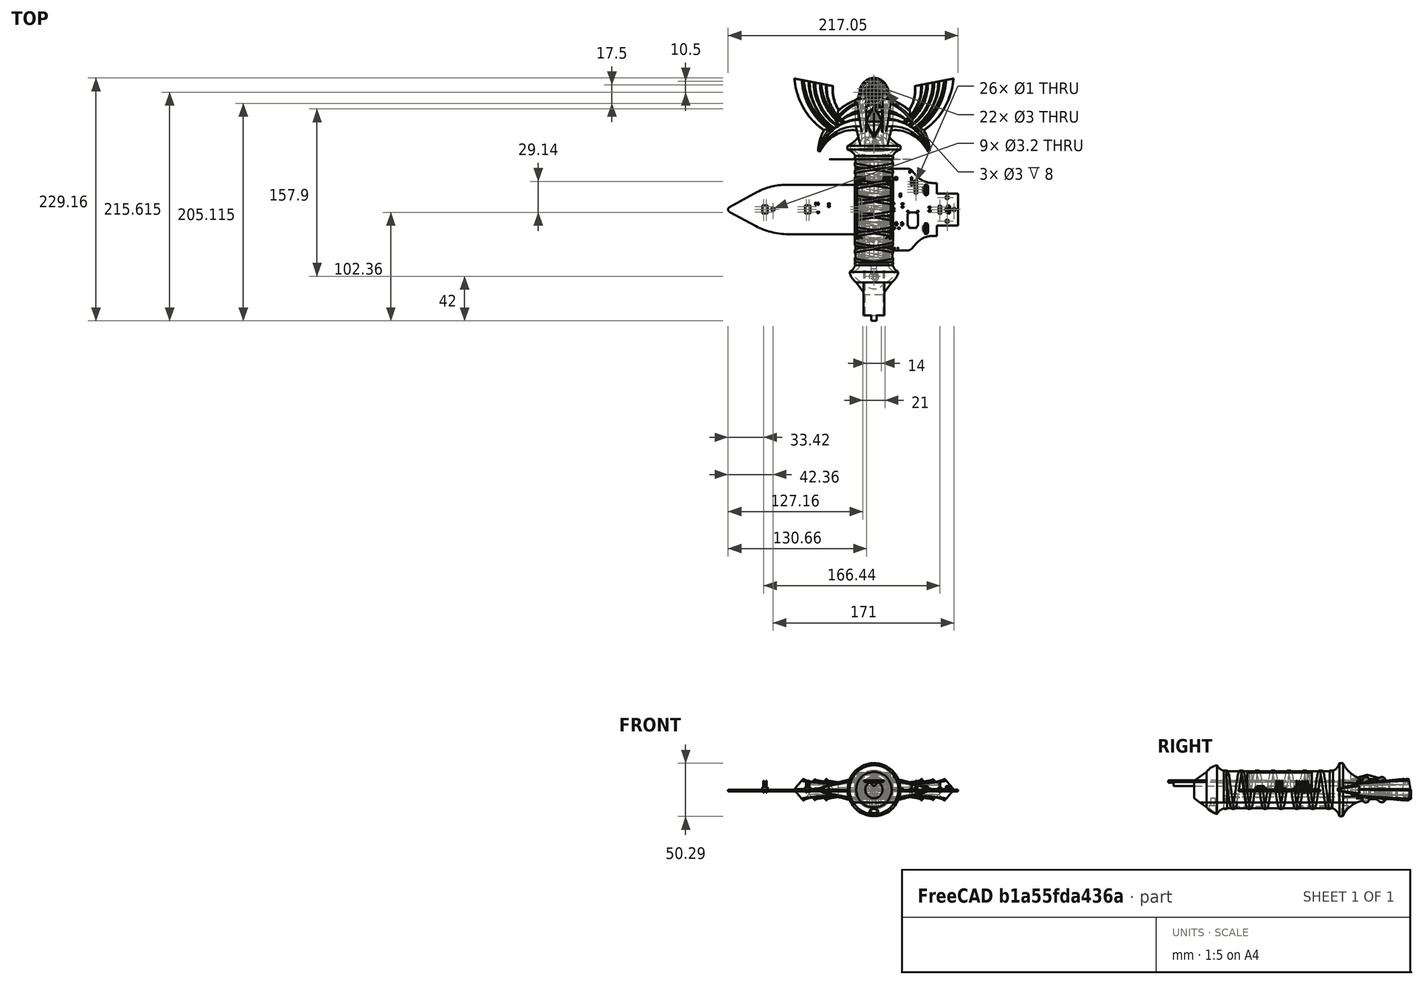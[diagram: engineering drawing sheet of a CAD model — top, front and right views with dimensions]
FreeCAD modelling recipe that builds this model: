
FCSTD DOCUMENT  (FreeCAD 1.0R39285 (Git))
Label: Neo-Neosword
License: All rights reserved
objects: Part::Feature×97, Sketcher::SketchObject×94, PartDesign::Pocket×40, PartDesign::Pad×22, PartDesign::Body×16, PartDesign::SubShapeBinder×12, App::Part×9, PartDesign::Revolution×5, PartDesign::AdditiveHelix×4, PartDesign::AdditivePipe×3, PartDesign::Groove×3, PartDesign::AdditiveLoft×2, PartDesign::Fillet×2, PartDesign::SubtractiveHelix×2, PartDesign::Mirrored×1, PartDesign::CoordinateSystem×1, PartDesign::SubtractiveCylinder×1, PartDesign::Chamfer×1, PartDesign::SubtractiveBox×1
note: 574 computed .brp shape members not serialized (recipe doc carries the construction recipe); baked Part::Feature solids carry a one-line shape summary decoded from their .brp

FEATURE [Sketcher::SketchObject] Sketch
  ArcFitTolerance = 1e-06
  AttachmentSupport = -> [XY_Plane001]
  FullyConstrained = false
  MakeInternals = false
  MapMode = 5
  sketch-geometry (17):
    g0: LineSegment StartX=17.5 StartY=50 StartZ=0 EndX=17.5 EndY=-50 EndZ=0
    g1: ArcOfCircle CenterX=27.5 CenterY=-50 CenterZ=0 NormalX=0 NormalY=0 NormalZ=1 AngleXU=0 Radius=10 StartAngle=3.14159 EndAngle=4.2478
    g2: LineSegment StartX=16.7299 StartY=-68.7091 StartZ=0 EndX=8.15223 EndY=-80.5471 EndZ=0
    g3: LineSegment StartX=8.15223 StartY=-80.5471 StartZ=0 EndX=0 EndY=-80.5471 EndZ=0
    g4: ArcOfCircle CenterX=8.2468 CenterY=-56.3383 CenterZ=0 NormalX=0 NormalY=0 NormalZ=1 AngleXU=0 Radius=15 StartAngle=5.31348 EndAngle=6.10885
    g5: ArcOfCircle CenterX=27.468 CenterY=46.0956 CenterZ=0 NormalX=0 NormalY=0 NormalZ=1 AngleXU=0 Radius=10.7054 StartAngle=1.80342 EndAngle=2.76827
    g6: LineSegment StartX=25.0001 StartY=56.5127 StartZ=0 EndX=25.0155 EndY=56.5163 EndZ=0
    g7: LineSegment StartX=25.0155 StartY=56.5163 StartZ=0 EndX=25 EndY=60 EndZ=0
    g8: ArcOfCircle CenterX=35.5717 CenterY=83.343 CenterZ=0 NormalX=0 NormalY=0 NormalZ=1 AngleXU=0 Radius=25.6254 StartAngle=3.07689 EndAngle=4.28714
    g9: LineSegment [constr] StartX=25 StartY=60 StartZ=0 EndX=41.707 EndY=52.4336 EndZ=0
    g10: LineSegment StartX=10 StartY=85 StartZ=0 EndX=4 EndY=85 EndZ=0
    g11: LineSegment [constr] StartX=0 StartY=50.6044 StartZ=0 EndX=0 EndY=85 EndZ=0
    g12: LineSegment StartX=0 StartY=-80.5471 StartZ=0 EndX=0 EndY=-51.46 EndZ=0
    g13: LineSegment StartX=0 StartY=-51.46 StartZ=0 EndX=15 EndY=-51.46 EndZ=0
    g14: LineSegment StartX=15 StartY=-51.46 StartZ=0 EndX=15 EndY=57.54 EndZ=0
    g15: LineSegment StartX=15 StartY=57.54 StartZ=0 EndX=4 EndY=57.54 EndZ=0
    g16: LineSegment StartX=4 StartY=57.54 StartZ=0 EndX=4 EndY=85 EndZ=0
  constraints (39):
    c: Symmetric(g0,g0,g-1)
    c: DistanceY(g0,g0) = 100
    c: DistanceX(g-1,g0) = 17.5
    c: Tangent(g1,g0) = -1.5708
    c: Coincident(g3,g2)
    c: PointOnObject(g3,g-2)
    c: Horizontal(g3)
    c: Coincident(g4,g1)
    c: Coincident(g2,g4)
    c: Radius(g1) = 10
    c: Radius(g4) = 15
    c: Coincident(g5,g0)
    c: Tangent(g6,g5) = 1.5708
    c: Coincident(g7,g6)
    c: Coincident(g8,g7)
    c: Coincident(g9,g7)
    c: Tangent(g8,g9)
    c: Coincident(g10,g8)
    c: PointOnObject(g11,g-2)
    c: Horizontal(g10)
    c: DistanceX(g11,g10) = 10
    c: DistanceX(g-1,g7) = 25
    c: DistanceY(g-1,g11) = 85
    c: DistanceY(g-1,g7) = 60
    c: Coincident(g3,g12)
    c: PointOnObject(g12,g-2)
    c: Coincident(g12,g13)
    c: Horizontal(g13)
    c: Coincident(g13,g14)
    c: Vertical(g14)
    c: Coincident(g14,g15)
    c: Horizontal(g15)
    c: Coincident(g15,g16)
    c: Vertical(g16)
    c: Coincident(g10,g16)
    c: DistanceY(g14,g14) = 109
    c: DistanceX(g-1,g13) = 15
    c: DistanceY(g-1,g15) = 57.54
    c: Distance(g10,g-2) = 4
FEATURE [PartDesign::Revolution] Revolution
  Angle = 360
  Angle2 = 60
  Axis = (0,1,0)
  Base = (0,0,0)
  Profile = -> Sketch
  ReferenceAxis = -> Sketch [V_Axis]
  Refine = true
  Reversed = true
  Suppressed = false
  Type = 0
FEATURE [Sketcher::SketchObject] Sketch001  label="InnerLower"
  ArcFitTolerance = 1e-06
  AttachmentOffset = pos=(0,0,0) rot=(0,-1,0;0.15708rad)
  AttachmentSupport = -> [YZ_Plane002]
  FullyConstrained = false
  MakeInternals = false
  MapMode = 5
  Placement = pos=(0,0,0) rot=(0.637718,0.544663,0.544663;2.00621rad)
  sketch-geometry (19):
    g0: LineSegment StartX=74.5124 StartY=0 StartZ=0 EndX=79.2425 EndY=9.91974 EndZ=0
    g1: LineSegment StartX=85.8137 StartY=9.96476 StartZ=0 EndX=86.5068 EndY=8.56092 EndZ=0
    g2: LineSegment StartX=88.3306 StartY=7.4275 StartZ=0 EndX=92.0222 EndY=7.42761 EndZ=0
    g3: ArcOfCircle CenterX=82.539 CenterY=8.34785 CenterZ=0 NormalX=0 NormalY=0 NormalZ=1 AngleXU=0 Radius=3.6521 StartAngle=0.458646 EndAngle=2.69665
    g4: GeomPoint [constr] X=82.4817 Y=16.7129 Z=0
    g5: GeomPoint [constr] X=100.651 Y=15.0454 Z=0
    g6: ArcOfCircle CenterX=88.3305 CenterY=9.4614 CenterZ=0 NormalX=0 NormalY=0 NormalZ=1 AngleXU=0 Radius=2.03391 StartAngle=3.60024 EndAngle=4.71242
    g7: GeomPoint [constr] X=87.0665 Y=7.42746 Z=0
    g8: GeomPoint [constr] X=93.3028 Y=7.41221 Z=0
    g9: LineSegment StartX=74.5124 StartY=0 StartZ=0 EndX=79.1575 EndY=-9.92971 EndZ=0
    g10: LineSegment StartX=85.9449 StartY=-9.87659 StartZ=0 EndX=86.4722 EndY=-8.70175 EndZ=0
    g11: LineSegment StartX=88.4642 StartY=-7.41239 StartZ=0 EndX=91.8885 EndY=-7.41239 EndZ=0
    g12: ArcOfCircle CenterX=82.539 CenterY=-8.34785 CenterZ=0 NormalX=0 NormalY=0 NormalZ=1 AngleXU=0 Radius=3.73322 StartAngle=3.57915 EndAngle=5.86128
    g13: GeomPoint [constr] X=82.6091 Y=-17.3082 Z=0
    g14: GeomPoint [constr] X=101.163 Y=-14.8795 Z=0
    g15: ArcOfCircle CenterX=88.4642 CenterY=-9.59588 CenterZ=0 NormalX=0 NormalY=0 NormalZ=1 AngleXU=0 Radius=2.18349 StartAngle=1.5708 EndAngle=2.71969
    g16: GeomPoint [constr] X=87.0509 Y=-7.41239 Z=0
    g17: GeomPoint [constr] X=93.3028 Y=-7.41221 Z=0
    g18: ArcOfCircle CenterX=92.7992 CenterY=0 CenterZ=0 NormalX=0 NormalY=0 NormalZ=1 AngleXU=0 Radius=7.46814 StartAngle=4.59013 EndAngle=7.95821
  constraints (25):
    c: PointOnObject(g0,g-1)
    c: PointOnObject(g4,g0)
    c: PointOnObject(g4,g1)
    c: Tangent(g0,g3) = 1.5708
    c: Tangent(g1,g3) = 1.5708
    c: PointOnObject(g7,g1)
    c: PointOnObject(g7,g2)
    c: Tangent(g1,g6) = -1.5708
    c: Tangent(g2,g6) = -1.5708
    c: Horizontal(g11)
    c: PointOnObject(g13,g9)
    c: PointOnObject(g13,g10)
    c: Tangent(g9,g12) = -1.5708
    c: Tangent(g10,g12) = -1.5708
    c: PointOnObject(g16,g10)
    c: PointOnObject(g16,g11)
    c: Tangent(g10,g15) = 1.5708
    c: Tangent(g11,g15) = 1.5708
    c: Coincident(g9,g0)
    c: Symmetric(g8,g17,g-1)
    c: Symmetric(g3,g12,g-1)
    c: PointOnObject(g18,g-1)
    c: Coincident(g18,g2)
    c: Coincident(g18,g11)
    c: DistanceY(g11,g2) = 14.84
FEATURE [Sketcher::SketchObject] Sketch002  label="OuterLower"
  ArcFitTolerance = 1e-06
  AttachmentOffset = pos=(0,0,-55) rot=(0,0,1;0rad)
  AttachmentSupport = -> [XZ_Plane002]
  FullyConstrained = false
  MakeInternals = false
  MapMode = 5
  Placement = pos=(0,55,-1.22e-14) rot=(1,0,0;1.5708rad)
  sketch-geometry (1):
    g0: Circle CenterX=51.7429 CenterY=0 CenterZ=0 NormalX=0 NormalY=0 NormalZ=1 AngleXU=0 Radius=1
  constraints (1):
    c: Diameter(g0) = 2
FEATURE [Sketcher::SketchObject] Sketch003  label="Arc"
  ArcFitTolerance = 1e-06
  AttachmentSupport = -> [XY_Plane002]
  FullyConstrained = false
  MakeInternals = false
  MapMode = 5
  sketch-geometry (1):
    g0: ArcOfCircle CenterX=9.26917 CenterY=46.1397 CenterZ=0 NormalX=0 NormalY=0 NormalZ=1 AngleXU=0 Radius=43.4172 StartAngle=0.208844 EndAngle=1.45835
FEATURE [PartDesign::AdditivePipe] AdditivePipe
  AuxilleryCurvelinear = true
  AuxillerySpineTangent = false
  Binormal = (0,0,0)
  Mode = 0
  Placement = pos=(0,0,0) rot=(1,1,1;2.0944rad)
  Profile = -> Sketch001
  Refine = true
  Sections = -> [Sketch002]
  Spine = -> Sketch003
  SpineTangent = false
  Suppressed = false
  Transformation = 1
  Transition = 0
FEATURE [Sketcher::SketchObject] Sketch004  label="InnerUpper"
  ArcFitTolerance = 1e-06
  AttachmentOffset = pos=(0,0,0) rot=(0,-1,0;0.15708rad)
  AttachmentSupport = -> [YZ_Plane002]
  FullyConstrained = false
  MakeInternals = false
  MapMode = 5
  Placement = pos=(0,0,0) rot=(0.637718,0.544663,0.544663;2.00621rad)
  sketch-geometry (20):
    g0: LineSegment [constr] StartX=90.1762 StartY=16.3594 StartZ=0 EndX=90.1771 EndY=-14.4859 EndZ=0
    g1: ArcOfCircle [constr] CenterX=82.5389 CenterY=8.36022 CenterZ=0 NormalX=0 NormalY=0 NormalZ=1 AngleXU=0 Radius=3.64672 StartAngle=0.455594 EndAngle=2.6997
    g2: ArcOfCircle [constr] CenterX=88.3632 CenterY=9.51401 CenterZ=0 NormalX=0 NormalY=0 NormalZ=1 AngleXU=0 Radius=2.08677 StartAngle=3.61591 EndAngle=4.69675
    g3: LineSegment [constr] StartX=85.8137 StartY=9.96476 StartZ=0 EndX=86.5068 EndY=8.56092 EndZ=0
    g4: LineSegment [constr] StartX=79.2425 StartY=9.91974 StartZ=0 EndX=74.8618 EndY=0.732718 EndZ=0
    g5: ArcOfCircle [constr] CenterX=82.5387 CenterY=-8.36022 CenterZ=0 NormalX=0 NormalY=0 NormalZ=1 AngleXU=0 Radius=3.64651 StartAngle=3.58348 EndAngle=5.82765
    g6: ArcOfCircle [constr] CenterX=88.3642 CenterY=-9.51401 CenterZ=0 NormalX=0 NormalY=0 NormalZ=1 AngleXU=0 Radius=2.08814 StartAngle=1.58646 EndAngle=2.66734
    g7: LineSegment [constr] StartX=85.8133 StartY=-9.96449 StartZ=0 EndX=86.5065 EndY=-8.56042 EndZ=0
    g8: LineSegment [constr] StartX=79.2424 StartY=-9.91964 StartZ=0 EndX=74.7059 EndY=-1.91141 EndZ=0
    g9: ArcOfCircle [constr] CenterX=64.7886 CenterY=0 CenterZ=0 NormalX=0 NormalY=0 NormalZ=1 AngleXU=0 Radius=10.0998 StartAngle=6.09278 EndAngle=6.3558
    g10: ArcOfCircle CenterX=97.8151 CenterY=8.36022 CenterZ=0 NormalX=0 NormalY=0 NormalZ=1 AngleXU=0 Radius=3.64651 StartAngle=0.441891 EndAngle=2.68605
    g11: ArcOfCircle CenterX=91.9895 CenterY=9.51401 CenterZ=0 NormalX=0 NormalY=0 NormalZ=1 AngleXU=0 Radius=2.08814 StartAngle=4.72805 EndAngle=5.80893
    g12: LineSegment StartX=94.5404 StartY=9.96449 StartZ=0 EndX=93.8472 EndY=8.56042 EndZ=0
    g13: LineSegment StartX=101.111 StartY=9.91964 StartZ=0 EndX=104.93 EndY=1.91141 EndZ=0
    g14: ArcOfCircle CenterX=97.8151 CenterY=-8.36022 CenterZ=0 NormalX=0 NormalY=0 NormalZ=1 AngleXU=0 Radius=3.64651 StartAngle=3.59713 EndAngle=5.84129
    g15: ArcOfCircle CenterX=91.9895 CenterY=-9.51401 CenterZ=0 NormalX=0 NormalY=0 NormalZ=1 AngleXU=0 Radius=2.08814 StartAngle=0.474251 EndAngle=1.55514
    g16: LineSegment StartX=94.5404 StartY=-9.96449 StartZ=0 EndX=93.8472 EndY=-8.56042 EndZ=0
    g17: LineSegment StartX=101.111 StartY=-9.91964 StartZ=0 EndX=104.93 EndY=-1.91142 EndZ=0
    g18: ArcOfCircle CenterX=115.564 CenterY=0 CenterZ=0 NormalX=0 NormalY=0 NormalZ=1 AngleXU=0 Radius=10.8041 StartAngle=2.96374 EndAngle=3.31944
    g19: ArcOfCircle CenterX=92.8797 CenterY=0 CenterZ=0 NormalX=0 NormalY=0 NormalZ=1 AngleXU=0 Radius=7.47546 StartAngle=1.68575 EndAngle=4.59744
  constraints (21):
    c: Coincident(g3,g1)
    c: Coincident(g3,g2)
    c: Coincident(g4,g1)
    c: Coincident(g7,g5)
    c: Coincident(g7,g6)
    c: Coincident(g8,g5)
    c: PointOnObject(g9,g-1)
    c: Coincident(g9,g4)
    c: Coincident(g9,g8)
    c: Coincident(g12,g10)
    c: Coincident(g12,g11)
    c: Coincident(g13,g10)
    c: Coincident(g16,g14)
    c: Coincident(g16,g15)
    c: Coincident(g17,g14)
    c: Coincident(g18,g13)
    c: Coincident(g18,g17)
    c: PointOnObject(g19,g-1)
    c: Coincident(g19,g11)
    c: Coincident(g19,g15)
    c: DistanceX(g-1,g13) = 104.93
FEATURE [Sketcher::SketchObject] Sketch005  label="OuterUpper"
  ArcFitTolerance = 1e-06
  AttachmentOffset = pos=(0,0,0) rot=(0,-1,0;0.383972rad)
  AttachmentSupport = -> [YZ_Plane002]
  FullyConstrained = false
  MakeInternals = false
  MapMode = 5
  Placement = pos=(0,0,0) rot=(0.723589,0.488067,0.488067;1.88883rad)
  sketch-geometry (5):
    g0: ArcOfCircle CenterX=85.1272 CenterY=0 CenterZ=0 NormalX=0 NormalY=0 NormalZ=1 AngleXU=0 Radius=4.5 StartAngle=1.5708 EndAngle=4.71239
    g1: ArcOfCircle CenterX=93.5 CenterY=0 CenterZ=0 NormalX=0 NormalY=0 NormalZ=1 AngleXU=0 Radius=4.5 StartAngle=4.71239 EndAngle=7.85398
    g2: LineSegment StartX=85.1272 StartY=4.5 StartZ=0 EndX=93.5 EndY=4.5 EndZ=0
    g3: LineSegment StartX=85.1272 StartY=-4.5 StartZ=0 EndX=93.5 EndY=-4.5 EndZ=0
    g4: GeomPoint X=98 Y=0 Z=0
  constraints (11):
    c: Tangent(g0,g2) = 1.5708
    c: Tangent(g0,g3) = -1.5708
    c: Tangent(g1,g2) = 1.5708
    c: Tangent(g1,g3) = -1.5708
    c: Equal(g0,g1)
    c: Horizontal(g3)
    c: PointOnObject(g0,g-1)
    c: PointOnObject(g4,g1)
    c: PointOnObject(g4,g-1)
    c: DistanceX(g-1,g4) = 98
    c: DistanceY(g1,g1) = 9
FEATURE [Sketcher::SketchObject] Sketch006  label="UpperArc"
  ArcFitTolerance = 1e-06
  AttachmentSupport = -> [XY_Plane002]
  FullyConstrained = false
  MakeInternals = false
  MapMode = 5
  sketch-geometry (1):
    g0: ArcOfCircle CenterX=9.26917 CenterY=46.1397 CenterZ=0 NormalX=0 NormalY=0 NormalZ=1 AngleXU=0 Radius=43.4172 StartAngle=1.05064 EndAngle=1.45835
FEATURE [PartDesign::AdditivePipe] AdditivePipe001
  AuxilleryCurvelinear = true
  AuxillerySpineTangent = false
  BaseFeature = -> AdditivePipe
  Binormal = (0,0,0)
  Mode = 0
  Placement = pos=(0,0,0) rot=(1,1,1;2.0944rad)
  Profile = -> Sketch004
  Refine = true
  Sections = -> [Sketch005]
  Spine = -> Sketch006
  SpineTangent = false
  Suppressed = false
  Transformation = 1
  Transition = 0
FEATURE [Sketcher::SketchObject] Sketch007  label="WingOuter"
  ArcFitTolerance = 1e-06
  AttachmentOffset = pos=(0,0,-109) rot=(0,2,0;0.191986rad)
  AttachmentSupport = -> [XZ_Plane002]
  FullyConstrained = false
  MakeInternals = false
  MapMode = 5
  Placement = pos=(0,109,-2.42e-14) rot=(0.990855,0.095409,0.095409;1.57998rad)
  sketch-geometry (35):
    g0: LineSegment StartX=76.3672 StartY=0.659592 StartZ=0 EndX=68.1495 EndY=10.0239 EndZ=0
    g1: LineSegment StartX=67.3939 StartY=10.0194 StartZ=0 EndX=62.9614 EndY=4.84362 EndZ=0
    g2: LineSegment StartX=61.8579 StartY=4.8047 StartZ=0 EndX=57.0799 EndY=9.64699 EndZ=0
    g3: LineSegment StartX=56.3686 StartY=9.64753 StartZ=0 EndX=51.5834 EndY=4.8124 EndZ=0
    g4: LineSegment StartX=50.48 StartY=4.85298 StartZ=0 EndX=46.1175 EndY=9.96245 EndZ=0
    g5: LineSegment StartX=45.3168 StartY=9.90834 StartZ=0 EndX=39.6601 EndY=1.11712 EndZ=0
    g6: LineSegment [constr] StartX=56.7313 StartY=18.9744 StartZ=0 EndX=56.7109 EndY=-8.18983 EndZ=0
    g7: ArcOfCircle CenterX=45.7372 CenterY=9.63779 CenterZ=0 NormalX=0 NormalY=0 NormalZ=1 AngleXU=0 Radius=0.5 StartAngle=0.706698 EndAngle=2.56984
    g8: GeomPoint [constr] X=45.6807 Y=10.474 Z=0
    g9: ArcOfCircle CenterX=56.724 CenterY=9.29581 CenterZ=0 NormalX=0 NormalY=0 NormalZ=1 AngleXU=0 Radius=0.5 StartAngle=0.778708 EndAngle=2.36138
    g10: GeomPoint [constr] X=56.7245 Y=10.0072 Z=0
    g11: ArcOfCircle CenterX=67.7737 CenterY=9.69413 CenterZ=0 NormalX=0 NormalY=0 NormalZ=1 AngleXU=0 Radius=0.5 StartAngle=0.720275 EndAngle=2.43339
    g12: GeomPoint [constr] X=67.769 Y=10.4574 Z=0
    g13: ArcOfCircle CenterX=62.3917 CenterY=5.33147 CenterZ=0 NormalX=0 NormalY=0 NormalZ=1 AngleXU=0 Radius=0.75 StartAngle=3.9203 EndAngle=5.57499
    g14: GeomPoint [constr] X=62.4308 Y=4.22405 Z=0
    g15: ArcOfCircle CenterX=51.0504 CenterY=5.33997 CenterZ=0 NormalX=0 NormalY=0 NormalZ=1 AngleXU=0 Radius=0.75 StartAngle=3.84829 EndAngle=5.50298
    g16: GeomPoint [constr] X=51.0096 Y=4.23262 Z=0
    g17: LineSegment StartX=76.3672 StartY=-0.659592 StartZ=0 EndX=68.1495 EndY=-10.0239 EndZ=0
    g18: LineSegment StartX=67.3939 StartY=-10.0194 StartZ=0 EndX=62.9614 EndY=-4.84362 EndZ=0
    g19: LineSegment StartX=61.8579 StartY=-4.8047 StartZ=0 EndX=57.0799 EndY=-9.64699 EndZ=0
    g20: LineSegment StartX=56.3686 StartY=-9.64753 StartZ=0 EndX=51.5834 EndY=-4.8124 EndZ=0
    g21: LineSegment StartX=50.48 StartY=-4.85298 StartZ=0 EndX=46.119 EndY=-9.96064 EndZ=0
    g22: LineSegment StartX=45.3174 StartY=-9.90511 StartZ=0 EndX=39.6564 EndY=-1.04163 EndZ=0
    g23: ArcOfCircle CenterX=45.7388 CenterY=-9.63598 CenterZ=0 NormalX=0 NormalY=0 NormalZ=1 AngleXU=0 Radius=0.5 StartAngle=3.70997 EndAngle=5.57649
    g24: GeomPoint [constr] X=45.6807 Y=-10.474 Z=0
    g25: ArcOfCircle CenterX=56.724 CenterY=-9.29581 CenterZ=0 NormalX=0 NormalY=0 NormalZ=1 AngleXU=0 Radius=0.5 StartAngle=3.9218 EndAngle=5.50448
    g26: GeomPoint [constr] X=56.7245 Y=-10.0072 Z=0
    g27: ArcOfCircle CenterX=67.7737 CenterY=-9.69413 CenterZ=0 NormalX=0 NormalY=0 NormalZ=1 AngleXU=0 Radius=0.5 StartAngle=3.84979 EndAngle=5.56291
    g28: GeomPoint [constr] X=67.769 Y=-10.4574 Z=0
    g29: ArcOfCircle CenterX=62.3917 CenterY=-5.33147 CenterZ=0 NormalX=0 NormalY=0 NormalZ=1 AngleXU=0 Radius=0.75 StartAngle=0.708198 EndAngle=2.36289
    g30: GeomPoint [constr] X=62.4308 Y=-4.22405 Z=0
    g31: ArcOfCircle CenterX=51.0504 CenterY=-5.33997 CenterZ=0 NormalX=0 NormalY=0 NormalZ=1 AngleXU=0 Radius=0.75 StartAngle=0.780208 EndAngle=2.43489
    g32: GeomPoint [constr] X=51.0096 Y=-4.23262 Z=0
    g33: ArcOfCircle CenterX=75.6156 CenterY=0 CenterZ=0 NormalX=0 NormalY=0 NormalZ=1 AngleXU=0 Radius=1 StartAngle=5.56291 EndAngle=7.00346
    g34: ArcOfCircle CenterX=41.342 CenterY=0.0349059 CenterZ=0 NormalX=0 NormalY=0 NormalZ=1 AngleXU=0 Radius=2 StartAngle=2.56984 EndAngle=3.70997
  constraints (59):
    c: PointOnObject(g10,g6)
    c: Symmetric(g16,g14,g6)
    c: Symmetric(g12,g8,g6)
    c: PointOnObject(g8,g5)
    c: PointOnObject(g8,g4)
    c: Tangent(g5,g7) = -1.5708
    c: Tangent(g4,g7) = -1.5708
    c: PointOnObject(g10,g3)
    c: PointOnObject(g10,g2)
    c: Tangent(g3,g9) = -1.5708
    c: Tangent(g2,g9) = -1.5708
    c: PointOnObject(g12,g1)
    c: PointOnObject(g12,g0)
    c: Tangent(g1,g11) = -1.5708
    c: Tangent(g0,g11) = -1.5708
    c: PointOnObject(g14,g2)
    c: PointOnObject(g14,g1)
    c: Tangent(g2,g13) = 1.5708
    c: Tangent(g1,g13) = 1.5708
    c: PointOnObject(g16,g4)
    c: PointOnObject(g16,g3)
    c: Tangent(g4,g15) = 1.5708
    c: Tangent(g3,g15) = 1.5708
    c: Radius(g7) = 0.5
    c: Radius(g9) = 0.5
    c: Radius(g11) = 0.5
    c: Radius(g13) = 0.75
    c: Radius(g15) = 0.75
    c: PointOnObject(g24,g22)
    c: PointOnObject(g24,g21)
    c: Tangent(g22,g23) = 1.5708
    c: Tangent(g21,g23) = 1.5708
    c: PointOnObject(g26,g20)
    c: PointOnObject(g26,g19)
    c: Tangent(g20,g25) = 1.5708
    c: Tangent(g19,g25) = 1.5708
    c: PointOnObject(g28,g18)
    c: PointOnObject(g28,g17)
    c: Tangent(g18,g27) = 1.5708
    c: Tangent(g17,g27) = 1.5708
    c: PointOnObject(g30,g19)
    c: PointOnObject(g30,g18)
    c: Tangent(g19,g29) = -1.5708
    c: Tangent(g18,g29) = -1.5708
    c: PointOnObject(g32,g21)
    c: PointOnObject(g32,g20)
    c: Tangent(g21,g31) = -1.5708
    c: Tangent(g20,g31) = -1.5708
    c: Radius(g23) = 0.5
    c: Radius(g25) = 0.5
    c: Radius(g27) = 0.5
    c: Radius(g29) = 0.75
    c: Radius(g31) = 0.75
    c: Tangent(g0,g33) = -1.5708
    c: Tangent(g17,g33) = 1.5708
    c: Tangent(g5,g34) = -1.5708
    c: Tangent(g22,g34) = 1.5708
    c: Radius(g34) = 2
    c: Radius(g33) = 1
FEATURE [Sketcher::SketchObject] Sketch008  label="WingInner"
  ArcFitTolerance = 1e-06
  AttachmentOffset = pos=(0,0,-94) rot=(0,1,0;-0.471239rad)
  AttachmentSupport = -> [XZ_Plane002]
  FullyConstrained = false
  MakeInternals = false
  MapMode = 5
  Placement = pos=(0,94,-2.09e-14) rot=(-0.94691,0.227333,0.227333;4.65787rad)
  sketch-geometry (24):
    g0: LineSegment StartX=24.9312 StartY=0 StartZ=0 EndX=28.939 EndY=6.0573 EndZ=0
    g1: LineSegment StartX=29.7174 StartY=6.12695 StartZ=0 EndX=32.213 EndY=3.51707 EndZ=0
    g2: LineSegment StartX=32.213 StartY=3.51707 StartZ=0 EndX=36.2883 EndY=6.3926 EndZ=0
    g3: LineSegment StartX=36.8654 StartY=6.39214 StartZ=0 EndX=40.9263 EndY=3.51707 EndZ=0
    g4: LineSegment StartX=40.9263 StartY=3.51707 StartZ=0 EndX=43.3532 EndY=5.56491 EndZ=0
    g5: LineSegment StartX=44.0749 StartY=5.48373 StartZ=0 EndX=48.2081 EndY=0 EndZ=0
    g6: LineSegment [constr] StartX=36.5696 StartY=10.6947 StartZ=0 EndX=36.5696 EndY=-8.06706 EndZ=0
    g7: ArcOfCircle CenterX=29.356 CenterY=5.7814 CenterZ=0 NormalX=0 NormalY=0 NormalZ=1 AngleXU=0 Radius=0.5 StartAngle=0.763015 EndAngle=2.55707
    g8: GeomPoint [constr] X=29.2846 Y=6.57957 Z=0
    g9: ArcOfCircle CenterX=36.5765 CenterY=5.98406 CenterZ=0 NormalX=0 NormalY=0 NormalZ=1 AngleXU=0 Radius=0.5 StartAngle=0.954722 EndAngle=2.18527
    g10: ArcOfCircle CenterX=43.6756 CenterY=5.18278 CenterZ=0 NormalX=0 NormalY=0 NormalZ=1 AngleXU=0 Radius=0.5 StartAngle=0.645874 EndAngle=2.27169
    g11: GeomPoint [constr] X=43.7569 Y=5.90561 Z=0
    g12: LineSegment StartX=24.9312 StartY=0 StartZ=0 EndX=28.939 EndY=-6.0573 EndZ=0
    g13: LineSegment StartX=29.7174 StartY=-6.12695 StartZ=0 EndX=32.213 EndY=-3.51707 EndZ=0
    g14: LineSegment StartX=32.213 StartY=-3.51707 StartZ=0 EndX=36.2883 EndY=-6.3926 EndZ=0
    g15: LineSegment StartX=36.8654 StartY=-6.39214 StartZ=0 EndX=40.9263 EndY=-3.51707 EndZ=0
    g16: LineSegment StartX=40.9263 StartY=-3.51707 StartZ=0 EndX=43.3532 EndY=-5.56491 EndZ=0
    g17: LineSegment StartX=44.0749 StartY=-5.48373 StartZ=0 EndX=48.2081 EndY=0 EndZ=0
    g18: ArcOfCircle CenterX=29.356 CenterY=-5.7814 CenterZ=0 NormalX=0 NormalY=0 NormalZ=1 AngleXU=0 Radius=0.5 StartAngle=3.72612 EndAngle=5.52017
    g19: GeomPoint [constr] X=29.2846 Y=-6.57957 Z=0
    g20: ArcOfCircle CenterX=36.5765 CenterY=-5.98406 CenterZ=0 NormalX=0 NormalY=0 NormalZ=1 AngleXU=0 Radius=0.5 StartAngle=4.09791 EndAngle=5.32846
    g21: GeomPoint [constr] X=36.577 Y=-6.59635 Z=0
    g22: ArcOfCircle CenterX=43.6756 CenterY=-5.18278 CenterZ=0 NormalX=0 NormalY=0 NormalZ=1 AngleXU=0 Radius=0.5 StartAngle=4.0115 EndAngle=5.63731
    g23: GeomPoint [constr] X=43.7569 Y=-5.90561 Z=0
  constraints (44):
    c: PointOnObject(g0,g-1)
    c: Coincident(g1,g2)
    c: Coincident(g3,g4)
    c: PointOnObject(g5,g-1)
    c: Symmetric(g1,g3,g6)
    c: Symmetric(g0,g5,g6)
    c: PointOnObject(g8,g0)
    c: PointOnObject(g8,g1)
    c: Tangent(g0,g7) = 1.5708
    c: Tangent(g1,g7) = 1.5708
    c: Tangent(g2,g9) = 1.5708
    c: Tangent(g3,g9) = 1.5708
    c: PointOnObject(g11,g4)
    c: PointOnObject(g11,g5)
    c: Tangent(g4,g10) = 1.5708
    c: Tangent(g5,g10) = 1.5708
    c: Radius(g10) = 0.5
    c: Radius(g9) = 0.5
    c: Radius(g7) = 0.5
    c: Coincident(g13,g14)
    c: Coincident(g15,g16)
    c: PointOnObject(g19,g12)
    c: PointOnObject(g19,g13)
    c: Tangent(g12,g18) = -1.5708
    c: Tangent(g13,g18) = -1.5708
    c: PointOnObject(g21,g14)
    c: PointOnObject(g21,g15)
    c: Tangent(g14,g20) = -1.5708
    c: Tangent(g15,g20) = -1.5708
    c: PointOnObject(g23,g16)
    c: PointOnObject(g23,g17)
    c: Tangent(g16,g22) = -1.5708
    c: Tangent(g17,g22) = -1.5708
    c: Radius(g22) = 0.5
    c: Radius(g20) = 0.5
    c: Radius(g18) = 0.5
    c: Symmetric(g7,g18,g-1)
    c: Symmetric(g20,g9,g-1)
    c: Coincident(g12,g0)
    c: Coincident(g17,g5)
    c: Vertical(g3,g15)
    c: Horizontal(g13,g15)
    c: Symmetric(g13,g1,g-1)
    c: Symmetric(g10,g22,g-1)
FEATURE [Sketcher::SketchObject] Sketch009  label="WingArc"
  ArcFitTolerance = 1e-06
  AttachmentSupport = -> [XY_Plane002]
  FullyConstrained = false
  MakeInternals = false
  MapMode = 5
  sketch-geometry (3):
    g0: GeomPoint [constr] X=32.5902 Y=77.3945 Z=0
    g1: GeomPoint [constr] X=55.6821 Y=119.824 Z=0
    g2: ArcOfCircle CenterX=5.31743 CenterY=119.736 CenterZ=0 NormalX=0 NormalY=0 NormalZ=1 AngleXU=0 Radius=50.3647 StartAngle=5.28462 EndAngle=6.28492
  constraints (2):
    c: Coincident(g2,g1)
    c: Coincident(g2,g0)
FEATURE [PartDesign::AdditivePipe] AdditivePipe002
  AuxilleryCurvelinear = true
  AuxillerySpineTangent = false
  BaseFeature = -> AdditivePipe001
  Binormal = (0,0,0)
  Mode = 0
  Placement = pos=(0,0,0) rot=(1,1,1;2.0944rad)
  Profile = -> Sketch008
  Refine = true
  Sections = -> [Sketch007]
  Spine = -> Sketch009
  SpineTangent = false
  Suppressed = false
  Transformation = 1
  Transition = 0
FEATURE [PartDesign::Mirrored] Mirrored
  BaseFeature = -> AdditivePipe002
  MirrorPlane = -> YZ_Plane002
  Originals = -> [AdditivePipe,AdditivePipe001,AdditivePipe002]
  Placement = pos=(0,0,0) rot=(1,1,1;2.0944rad)
  Refine = true
  Suppressed = false
  TransformMode = 0
FEATURE [Sketcher::SketchObject] Sketch010
  ArcFitTolerance = 1e-06
  AttachmentSupport = -> [XY_Plane003]
  FullyConstrained = false
  MakeInternals = false
  MapMode = 5
  sketch-geometry (18):
    g0: LineSegment StartX=12.6399 StartY=59.9845 StartZ=0 EndX=-12.6399 EndY=59.9845 EndZ=0
    g1: LineSegment StartX=-12.6399 StartY=59.9845 StartZ=0 EndX=-17.8679 EndY=82.0584 EndZ=0
    g2: LineSegment StartX=-17.8679 StartY=82.0584 StartZ=0 EndX=-17.8679 EndY=102.222 EndZ=0
    g3: LineSegment StartX=-15.8679 StartY=104.222 StartZ=0 EndX=-8.15434 EndY=104.222 EndZ=0
    g4: LineSegment StartX=-7.15434 StartY=103.222 StartZ=0 EndX=-7.15434 EndY=92.1893 EndZ=0
    g5: LineSegment StartX=-7.15434 StartY=92.1893 StartZ=0 EndX=7.15434 EndY=92.1893 EndZ=0
    g6: LineSegment StartX=7.15434 StartY=92.1893 StartZ=0 EndX=7.15434 EndY=103.222 EndZ=0
    g7: LineSegment StartX=8.15434 StartY=104.222 StartZ=0 EndX=15.8679 EndY=104.222 EndZ=0
    g8: LineSegment StartX=17.8679 StartY=102.222 StartZ=0 EndX=17.8679 EndY=82.0584 EndZ=0
    g9: LineSegment StartX=17.8679 StartY=82.0584 StartZ=0 EndX=12.6399 EndY=59.9845 EndZ=0
    g10: ArcOfCircle CenterX=-15.8679 CenterY=102.222 CenterZ=0 NormalX=0 NormalY=0 NormalZ=1 AngleXU=0 Radius=2 StartAngle=1.5708 EndAngle=3.14159
    g11: GeomPoint [constr] X=-17.8679 Y=104.222 Z=0
    g12: ArcOfCircle CenterX=15.8679 CenterY=102.222 CenterZ=0 NormalX=0 NormalY=0 NormalZ=1 AngleXU=0 Radius=2 StartAngle=-9e-16 EndAngle=1.5708
    g13: GeomPoint [constr] X=17.8679 Y=104.222 Z=0
    g14: ArcOfCircle CenterX=-8.15434 CenterY=103.222 CenterZ=0 NormalX=0 NormalY=0 NormalZ=1 AngleXU=0 Radius=1 StartAngle=0 EndAngle=1.5708
    g15: GeomPoint [constr] X=-7.15434 Y=104.222 Z=0
    g16: ArcOfCircle CenterX=8.15434 CenterY=103.222 CenterZ=0 NormalX=0 NormalY=0 NormalZ=1 AngleXU=0 Radius=1 StartAngle=1.5708 EndAngle=3.14159
    g17: GeomPoint [constr] X=7.15434 Y=104.222 Z=0
  constraints (35):
    c: Coincident(g0,g1)
    c: Coincident(g1,g2)
    c: Vertical(g2)
    c: Horizontal(g3)
    c: Vertical(g4)
    c: Coincident(g4,g5)
    c: Horizontal(g5)
    c: Coincident(g5,g6)
    c: Coincident(g8,g9)
    c: Coincident(g9,g0)
    c: Symmetric(g0,g0,g-2)
    c: Symmetric(g1,g8,g-2)
    c: Symmetric(g11,g13,g-2)
    c: Symmetric(g15,g17,g-2)
    c: Vertical(g6)
    c: PointOnObject(g11,g3)
    c: PointOnObject(g11,g2)
    c: Tangent(g3,g10) = 1.5708
    c: Tangent(g2,g10) = 1.5708
    c: PointOnObject(g13,g7)
    c: PointOnObject(g13,g8)
    c: Tangent(g7,g12) = 1.5708
    c: Tangent(g8,g12) = 1.5708
    c: PointOnObject(g15,g3)
    c: PointOnObject(g15,g4)
    c: Tangent(g3,g14) = 1.5708
    c: Tangent(g4,g14) = 1.5708
    c: PointOnObject(g17,g7)
    c: PointOnObject(g17,g6)
    c: Tangent(g7,g16) = 1.5708
    c: Tangent(g6,g16) = 1.5708
    c: Radius(g10) = 2
    c: Radius(g12) = 2
    c: Radius(g16) = 1
    c: Radius(g14) = 1
FEATURE [PartDesign::Pad] Pad
  Direction = (0,0,1)
  Length = 24
  Length2 = 10
  Midplane = true
  Profile = -> Sketch010
  ReferenceAxis = -> Sketch010 [N_Axis]
  Refine = true
  Suppressed = false
  Type = 0
FEATURE [Sketcher::SketchObject] Sketch011
  ArcFitTolerance = 1e-06
  AttachmentOffset = pos=(0,0,-54) rot=(0,0,1;0rad)
  AttachmentSupport = -> [XZ_Plane003]
  FullyConstrained = false
  MakeInternals = false
  MapMode = 5
  Placement = pos=(0,54,-1.2e-14) rot=(1,0,0;1.5708rad)
  sketch-geometry (24):
    g0: LineSegment StartX=-18.5965 StartY=0 StartZ=0 EndX=-18.5965 EndY=5.28721 EndZ=0
    g1: LineSegment StartX=-18.5965 StartY=5.28721 StartZ=0 EndX=-8.15434 EndY=8 EndZ=0
    g2: LineSegment StartX=0 StartY=13.8139 StartZ=0 EndX=-22.1179 EndY=13.8139 EndZ=0
    g3: LineSegment StartX=-22.1179 StartY=13.8139 StartZ=0 EndX=-22.1179 EndY=-0.189388 EndZ=0
    g4: LineSegment StartX=-8.15434 StartY=8 StartZ=0 EndX=-7.4432 EndY=8.1798 EndZ=0
    g5: LineSegment StartX=-7.4432 StartY=8.1798 StartZ=0 EndX=0 EndY=8.1798 EndZ=0
    g6: LineSegment StartX=-18.5965 StartY=0 StartZ=0 EndX=-18.5965 EndY=-5.37112 EndZ=0
    g7: LineSegment StartX=-18.5965 StartY=-5.37112 StartZ=0 EndX=-8.15434 EndY=-8 EndZ=0
    g8: LineSegment StartX=0 StartY=-17.7434 StartZ=0 EndX=-22.1179 EndY=-17.7434 EndZ=0
    g9: LineSegment StartX=-22.1179 StartY=-17.7434 StartZ=0 EndX=-22.1179 EndY=-0.189388 EndZ=0
    g10: LineSegment StartX=-8.15434 StartY=-8 StartZ=0 EndX=-7.4432 EndY=-8.25332 EndZ=0
    g11: LineSegment StartX=-7.4432 StartY=-8.25332 StartZ=0 EndX=0.11104 EndY=-8.25332 EndZ=0
    g12: LineSegment StartX=18.5313 StartY=-0.112287 StartZ=0 EndX=18.5313 EndY=5.28721 EndZ=0
    g13: LineSegment StartX=18.5313 StartY=5.28721 StartZ=0 EndX=8.15434 EndY=8 EndZ=0
    g14: LineSegment StartX=0 StartY=13.8139 StartZ=0 EndX=22.6589 EndY=13.8139 EndZ=0
    g15: LineSegment StartX=22.6589 StartY=13.8139 StartZ=0 EndX=22.6589 EndY=-0.111897 EndZ=0
    g16: LineSegment StartX=8.15434 StartY=8 StartZ=0 EndX=7.51991 EndY=8.1798 EndZ=0
    g17: LineSegment StartX=7.51991 StartY=8.1798 StartZ=0 EndX=0 EndY=8.1798 EndZ=0
    g18: LineSegment StartX=18.5313 StartY=-0.112287 StartZ=0 EndX=18.5313 EndY=-5.39949 EndZ=0
    g19: LineSegment StartX=18.5313 StartY=-5.39949 StartZ=0 EndX=8.15434 EndY=-8 EndZ=0
    g20: LineSegment StartX=0 StartY=-17.7434 StartZ=0 EndX=22.6589 EndY=-17.7434 EndZ=0
    g21: LineSegment StartX=22.6589 StartY=-17.7434 StartZ=0 EndX=22.6589 EndY=-0.111897 EndZ=0
    g22: LineSegment StartX=8.15434 StartY=-8 StartZ=0 EndX=7.55424 EndY=-8.25332 EndZ=0
    g23: LineSegment StartX=7.55424 StartY=-8.25332 StartZ=0 EndX=0.11104 EndY=-8.25332 EndZ=0
  constraints (43):
    c: PointOnObject(g0,g-1)
    c: Vertical(g0)
    c: Coincident(g0,g1)
    c: Horizontal(g2)
    c: Coincident(g2,g3)
    c: Vertical(g3)
    c: Coincident(g1,g4)
    c: Coincident(g4,g5)
    c: PointOnObject(g5,g-2)
    c: Horizontal(g5)
    c: PointOnObject(g2,g-2)
    c: Vertical(g6)
    c: Coincident(g6,g7)
    c: Horizontal(g8)
    c: Coincident(g8,g9)
    c: Vertical(g9)
    c: Coincident(g7,g10)
    c: Coincident(g10,g11)
    c: Horizontal(g11)
    c: Vertical(g12)
    c: Coincident(g12,g13)
    c: Horizontal(g14)
    c: Coincident(g14,g15)
    c: Vertical(g15)
    c: Coincident(g13,g16)
    c: Coincident(g16,g17)
    c: Horizontal(g17)
    c: Vertical(g18)
    c: Coincident(g18,g19)
    c: Horizontal(g20)
    c: Coincident(g20,g21)
    c: Vertical(g21)
    c: Coincident(g19,g22)
    c: Coincident(g22,g23)
    c: Horizontal(g23)
    c: Coincident(g9,g3)
    c: Coincident(g6,g0)
    c: Coincident(g21,g15)
    c: Coincident(g18,g12)
    c: Coincident(g5,g17)
    c: Coincident(g2,g14)
    c: Coincident(g23,g11)
    c: Coincident(g8,g20)
FEATURE [PartDesign::Pocket] Pocket
  BaseFeature = -> Pad
  Direction = (0,1,-2e-16)
  Length = 62
  Length2 = 5
  Profile = -> Sketch011
  ReferenceAxis = -> Sketch011 [N_Axis]
  Refine = true
  Suppressed = false
  Type = 0
FEATURE [Sketcher::SketchObject] Sketch012  label="Diamond001"
  ArcFitTolerance = 1e-06
  AttachmentOffset = pos=(0,0,8) rot=(0,0,1;0rad)
  AttachmentSupport = -> [XY_Plane004]
  FullyConstrained = false
  MakeInternals = false
  MapMode = 5
  Placement = pos=(0,0,8) rot=(0,0,1;0rad)
  sketch-geometry (5):
    g0: LineSegment StartX=0 StartY=93.5332 StartZ=0 EndX=-7.90137 EndY=79.1802 EndZ=0
    g1: LineSegment StartX=-7.90137 StartY=79.1802 StartZ=0 EndX=0 EndY=64.8272 EndZ=0
    g2: LineSegment StartX=0 StartY=93.5332 StartZ=0 EndX=7.90137 EndY=79.1802 EndZ=0
    g3: LineSegment StartX=7.90137 StartY=79.1802 StartZ=0 EndX=0 EndY=64.8272 EndZ=0
    g4: LineSegment [constr] StartX=-7.90137 StartY=79.1802 StartZ=0 EndX=7.90137 EndY=79.1802 EndZ=0
  constraints (9):
    c: PointOnObject(g0,g-2)
    c: Coincident(g0,g1)
    c: Coincident(g2,g3)
    c: Coincident(g0,g2)
    c: Coincident(g1,g3)
    c: Coincident(g4,g0)
    c: Coincident(g4,g2)
    c: Symmetric(g0,g1,g4)
    c: Symmetric(g0,g2,g-2)
FEATURE [Sketcher::SketchObject] Sketch013
  ArcFitTolerance = 1e-06
  AttachmentOffset = pos=(0,0,8) rot=(0,0,1;0rad)
  AttachmentSupport = -> [XY_Plane001]
  FullyConstrained = false
  MakeInternals = false
  MapMode = 5
  Placement = pos=(0,0,8) rot=(0,0,1;0rad)
  sketch-geometry (8):
    g0: LineSegment [constr] StartX=0 StartY=97 StartZ=0 EndX=-7.9 EndY=83 EndZ=0
    g1: LineSegment [constr] StartX=-7.9 StartY=83 StartZ=0 EndX=1.8e-15 EndY=68.3 EndZ=0
    g2: LineSegment [constr] StartX=0 StartY=97 StartZ=0 EndX=7.9 EndY=83 EndZ=0
    g3: LineSegment [constr] StartX=7.9 StartY=83 StartZ=0 EndX=1.8e-15 EndY=68.3 EndZ=0
    g4: LineSegment StartX=0 StartY=98 StartZ=0 EndX=-8.9 EndY=83 EndZ=0
    g5: LineSegment StartX=-8.9 StartY=83 StartZ=0 EndX=0 EndY=67.3 EndZ=0
    g6: LineSegment StartX=0 StartY=67.3 StartZ=0 EndX=8.9 EndY=83 EndZ=0
    g7: LineSegment StartX=8.9 StartY=83 StartZ=0 EndX=0 EndY=98 EndZ=0
  constraints (22):
    c: PointOnObject(g0,g-2)
    c: Coincident(g0,g1)
    c: Coincident(g2,g3)
    c: Coincident(g0,g2)
    c: Coincident(g1,g3)
    c: Symmetric(g0,g2,g-2)
    c: PointOnObject(g4,g-2)
    c: Coincident(g4,g5)
    c: PointOnObject(g5,g-2)
    c: Coincident(g5,g6)
    c: Coincident(g6,g7)
    c: Coincident(g7,g4)
    c: Horizontal(g0,g4)
    c: Horizontal(g2,g6)
    c: DistanceX(g-1,g2) = 7.9
    c: DistanceY(g5,g1) = 1
    c: DistanceY(g0,g4) = 1
    c: DistanceX(g2,g6) = 1
    c: DistanceX(g4,g0) = 1
    c: DistanceY(g-1,g4) = 98
    c: DistanceY(g5,g4) = 30.7
    c: DistanceY(g4,g4) = 15
FEATURE [PartDesign::Pocket] Pocket001  label="Diamond Dimple"
  BaseFeature = -> Revolution
  Direction = (0,0,-1)
  Length = 21
  Length2 = 5
  Profile = -> Sketch013
  ReferenceAxis = -> Sketch013 [N_Axis]
  Refine = true
  Reversed = true
  Suppressed = false
  Type = 0
FEATURE [Sketcher::SketchObject] Sketch014
  ArcFitTolerance = 1e-06
  AttachmentSupport = -> [YZ_Plane004]
  ExternalGeometry = -> [Sketch012]
  FullyConstrained = false
  MakeInternals = false
  MapMode = 5
  Placement = pos=(0,0,0) rot=(0.57735,0.57735,0.57735;2.0944rad)
  sketch-geometry (1):
    g0: LineSegment StartX=79.1802 StartY=8 StartZ=0 EndX=79.1802 EndY=12.611 EndZ=0
  constraints (2):
    c: Vertical(g0)
    c: Coincident(g0,g-3)
FEATURE [PartDesign::AdditiveLoft] AdditiveLoft
  Closed = false
  Profile = -> Sketch012
  Refine = true
  Ruled = false
  Sections = -> [Sketch014]
  Suppressed = false
FEATURE [PartDesign::Body] Body003  label="Diamond"
  AllowCompound = true
  Group = -> [Sketch012,Sketch014,AdditiveLoft]
  Origin = -> Origin004
  Tip = -> AdditiveLoft
FEATURE [Sketcher::SketchObject] Sketch015
  ArcFitTolerance = 1e-06
  AttachmentSupport = -> [YZ_Plane005]
  FullyConstrained = true
  MakeInternals = false
  MapMode = 5
  Placement = pos=(0,0,0) rot=(0.57735,0.57735,0.57735;2.0944rad)
  sketch-geometry (4):
    g0: ArcOfCircle CenterX=-52 CenterY=17.5 CenterZ=0 NormalX=0 NormalY=0 NormalZ=1 AngleXU=0 Radius=0.6 StartAngle=1.5708 EndAngle=4.71239
    g1: ArcOfCircle CenterX=-50 CenterY=17.5 CenterZ=0 NormalX=0 NormalY=0 NormalZ=1 AngleXU=0 Radius=0.6 StartAngle=4.71239 EndAngle=7.85398
    g2: LineSegment StartX=-52 StartY=18.1 StartZ=0 EndX=-50 EndY=18.1 EndZ=0
    g3: LineSegment StartX=-52 StartY=16.9 StartZ=0 EndX=-50 EndY=16.9 EndZ=0
  constraints (10):
    c: Tangent(g0,g2) = 1.5708
    c: Tangent(g0,g3) = -1.5708
    c: Tangent(g1,g2) = 1.5708
    c: Tangent(g1,g3) = -1.5708
    c: Equal(g0,g1)
    c: Horizontal(g2)
    c: DistanceX(g0,g1) = 2
    c: DistanceY(g1,g1) = 1.2
    c: DistanceY(g-1,g0) = 17.5
    c: DistanceX(g1,g-1) = 50
FEATURE [PartDesign::Revolution] Revolution001
  Angle = 360
  Angle2 = 60
  Axis = (0,1,0)
  Base = (0,0,0)
  Placement = pos=(0,0,0) rot=(1,1,1;2.0944rad)
  Profile = -> Sketch015
  ReferenceAxis = -> Sketch015 [H_Axis]
  Refine = true
  Suppressed = false
  Type = 0
FEATURE [Sketcher::SketchObject] Sketch016
  ArcFitTolerance = 1e-06
  AttachmentSupport = -> [YZ_Plane005]
  FullyConstrained = true
  MakeInternals = false
  MapMode = 5
  Placement = pos=(0,0,0) rot=(0.57735,0.57735,0.57735;2.0944rad)
  sketch-geometry (4):
    g0: ArcOfCircle CenterX=48 CenterY=17.5 CenterZ=0 NormalX=0 NormalY=0 NormalZ=1 AngleXU=0 Radius=0.6 StartAngle=1.5708 EndAngle=4.71239
    g1: ArcOfCircle CenterX=50 CenterY=17.5 CenterZ=0 NormalX=0 NormalY=0 NormalZ=1 AngleXU=0 Radius=0.6 StartAngle=4.71239 EndAngle=7.85398
    g2: LineSegment StartX=48 StartY=18.1 StartZ=0 EndX=50 EndY=18.1 EndZ=0
    g3: LineSegment StartX=48 StartY=16.9 StartZ=0 EndX=50 EndY=16.9 EndZ=0
  constraints (10):
    c: Tangent(g0,g2) = 1.5708
    c: Tangent(g0,g3) = -1.5708
    c: Tangent(g1,g2) = 1.5708
    c: Tangent(g1,g3) = -1.5708
    c: Equal(g0,g1)
    c: Horizontal(g2)
    c: DistanceX(g0,g1) = 2
    c: DistanceY(g1,g1) = 1.2
    c: DistanceY(g-1,g0) = 17.5
    c: DistanceX(g-1,g0) = 48
FEATURE [PartDesign::Revolution] Revolution002
  Angle = 360
  Angle2 = 60
  Axis = (0,1,0)
  Base = (0,0,0)
  BaseFeature = -> Revolution001
  Placement = pos=(0,0,0) rot=(1,1,1;2.0944rad)
  Profile = -> Sketch016
  ReferenceAxis = -> Sketch016 [H_Axis]
  Refine = true
  Suppressed = false
  Type = 0
FEATURE [Sketcher::SketchObject] Sketch017
  ArcFitTolerance = 1e-06
  AttachmentSupport = -> [YZ_Plane005]
  FullyConstrained = true
  MakeInternals = false
  MapMode = 5
  Placement = pos=(0,0,0) rot=(0.57735,0.57735,0.57735;2.0944rad)
  sketch-geometry (4):
    g0: ArcOfCircle CenterX=-52 CenterY=17.5 CenterZ=0 NormalX=0 NormalY=0 NormalZ=1 AngleXU=0 Radius=0.6 StartAngle=1.5708 EndAngle=4.71239
    g1: ArcOfCircle CenterX=-50 CenterY=17.5 CenterZ=0 NormalX=0 NormalY=0 NormalZ=1 AngleXU=0 Radius=0.6 StartAngle=4.71239 EndAngle=7.85398
    g2: LineSegment StartX=-52 StartY=18.1 StartZ=0 EndX=-50 EndY=18.1 EndZ=0
    g3: LineSegment StartX=-52 StartY=16.9 StartZ=0 EndX=-50 EndY=16.9 EndZ=0
  constraints (10):
    c: Tangent(g0,g2) = 1.5708
    c: Tangent(g0,g3) = -1.5708
    c: Tangent(g1,g2) = 1.5708
    c: Tangent(g1,g3) = -1.5708
    c: Equal(g0,g1)
    c: Horizontal(g2)
    c: DistanceX(g0,g1) = 2
    c: DistanceY(g1,g1) = 1.2
    c: DistanceY(g-1,g0) = 17.5
    c: DistanceX(g1,g-1) = 50
FEATURE [PartDesign::AdditiveHelix] AdditiveHelix
  Angle = 0
  Axis = (0,1,0)
  Base = (0,0,0)
  BaseFeature = -> Revolution002
  Growth = 0
  HasBeenEdited = true
  Height = 100
  LeftHanded = false
  Mode = 0
  Outside = false
  Pitch = 15
  Placement = pos=(0,0,0) rot=(1,1,1;2.0944rad)
  Profile = -> Sketch017
  ReferenceAxis = -> Sketch017 [H_Axis]
  Refine = true
  Suppressed = false
  Tolerance = 0.1
  Turns = 6.66667
FEATURE [Sketcher::SketchObject] Sketch018
  ArcFitTolerance = 1e-06
  AttachmentSupport = -> [YZ_Plane005]
  FullyConstrained = true
  MakeInternals = false
  MapMode = 5
  Placement = pos=(0,0,0) rot=(0.57735,0.57735,0.57735;2.0944rad)
  sketch-geometry (4):
    g0: ArcOfCircle CenterX=-52 CenterY=17.5 CenterZ=0 NormalX=0 NormalY=0 NormalZ=1 AngleXU=0 Radius=0.6 StartAngle=1.5708 EndAngle=4.71239
    g1: ArcOfCircle CenterX=-50 CenterY=17.5 CenterZ=0 NormalX=0 NormalY=0 NormalZ=1 AngleXU=0 Radius=0.6 StartAngle=4.71239 EndAngle=7.85398
    g2: LineSegment StartX=-52 StartY=18.1 StartZ=0 EndX=-50 EndY=18.1 EndZ=0
    g3: LineSegment StartX=-52 StartY=16.9 StartZ=0 EndX=-50 EndY=16.9 EndZ=0
  constraints (10):
    c: Tangent(g0,g2) = 1.5708
    c: Tangent(g0,g3) = -1.5708
    c: Tangent(g1,g2) = 1.5708
    c: Tangent(g1,g3) = -1.5708
    c: Equal(g0,g1)
    c: Horizontal(g2)
    c: DistanceX(g0,g1) = 2
    c: DistanceY(g1,g1) = 1.2
    c: DistanceY(g-1,g0) = 17.5
    c: DistanceX(g1,g-1) = 50
FEATURE [PartDesign::AdditiveHelix] AdditiveHelix001
  Angle = 0
  Axis = (0,1,0)
  Base = (0,0,0)
  BaseFeature = -> AdditiveHelix
  Growth = 0
  HasBeenEdited = true
  Height = 100
  LeftHanded = true
  Mode = 0
  Outside = false
  Pitch = 15
  Placement = pos=(0,0,0) rot=(1,1,1;2.0944rad)
  Profile = -> Sketch018
  ReferenceAxis = -> Sketch018 [H_Axis]
  Refine = true
  Suppressed = false
  Tolerance = 0.1
  Turns = 6.66667
FEATURE [PartDesign::CoordinateSystem] Local_CS_259c
  AttacherType = Attacher::AttachEngine3D
  MapMode = 2
FEATURE [Part::Feature] Pcb_259c
  Placement = pos=(-179.7,105.7,0) rot=(0,0,1;0rad)
  shape: bbox 217 x 77.11 x 1.6 mm, 325 faces (baked)
FEATURE [Sketcher::SketchObject] PCB_Sketch_259c
  ArcFitTolerance = 1e-06
  FullyConstrained = false
  MakeInternals = false
  sketch-geometry (225):
    g0: LineSegment StartX=-137.665 StartY=0.013451 StartZ=0 EndX=-137.658 EndY=0.196135 EndZ=0
    g1: LineSegment StartX=-137.658 StartY=0.196135 StartZ=0 EndX=-137.64 EndY=0.376444 EndZ=0
    g2: LineSegment StartX=-137.64 StartY=0.376444 StartZ=0 EndX=-137.609 EndY=0.553855 EndZ=0
    g3: LineSegment StartX=-137.609 StartY=0.553855 StartZ=0 EndX=-137.567 EndY=0.727848 EndZ=0
    g4: LineSegment StartX=-137.567 StartY=0.727848 StartZ=0 EndX=-137.514 EndY=0.897898 EndZ=0
    g5: LineSegment StartX=-137.514 StartY=0.897898 StartZ=0 EndX=-137.449 EndY=1.06348 EndZ=0
    g6: LineSegment StartX=-137.449 StartY=1.06348 StartZ=0 EndX=-137.374 EndY=1.22408 EndZ=0
    g7: LineSegment StartX=-137.374 StartY=1.22408 StartZ=0 EndX=-137.288 EndY=1.37917 EndZ=0
    g8: LineSegment StartX=-137.288 StartY=1.37917 StartZ=0 EndX=-137.192 EndY=1.52823 EndZ=0
    g9: LineSegment StartX=-137.192 StartY=1.52823 StartZ=0 EndX=-137.087 EndY=1.67073 EndZ=0
    g10: LineSegment StartX=-137.087 StartY=1.67073 StartZ=0 EndX=-136.971 EndY=1.80615 EndZ=0
    g11: LineSegment StartX=-136.971 StartY=1.80615 StartZ=0 EndX=-136.847 EndY=1.93398 EndZ=0
    g12: LineSegment StartX=-136.847 StartY=1.93398 StartZ=0 EndX=-136.714 EndY=2.05368 EndZ=0
    g13: LineSegment StartX=-136.714 StartY=2.05368 StartZ=0 EndX=-136.572 EndY=2.16473 EndZ=0
    g14: LineSegment StartX=-136.572 StartY=2.16473 StartZ=0 EndX=-136.422 EndY=2.26662 EndZ=0
    g15: LineSegment StartX=-136.422 StartY=2.26662 StartZ=0 EndX=-136.265 EndY=2.35882 EndZ=0
    g16: LineSegment StartX=-136.265 StartY=2.35882 StartZ=0 EndX=-110.065 EndY=16.4831 EndZ=0
    g17: LineSegment StartX=-110.065 StartY=16.4831 StartZ=0 EndX=-108.497 EndY=17.297 EndZ=0
    g18: LineSegment StartX=-108.497 StartY=17.297 StartZ=0 EndX=-106.908 EndY=18.0606 EndZ=0
    g19: LineSegment StartX=-106.908 StartY=18.0606 StartZ=0 EndX=-105.298 EndY=18.7737 EndZ=0
    g20: LineSegment StartX=-105.298 StartY=18.7737 StartZ=0 EndX=-103.669 EndY=19.4359 EndZ=0
    g21: LineSegment StartX=-103.669 StartY=19.4359 StartZ=0 EndX=-102.022 EndY=20.0468 EndZ=0
    g22: LineSegment StartX=-102.022 StartY=20.0468 StartZ=0 EndX=-100.357 EndY=20.6063 EndZ=0
    g23: LineSegment StartX=-100.357 StartY=20.6063 StartZ=0 EndX=-98.6774 EndY=21.1139 EndZ=0
    g24: LineSegment StartX=-98.6774 StartY=21.1139 StartZ=0 EndX=-96.9831 EndY=21.5694 EndZ=0
    g25: LineSegment StartX=-96.9831 StartY=21.5694 StartZ=0 EndX=-95.2755 EndY=21.9725 EndZ=0
    g26: LineSegment StartX=-95.2755 StartY=21.9725 StartZ=0 EndX=-93.5559 EndY=22.3228 EndZ=0
    g27: LineSegment StartX=-93.5559 StartY=22.3228 StartZ=0 EndX=-91.8256 EndY=22.6201 EndZ=0
    g28: LineSegment StartX=-91.8256 StartY=22.6201 StartZ=0 EndX=-90.0856 EndY=22.8641 EndZ=0
    g29: LineSegment StartX=-90.0856 StartY=22.8641 StartZ=0 EndX=-88.3373 EndY=23.0543 EndZ=0
    g30: LineSegment StartX=-88.3373 StartY=23.0543 StartZ=0 EndX=-86.5819 EndY=23.1906 EndZ=0
    g31: LineSegment StartX=-86.5819 StartY=23.1906 StartZ=0 EndX=-84.8206 EndY=23.2726 EndZ=0
    g32: LineSegment StartX=-84.8206 StartY=23.2726 StartZ=0 EndX=-83.0546 EndY=23.3 EndZ=0
    g33: LineSegment StartX=-83.0546 StartY=23.3 StartZ=0 EndX=-19.5 EndY=23.3 EndZ=0
    g34: LineSegment StartX=-19.5 StartY=23.3 StartZ=0 EndX=-18.7908 EndY=23.3126 EndZ=0
    g35: LineSegment StartX=-18.7908 StartY=23.3126 StartZ=0 EndX=-18.084 EndY=23.3502 EndZ=0
    g36: LineSegment StartX=-18.084 StartY=23.3502 StartZ=0 EndX=-17.3804 EndY=23.4126 EndZ=0
    g37: LineSegment StartX=-17.3804 StartY=23.4126 StartZ=0 EndX=-16.6805 EndY=23.4997 EndZ=0
    g38: LineSegment StartX=-16.6805 StartY=23.4997 StartZ=0 EndX=-15.9849 EndY=23.6113 EndZ=0
    g39: LineSegment StartX=-15.9849 StartY=23.6113 StartZ=0 EndX=-15.2943 EndY=23.7472 EndZ=0
    g40: LineSegment StartX=-15.2943 StartY=23.7472 StartZ=0 EndX=-14.6093 EndY=23.9072 EndZ=0
    g41: LineSegment StartX=-14.6093 StartY=23.9072 StartZ=0 EndX=-13.9306 EndY=24.0911 EndZ=0
    g42: LineSegment StartX=-13.9306 StartY=24.0911 StartZ=0 EndX=-13.2588 EndY=24.2988 EndZ=0
    g43: LineSegment StartX=-13.2588 StartY=24.2988 StartZ=0 EndX=-12.5944 EndY=24.53 EndZ=0
    g44: LineSegment StartX=-12.5944 StartY=24.53 StartZ=0 EndX=-11.9383 EndY=24.7846 EndZ=0
    g45: LineSegment StartX=-11.9383 StartY=24.7846 StartZ=0 EndX=-11.2909 EndY=25.0624 EndZ=0
    g46: LineSegment StartX=-11.2909 StartY=25.0624 StartZ=0 EndX=-10.6529 EndY=25.3632 EndZ=0
    g47: LineSegment StartX=-10.6529 StartY=25.3632 StartZ=0 EndX=-10.025 EndY=25.6868 EndZ=0
    g48: LineSegment StartX=-10.025 StartY=25.6868 StartZ=0 EndX=-9.40773 EndY=26.0331 EndZ=0
    g49: LineSegment StartX=-9.40773 StartY=26.0331 StartZ=0 EndX=-8.8018 EndY=26.4018 EndZ=0
    g50: LineSegment StartX=-8.8018 StartY=26.4018 StartZ=0 EndX=9.1896 EndY=37.7921 EndZ=0
    g51: LineSegment StartX=9.1896 StartY=37.7921 StartZ=0 EndX=9.34108 EndY=37.8843 EndZ=0
    g52: LineSegment StartX=9.34108 StartY=37.8843 StartZ=0 EndX=9.49539 EndY=37.9709 EndZ=0
    g53: LineSegment StartX=9.49539 StartY=37.9709 StartZ=0 EndX=9.65237 EndY=38.0518 EndZ=0
    g54: LineSegment StartX=9.65237 StartY=38.0518 StartZ=0 EndX=9.81186 EndY=38.127 EndZ=0
    g55: LineSegment StartX=9.81186 StartY=38.127 StartZ=0 EndX=9.9737 EndY=38.1964 EndZ=0
    g56: LineSegment StartX=9.9737 StartY=38.1964 StartZ=0 EndX=10.1377 EndY=38.2601 EndZ=0
    g57: LineSegment StartX=10.1377 StartY=38.2601 StartZ=0 EndX=10.3038 EndY=38.3179 EndZ=0
    g58: LineSegment StartX=10.3038 StartY=38.3179 StartZ=0 EndX=10.4718 EndY=38.3698 EndZ=0
    g59: LineSegment StartX=10.4718 StartY=38.3698 StartZ=0 EndX=10.6415 EndY=38.4158 EndZ=0
    g60: LineSegment StartX=10.6415 StartY=38.4158 StartZ=0 EndX=10.8127 EndY=38.4558 EndZ=0
    g61: LineSegment StartX=10.8127 StartY=38.4558 StartZ=0 EndX=10.9853 EndY=38.4898 EndZ=0
    g62: LineSegment StartX=10.9853 StartY=38.4898 StartZ=0 EndX=11.1592 EndY=38.5177 EndZ=0
    g63: LineSegment StartX=11.1592 StartY=38.5177 StartZ=0 EndX=11.3342 EndY=38.5395 EndZ=0
    g64: LineSegment StartX=11.3342 StartY=38.5395 StartZ=0 EndX=11.5101 EndY=38.5551 EndZ=0
    g65: LineSegment StartX=11.5101 StartY=38.5551 StartZ=0 EndX=11.6868 EndY=38.5645 EndZ=0
    g66: LineSegment StartX=11.6868 StartY=38.5645 StartZ=0 EndX=11.8641 EndY=38.5676 EndZ=0
    g67: LineSegment StartX=11.8641 StartY=38.5676 StartZ=0 EndX=31.8641 EndY=38.5676 EndZ=0
    g68: LineSegment StartX=31.8641 StartY=38.5676 StartZ=0 EndX=32.1279 EndY=38.5606 EndZ=0
    g69: LineSegment StartX=32.1279 StartY=38.5606 StartZ=0 EndX=32.3896 EndY=38.5399 EndZ=0
    g70: LineSegment StartX=32.3896 StartY=38.5399 StartZ=0 EndX=32.6487 EndY=38.5057 EndZ=0
    g71: LineSegment StartX=32.6487 StartY=38.5057 StartZ=0 EndX=32.9049 EndY=38.4581 EndZ=0
    g72: LineSegment StartX=32.9049 StartY=38.4581 StartZ=0 EndX=33.1576 EndY=38.3974 EndZ=0
    g73: LineSegment StartX=33.1576 StartY=38.3974 StartZ=0 EndX=33.4064 EndY=38.3238 EndZ=0
    g74: LineSegment StartX=33.4064 StartY=38.3238 StartZ=0 EndX=33.6506 EndY=38.2376 EndZ=0
    g75: LineSegment StartX=33.6506 StartY=38.2376 StartZ=0 EndX=33.89 EndY=38.1388 EndZ=0
    g76: LineSegment StartX=33.89 StartY=38.1388 StartZ=0 EndX=34.1239 EndY=38.0278 EndZ=0
    g77: LineSegment StartX=34.1239 StartY=38.0278 StartZ=0 EndX=34.3518 EndY=37.9048 EndZ=0
    g78: LineSegment StartX=34.3518 StartY=37.9048 StartZ=0 EndX=34.5734 EndY=37.77 EndZ=0
    g79: LineSegment StartX=34.5734 StartY=37.77 StartZ=0 EndX=34.7881 EndY=37.6236 EndZ=0
    g80: LineSegment StartX=34.7881 StartY=37.6236 StartZ=0 EndX=34.9954 EndY=37.4657 EndZ=0
    g81: LineSegment StartX=34.9954 StartY=37.4657 StartZ=0 EndX=35.1949 EndY=37.2967 EndZ=0
    g82: LineSegment StartX=35.1949 StartY=37.2967 StartZ=0 EndX=35.386 EndY=37.1168 EndZ=0
    g83: LineSegment StartX=35.386 StartY=37.1168 StartZ=0 EndX=35.5683 EndY=36.9261 EndZ=0
    g84: LineSegment StartX=35.5683 StartY=36.9261 StartZ=0 EndX=40.4159 EndY=31.5796 EndZ=0
    g85: LineSegment StartX=40.4159 StartY=31.5796 StartZ=0 EndX=41.145 EndY=30.8168 EndZ=0
    g86: LineSegment StartX=41.145 StartY=30.8168 StartZ=0 EndX=41.9095 EndY=30.0969 EndZ=0
    g87: LineSegment StartX=41.9095 StartY=30.0969 StartZ=0 EndX=42.7074 EndY=29.421 EndZ=0
    g88: LineSegment StartX=42.7074 StartY=29.421 StartZ=0 EndX=43.5366 EndY=28.7896 EndZ=0
    g89: LineSegment StartX=43.5366 StartY=28.7896 StartZ=0 EndX=44.3954 EndY=28.2039 EndZ=0
    g90: LineSegment StartX=44.3954 StartY=28.2039 StartZ=0 EndX=45.2818 EndY=27.6646 EndZ=0
    g91: LineSegment StartX=45.2818 StartY=27.6646 StartZ=0 EndX=46.1937 EndY=27.1725 EndZ=0
    g92: LineSegment StartX=46.1937 StartY=27.1725 StartZ=0 EndX=47.1293 EndY=26.7286 EndZ=0
    g93: LineSegment StartX=47.1293 StartY=26.7286 StartZ=0 EndX=48.0866 EndY=26.3336 EndZ=0
    g94: LineSegment StartX=48.0866 StartY=26.3336 StartZ=0 EndX=49.0637 EndY=25.9886 EndZ=0
    g95: LineSegment StartX=49.0637 StartY=25.9886 StartZ=0 EndX=50.0586 EndY=25.6942 EndZ=0
    g96: LineSegment StartX=50.0586 StartY=25.6942 StartZ=0 EndX=51.0694 EndY=25.4515 EndZ=0
    g97: LineSegment StartX=51.0694 StartY=25.4515 StartZ=0 EndX=52.0941 EndY=25.2612 EndZ=0
    g98: LineSegment StartX=52.0941 StartY=25.2612 StartZ=0 EndX=53.1308 EndY=25.1242 EndZ=0
    g99: LineSegment StartX=53.1308 StartY=25.1242 StartZ=0 EndX=54.1775 EndY=25.0413 EndZ=0
    g100: LineSegment StartX=54.1775 StartY=25.0413 StartZ=0 EndX=55.2324 EndY=25.0135 EndZ=0
    g101: LineSegment StartX=55.2324 StartY=25.0135 StartZ=0 EndX=59.3852 EndY=25.0135 EndZ=0
    g102: LineSegment StartX=59.3852 StartY=25.0135 StartZ=0 EndX=59.3852 EndY=15.0135 EndZ=0
    g103: LineSegment StartX=59.3852 StartY=15.0135 StartZ=0 EndX=79.3852 EndY=15.0135 EndZ=0
    g104: LineSegment StartX=79.3852 StartY=15.0135 StartZ=0 EndX=79.3852 EndY=-14.9865 EndZ=0
    g105: LineSegment StartX=79.3852 StartY=-14.9865 StartZ=0 EndX=59.3852 EndY=-14.9865 EndZ=0
    g106: LineSegment StartX=59.3852 StartY=-14.9865 StartZ=0 EndX=59.3852 EndY=-24.9865 EndZ=0
    g107: LineSegment StartX=59.3852 StartY=-24.9865 StartZ=0 EndX=55.2324 EndY=-24.9865 EndZ=0
    g108: LineSegment StartX=55.2324 StartY=-24.9865 StartZ=0 EndX=54.1775 EndY=-25.0143 EndZ=0
    g109: LineSegment StartX=54.1775 StartY=-25.0143 StartZ=0 EndX=53.1308 EndY=-25.0971 EndZ=0
    g110: LineSegment StartX=53.1308 StartY=-25.0971 StartZ=0 EndX=52.0941 EndY=-25.2341 EndZ=0
    g111: LineSegment StartX=52.0941 StartY=-25.2341 StartZ=0 EndX=51.0693 EndY=-25.4244 EndZ=0
    g112: LineSegment StartX=51.0693 StartY=-25.4244 StartZ=0 EndX=50.0585 EndY=-25.6672 EndZ=0
    g113: LineSegment StartX=50.0585 StartY=-25.6672 StartZ=0 EndX=49.0636 EndY=-25.9615 EndZ=0
    g114: LineSegment StartX=49.0636 StartY=-25.9615 StartZ=0 EndX=48.0866 EndY=-26.3066 EndZ=0
    g115: LineSegment StartX=48.0866 StartY=-26.3066 StartZ=0 EndX=47.1293 EndY=-26.7015 EndZ=0
    g116: LineSegment StartX=47.1293 StartY=-26.7015 StartZ=0 EndX=46.1937 EndY=-27.1454 EndZ=0
    g117: LineSegment StartX=46.1937 StartY=-27.1454 StartZ=0 EndX=45.2817 EndY=-27.6375 EndZ=0
    g118: LineSegment StartX=45.2817 StartY=-27.6375 StartZ=0 EndX=44.3954 EndY=-28.1768 EndZ=0
    g119: LineSegment StartX=44.3954 StartY=-28.1768 StartZ=0 EndX=43.5366 EndY=-28.7626 EndZ=0
    g120: LineSegment StartX=43.5366 StartY=-28.7626 StartZ=0 EndX=42.7073 EndY=-29.3939 EndZ=0
    g121: LineSegment StartX=42.7073 StartY=-29.3939 StartZ=0 EndX=41.9095 EndY=-30.0699 EndZ=0
    g122: LineSegment StartX=41.9095 StartY=-30.0699 StartZ=0 EndX=41.145 EndY=-30.7897 EndZ=0
    g123: LineSegment StartX=41.145 StartY=-30.7897 StartZ=0 EndX=40.4159 EndY=-31.5525 EndZ=0
    g124: LineSegment StartX=40.4159 StartY=-31.5525 StartZ=0 EndX=35.5683 EndY=-36.899 EndZ=0
    g125: LineSegment StartX=35.5683 StartY=-36.899 StartZ=0 EndX=35.386 EndY=-37.0897 EndZ=0
    g126: LineSegment StartX=35.386 StartY=-37.0897 StartZ=0 EndX=35.1949 EndY=-37.2697 EndZ=0
    g127: LineSegment StartX=35.1949 StartY=-37.2697 StartZ=0 EndX=34.9954 EndY=-37.4387 EndZ=0
    g128: LineSegment StartX=34.9954 StartY=-37.4387 StartZ=0 EndX=34.7881 EndY=-37.5965 EndZ=0
    g129: LineSegment StartX=34.7881 StartY=-37.5965 StartZ=0 EndX=34.5734 EndY=-37.743 EndZ=0
    g130: LineSegment StartX=34.5734 StartY=-37.743 StartZ=0 EndX=34.3518 EndY=-37.8778 EndZ=0
    g131: LineSegment StartX=34.3518 StartY=-37.8778 StartZ=0 EndX=34.1238 EndY=-38.0008 EndZ=0
    g132: LineSegment StartX=34.1238 StartY=-38.0008 StartZ=0 EndX=33.8899 EndY=-38.1118 EndZ=0
    g133: LineSegment StartX=33.8899 StartY=-38.1118 StartZ=0 EndX=33.6506 EndY=-38.2105 EndZ=0
    g134: LineSegment StartX=33.6506 StartY=-38.2105 StartZ=0 EndX=33.4063 EndY=-38.2968 EndZ=0
    g135: LineSegment StartX=33.4063 StartY=-38.2968 StartZ=0 EndX=33.1576 EndY=-38.3704 EndZ=0
    g136: LineSegment StartX=33.1576 StartY=-38.3704 StartZ=0 EndX=32.9049 EndY=-38.4311 EndZ=0
    g137: LineSegment StartX=32.9049 StartY=-38.4311 StartZ=0 EndX=32.6487 EndY=-38.4787 EndZ=0
    g138: LineSegment StartX=32.6487 StartY=-38.4787 StartZ=0 EndX=32.3896 EndY=-38.5129 EndZ=0
    g139: LineSegment StartX=32.3896 StartY=-38.5129 StartZ=0 EndX=32.1279 EndY=-38.5336 EndZ=0
    g140: LineSegment StartX=32.1279 StartY=-38.5336 StartZ=0 EndX=31.8641 EndY=-38.5406 EndZ=0
    g141: LineSegment StartX=31.8641 StartY=-38.5406 StartZ=0 EndX=11.8641 EndY=-38.5405 EndZ=0
    g142: LineSegment StartX=11.8641 StartY=-38.5405 StartZ=0 EndX=11.6868 EndY=-38.5374 EndZ=0
    g143: LineSegment StartX=11.6868 StartY=-38.5374 StartZ=0 EndX=11.5102 EndY=-38.528 EndZ=0
    g144: LineSegment StartX=11.5102 StartY=-38.528 StartZ=0 EndX=11.3343 EndY=-38.5124 EndZ=0
    g145: LineSegment StartX=11.3343 StartY=-38.5124 StartZ=0 EndX=11.1593 EndY=-38.4906 EndZ=0
    g146: LineSegment StartX=11.1593 StartY=-38.4906 StartZ=0 EndX=10.9854 EndY=-38.4627 EndZ=0
    g147: LineSegment StartX=10.9854 StartY=-38.4627 StartZ=0 EndX=10.8127 EndY=-38.4287 EndZ=0
    g148: LineSegment StartX=10.8127 StartY=-38.4287 StartZ=0 EndX=10.6415 EndY=-38.3887 EndZ=0
    g149: LineSegment StartX=10.6415 StartY=-38.3887 StartZ=0 EndX=10.4718 EndY=-38.3428 EndZ=0
    g150: LineSegment StartX=10.4718 StartY=-38.3428 StartZ=0 EndX=10.3039 EndY=-38.2909 EndZ=0
    g151: LineSegment StartX=10.3039 StartY=-38.2909 StartZ=0 EndX=10.1378 EndY=-38.233 EndZ=0
    g152: LineSegment StartX=10.1378 StartY=-38.233 StartZ=0 EndX=9.97375 EndY=-38.1694 EndZ=0
    g153: LineSegment StartX=9.97375 StartY=-38.1694 StartZ=0 EndX=9.8119 EndY=-38.0999 EndZ=0
    g154: LineSegment StartX=9.8119 StartY=-38.0999 StartZ=0 EndX=9.65241 EndY=-38.0247 EndZ=0
    g155: LineSegment StartX=9.65241 StartY=-38.0247 StartZ=0 EndX=9.49543 EndY=-37.9438 EndZ=0
    g156: LineSegment StartX=9.49543 StartY=-37.9438 StartZ=0 EndX=9.34111 EndY=-37.8573 EndZ=0
    g157: LineSegment StartX=9.34111 StartY=-37.8573 StartZ=0 EndX=9.18963 EndY=-37.7651 EndZ=0
    g158: LineSegment StartX=9.18963 StartY=-37.7651 StartZ=0 EndX=-8.8018 EndY=-26.3748 EndZ=0
    g159: LineSegment StartX=-8.8018 StartY=-26.3748 StartZ=0 EndX=-9.40774 EndY=-26.006 EndZ=0
    g160: LineSegment StartX=-9.40774 StartY=-26.006 StartZ=0 EndX=-10.025 EndY=-25.6598 EndZ=0
    g161: LineSegment StartX=-10.025 StartY=-25.6598 StartZ=0 EndX=-10.6529 EndY=-25.3361 EndZ=0
    g162: LineSegment StartX=-10.6529 StartY=-25.3361 StartZ=0 EndX=-11.2909 EndY=-25.0353 EndZ=0
    g163: LineSegment StartX=-11.2909 StartY=-25.0353 StartZ=0 EndX=-11.9383 EndY=-24.7575 EndZ=0
    g164: LineSegment StartX=-11.9383 StartY=-24.7575 StartZ=0 EndX=-12.5944 EndY=-24.5029 EndZ=0
    g165: LineSegment StartX=-12.5944 StartY=-24.5029 StartZ=0 EndX=-13.2588 EndY=-24.2717 EndZ=0
    g166: LineSegment StartX=-13.2588 StartY=-24.2717 StartZ=0 EndX=-13.9306 EndY=-24.0641 EndZ=0
    g167: LineSegment StartX=-13.9306 StartY=-24.0641 StartZ=0 EndX=-14.6093 EndY=-23.8802 EndZ=0
    g168: LineSegment StartX=-14.6093 StartY=-23.8802 StartZ=0 EndX=-15.2943 EndY=-23.7202 EndZ=0
    g169: LineSegment StartX=-15.2943 StartY=-23.7202 StartZ=0 EndX=-15.9849 EndY=-23.5843 EndZ=0
    g170: LineSegment StartX=-15.9849 StartY=-23.5843 StartZ=0 EndX=-16.6805 EndY=-23.4727 EndZ=0
    g171: LineSegment StartX=-16.6805 StartY=-23.4727 StartZ=0 EndX=-17.3804 EndY=-23.3856 EndZ=0
    g172: LineSegment StartX=-17.3804 StartY=-23.3856 StartZ=0 EndX=-18.084 EndY=-23.3232 EndZ=0
    g173: LineSegment StartX=-18.084 StartY=-23.3232 StartZ=0 EndX=-18.7908 EndY=-23.2856 EndZ=0
    g174: LineSegment StartX=-18.7908 StartY=-23.2856 StartZ=0 EndX=-19.5 EndY=-23.273 EndZ=0
    g175: LineSegment StartX=-19.5 StartY=-23.273 StartZ=0 EndX=-81.0081 EndY=-23.273 EndZ=0
    g176: LineSegment StartX=-81.0081 StartY=-23.273 StartZ=0 EndX=-83.0257 EndY=-23.2417 EndZ=0
    g177: LineSegment StartX=-83.0257 StartY=-23.2417 StartZ=0 EndX=-85.0378 EndY=-23.148 EndZ=0
    g178: LineSegment StartX=-85.0378 StartY=-23.148 StartZ=0 EndX=-87.0433 EndY=-22.9923 EndZ=0
    g179: LineSegment StartX=-87.0433 StartY=-22.9923 StartZ=0 EndX=-89.0406 EndY=-22.775 EndZ=0
    g180: LineSegment StartX=-89.0406 StartY=-22.775 StartZ=0 EndX=-91.0284 EndY=-22.4963 EndZ=0
    g181: LineSegment StartX=-91.0284 StartY=-22.4963 StartZ=0 EndX=-93.0052 EndY=-22.1567 EndZ=0
    g182: LineSegment StartX=-93.0052 StartY=-22.1567 StartZ=0 EndX=-94.9697 EndY=-21.7564 EndZ=0
    g183: LineSegment StartX=-94.9697 StartY=-21.7564 StartZ=0 EndX=-96.9205 EndY=-21.2959 EndZ=0
    g184: LineSegment StartX=-96.9205 StartY=-21.2959 StartZ=0 EndX=-98.8562 EndY=-20.7756 EndZ=0
    g185: LineSegment StartX=-98.8562 StartY=-20.7756 StartZ=0 EndX=-100.775 EndY=-20.1956 EndZ=0
    g186: LineSegment StartX=-100.775 StartY=-20.1956 StartZ=0 EndX=-102.677 EndY=-19.5565 EndZ=0
    g187: LineSegment StartX=-102.677 StartY=-19.5565 StartZ=0 EndX=-104.559 EndY=-18.8585 EndZ=0
    g188: LineSegment StartX=-104.559 StartY=-18.8585 StartZ=0 EndX=-106.42 EndY=-18.102 EndZ=0
    g189: LineSegment StartX=-106.42 StartY=-18.102 StartZ=0 EndX=-108.259 EndY=-17.2874 EndZ=0
    g190: LineSegment StartX=-108.259 StartY=-17.2874 StartZ=0 EndX=-110.075 EndY=-16.415 EndZ=0
    g191: LineSegment StartX=-110.075 StartY=-16.415 StartZ=0 EndX=-111.865 EndY=-15.4851 EndZ=0
    g192: LineSegment StartX=-111.865 StartY=-15.4851 StartZ=0 EndX=-136.264 EndY=-2.33178 EndZ=0
    g193: LineSegment StartX=-136.264 StartY=-2.33178 StartZ=0 EndX=-136.344 EndY=-2.28693 EndZ=0
    g194: LineSegment StartX=-136.344 StartY=-2.28693 StartZ=0 EndX=-136.422 EndY=-2.2396 EndZ=0
    g195: LineSegment StartX=-136.422 StartY=-2.2396 StartZ=0 EndX=-136.498 EndY=-2.18984 EndZ=0
    g196: LineSegment StartX=-136.498 StartY=-2.18984 StartZ=0 EndX=-136.572 EndY=-2.13773 EndZ=0
    g197: LineSegment StartX=-136.572 StartY=-2.13773 StartZ=0 EndX=-136.644 EndY=-2.08332 EndZ=0
    g198: LineSegment StartX=-136.644 StartY=-2.08332 StartZ=0 EndX=-136.714 EndY=-2.02669 EndZ=0
    g199: LineSegment StartX=-136.714 StartY=-2.02669 StartZ=0 EndX=-136.781 EndY=-1.96789 EndZ=0
    g200: LineSegment StartX=-136.781 StartY=-1.96789 StartZ=0 EndX=-136.847 EndY=-1.907 EndZ=0
    g201: LineSegment StartX=-136.847 StartY=-1.907 StartZ=0 EndX=-136.91 EndY=-1.84407 EndZ=0
    g202: LineSegment StartX=-136.91 StartY=-1.84407 StartZ=0 EndX=-136.971 EndY=-1.77918 EndZ=0
    g203: LineSegment StartX=-136.971 StartY=-1.77918 StartZ=0 EndX=-137.03 EndY=-1.7124 EndZ=0
    g204: LineSegment StartX=-137.03 StartY=-1.7124 StartZ=0 EndX=-137.086 EndY=-1.64377 EndZ=0
    g205: LineSegment StartX=-137.086 StartY=-1.64377 StartZ=0 EndX=-137.14 EndY=-1.57338 EndZ=0
    g206: LineSegment StartX=-137.14 StartY=-1.57338 StartZ=0 EndX=-137.192 EndY=-1.50128 EndZ=0
    g207: LineSegment StartX=-137.192 StartY=-1.50128 StartZ=0 EndX=-137.241 EndY=-1.42754 EndZ=0
    g208: LineSegment StartX=-137.241 StartY=-1.42754 StartZ=0 EndX=-137.288 EndY=-1.35223 EndZ=0
    g209: LineSegment StartX=-137.288 StartY=-1.35223 StartZ=0 EndX=-137.332 EndY=-1.27541 EndZ=0
    g210: LineSegment StartX=-137.332 StartY=-1.27541 StartZ=0 EndX=-137.374 EndY=-1.19715 EndZ=0
    g211: LineSegment StartX=-137.374 StartY=-1.19715 StartZ=0 EndX=-137.413 EndY=-1.11751 EndZ=0
    g212: LineSegment StartX=-137.413 StartY=-1.11751 StartZ=0 EndX=-137.449 EndY=-1.03656 EndZ=0
    g213: LineSegment StartX=-137.449 StartY=-1.03656 StartZ=0 EndX=-137.483 EndY=-0.954362 EndZ=0
    g214: LineSegment StartX=-137.483 StartY=-0.954362 StartZ=0 EndX=-137.513 EndY=-0.870982 EndZ=0
    g215: LineSegment StartX=-137.513 StartY=-0.870982 StartZ=0 EndX=-137.542 EndY=-0.786484 EndZ=0
    g216: LineSegment StartX=-137.542 StartY=-0.786484 StartZ=0 EndX=-137.567 EndY=-0.700936 EndZ=0
    g217: LineSegment StartX=-137.567 StartY=-0.700936 StartZ=0 EndX=-137.59 EndY=-0.614402 EndZ=0
    g218: LineSegment StartX=-137.59 StartY=-0.614402 StartZ=0 EndX=-137.609 EndY=-0.526948 EndZ=0
    g219: LineSegment StartX=-137.609 StartY=-0.526948 StartZ=0 EndX=-137.626 EndY=-0.438638 EndZ=0
    g220: LineSegment StartX=-137.626 StartY=-0.438638 StartZ=0 EndX=-137.64 EndY=-0.349538 EndZ=0
    g221: LineSegment StartX=-137.64 StartY=-0.349538 StartZ=0 EndX=-137.651 EndY=-0.259715 EndZ=0
    g222: LineSegment StartX=-137.651 StartY=-0.259715 StartZ=0 EndX=-137.658 EndY=-0.169231 EndZ=0
    g223: LineSegment StartX=-137.658 StartY=-0.169231 StartZ=0 EndX=-137.663 EndY=-0.078154 EndZ=0
    g224: LineSegment StartX=-137.663 StartY=-0.078154 StartZ=0 EndX=-137.665 EndY=0.013451 EndZ=0
  constraints (224):
    c: Coincident(g222,g223)
    c: Coincident(g223,g224)
    c: Coincident(g0,g224)
    c: Coincident(g0,g1)
    c: Coincident(g220,g221)
    c: Coincident(g1,g2)
    c: Coincident(g219,g220)
    c: Coincident(g218,g219)
    c: Coincident(g2,g3)
    c: Coincident(g217,g218)
    c: Coincident(g216,g217)
    c: Coincident(g3,g4)
    c: Coincident(g215,g216)
    c: Coincident(g214,g215)
    c: Coincident(g4,g5)
    c: Coincident(g213,g214)
    c: Coincident(g212,g213)
    c: Coincident(g5,g6)
    c: Coincident(g211,g212)
    c: Coincident(g210,g211)
    c: Coincident(g6,g7)
    c: Coincident(g209,g210)
    c: Coincident(g208,g209)
    c: Coincident(g7,g8)
    c: Coincident(g207,g208)
    c: Coincident(g206,g207)
    c: Coincident(g8,g9)
    c: Coincident(g205,g206)
    c: Coincident(g204,g205)
    c: Coincident(g9,g10)
    c: Coincident(g203,g204)
    c: Coincident(g202,g203)
    c: Coincident(g10,g11)
    c: Coincident(g201,g202)
    c: Coincident(g200,g201)
    c: Coincident(g11,g12)
    c: Coincident(g199,g200)
    c: Coincident(g198,g199)
    c: Coincident(g12,g13)
    c: Coincident(g197,g198)
    c: Coincident(g196,g197)
    c: Coincident(g13,g14)
    c: Coincident(g195,g196)
    c: Coincident(g194,g195)
    c: Coincident(g14,g15)
    c: Coincident(g193,g194)
    c: Coincident(g192,g193)
    c: Coincident(g15,g16)
    c: Coincident(g191,g192)
    c: Coincident(g190,g191)
    c: Coincident(g16,g17)
    c: Coincident(g17,g18)
    c: Coincident(g189,g190)
    c: Coincident(g18,g19)
    c: Coincident(g188,g189)
    c: Coincident(g19,g20)
    c: Coincident(g187,g188)
    c: Coincident(g20,g21)
    c: Coincident(g186,g187)
    c: Coincident(g21,g22)
    c: Coincident(g185,g186)
    c: Coincident(g22,g23)
    c: Coincident(g184,g185)
    c: Coincident(g23,g24)
    c: Coincident(g24,g25)
    c: Coincident(g183,g184)
    c: Coincident(g25,g26)
    c: Coincident(g182,g183)
    c: Coincident(g26,g27)
    c: Coincident(g181,g182)
    c: Coincident(g27,g28)
    c: Coincident(g180,g181)
    c: Coincident(g28,g29)
    c: Coincident(g179,g180)
    c: Coincident(g29,g30)
    c: Coincident(g178,g179)
    c: Coincident(g30,g31)
    c: Coincident(g177,g178)
    c: Coincident(g31,g32)
    c: Coincident(g32,g33)
    c: Coincident(g176,g177)
    c: Coincident(g175,g176)
    c: Coincident(g174,g175)
    c: Coincident(g33,g34)
    c: Coincident(g173,g174)
    c: Coincident(g34,g35)
    c: Coincident(g172,g173)
    c: Coincident(g35,g36)
    c: Coincident(g171,g172)
    c: Coincident(g36,g37)
    c: Coincident(g170,g171)
    c: Coincident(g37,g38)
    c: Coincident(g169,g170)
    c: Coincident(g38,g39)
    c: Coincident(g168,g169)
    c: Coincident(g39,g40)
    c: Coincident(g167,g168)
    c: Coincident(g40,g41)
    c: Coincident(g166,g167)
    c: Coincident(g41,g42)
    c: Coincident(g165,g166)
    c: Coincident(g42,g43)
    c: Coincident(g164,g165)
    c: Coincident(g43,g44)
    c: Coincident(g163,g164)
    c: Coincident(g44,g45)
    c: Coincident(g162,g163)
    c: Coincident(g45,g46)
    c: Coincident(g161,g162)
    c: Coincident(g46,g47)
    c: Coincident(g160,g161)
    c: Coincident(g47,g48)
    c: Coincident(g159,g160)
    c: Coincident(g48,g49)
    c: Coincident(g158,g159)
    c: Coincident(g49,g50)
    c: Coincident(g157,g158)
    c: Coincident(g50,g51)
    c: Coincident(g156,g157)
    c: Coincident(g51,g52)
    c: Coincident(g155,g156)
    c: Coincident(g52,g53)
    c: Coincident(g154,g155)
    c: Coincident(g53,g54)
    c: Coincident(g153,g154)
    c: Coincident(g54,g55)
    c: Coincident(g152,g153)
    c: Coincident(g55,g56)
    c: Coincident(g151,g152)
    c: Coincident(g56,g57)
    c: Coincident(g150,g151)
    c: Coincident(g57,g58)
    c: Coincident(g149,g150)
    c: Coincident(g58,g59)
    c: Coincident(g148,g149)
    c: Coincident(g59,g60)
    c: Coincident(g147,g148)
    c: Coincident(g60,g61)
    c: Coincident(g146,g147)
    c: Coincident(g61,g62)
    c: Coincident(g145,g146)
    c: Coincident(g62,g63)
    c: Coincident(g144,g145)
    c: Coincident(g63,g64)
    c: Coincident(g143,g144)
    c: Coincident(g64,g65)
    c: Coincident(g142,g143)
    c: Coincident(g65,g66)
    c: Coincident(g141,g142)
    c: Coincident(g66,g67)
    c: Coincident(g140,g141)
    c: Coincident(g67,g68)
    c: Coincident(g139,g140)
    c: Coincident(g68,g69)
    c: Coincident(g138,g139)
    c: Coincident(g69,g70)
    c: Coincident(g137,g138)
    c: Coincident(g70,g71)
    c: Coincident(g136,g137)
    c: Coincident(g71,g72)
    c: Coincident(g135,g136)
    c: Coincident(g72,g73)
    c: Coincident(g134,g135)
    c: Coincident(g73,g74)
    c: Coincident(g133,g134)
    c: Coincident(g74,g75)
    c: Coincident(g132,g133)
    c: Coincident(g75,g76)
    c: Coincident(g131,g132)
    c: Coincident(g76,g77)
    c: Coincident(g130,g131)
    c: Coincident(g77,g78)
    c: Coincident(g129,g130)
    c: Coincident(g78,g79)
    c: Coincident(g128,g129)
    c: Coincident(g79,g80)
    c: Coincident(g127,g128)
    c: Coincident(g80,g81)
    c: Coincident(g126,g127)
    c: Coincident(g81,g82)
    c: Coincident(g125,g126)
    c: Coincident(g82,g83)
    c: Coincident(g124,g125)
    c: Coincident(g83,g84)
    c: Coincident(g123,g124)
    c: Coincident(g84,g85)
    c: Coincident(g122,g123)
    c: Coincident(g85,g86)
    c: Coincident(g121,g122)
    c: Coincident(g86,g87)
    c: Coincident(g120,g121)
    c: Coincident(g87,g88)
    c: Coincident(g119,g120)
    c: Coincident(g88,g89)
    c: Coincident(g118,g119)
    c: Coincident(g89,g90)
    c: Coincident(g117,g118)
    c: Coincident(g90,g91)
    c: Coincident(g116,g117)
    c: Coincident(g91,g92)
    c: Coincident(g115,g116)
    c: Coincident(g92,g93)
    c: Coincident(g114,g115)
    c: Coincident(g93,g94)
    c: Coincident(g113,g114)
    c: Coincident(g94,g95)
    c: Coincident(g112,g113)
    c: Coincident(g95,g96)
    c: Coincident(g111,g112)
    c: Coincident(g96,g97)
    c: Coincident(g110,g111)
    c: Coincident(g97,g98)
    c: Coincident(g109,g110)
    c: Coincident(g98,g99)
    c: Coincident(g108,g109)
    c: Coincident(g99,g100)
    c: Coincident(g107,g108)
    c: Coincident(g100,g101)
    c: Coincident(g106,g107)
    c: Coincident(g105,g106)
    c: Coincident(g102,g103)
    c: Coincident(g101,g102)
    c: Coincident(g104,g105)
    c: Coincident(g103,g104)
FEATURE [App::Part] Board_Geoms_259c
  Group = -> [Pcb_259c,PCB_Sketch_259c]
  Origin = -> Origin006
FEATURE [Part::Feature] Part__Feature  label="ESP32-S3-WROOM-1"
  shape: bbox 15 x 5.5 x 0.2 mm, 30 faces (baked)
FEATURE [Part::Feature] Part__Feature001  label="ESP32-S3-WROOM-002"
  shape: bbox 18 x 25.5 x 0.8 mm, 451 faces (baked)
FEATURE [Part::Feature] Part__Feature002  label="ESP32-S3-WROOM-003"
  shape: bbox 15.8 x 17.6 x 2.3 mm, 20 faces (baked)
FEATURE [Part::Feature] Part__Feature003  label="ESP32-S3-WROOM-004"
  shape: bbox 0.85 x 0.9 x 0.8 mm, 18 faces (baked)
FEATURE [Part::Feature] Part__Feature004  label="ESP32-S3-WROOM-005"
  shape: bbox 0.85 x 0.9 x 0.8 mm, 18 faces (baked)
FEATURE [Part::Feature] Part__Feature005  label="ESP32-S3-WROOM-006"
  shape: bbox 0.85 x 0.9 x 0.8 mm, 18 faces (baked)
FEATURE [Part::Feature] Part__Feature006  label="ESP32-S3-WROOM-007"
  shape: bbox 0.85 x 0.9 x 0.8 mm, 18 faces (baked)
FEATURE [Part::Feature] Part__Feature007  label="ESP32-S3-WROOM-008"
  shape: bbox 0.85 x 0.9 x 0.8 mm, 18 faces (baked)
FEATURE [Part::Feature] Part__Feature008  label="ESP32-S3-WROOM-009"
  shape: bbox 0.85 x 0.9 x 0.8 mm, 18 faces (baked)
FEATURE [Part::Feature] Part__Feature009  label="ESP32-S3-WROOM-010"
  shape: bbox 0.85 x 0.9 x 0.8 mm, 18 faces (baked)
FEATURE [Part::Feature] Part__Feature010  label="ESP32-S3-WROOM-011"
  shape: bbox 0.85 x 0.9 x 0.8 mm, 18 faces (baked)
FEATURE [Part::Feature] Part__Feature011  label="ESP32-S3-WROOM-012"
  shape: bbox 0.85 x 0.9 x 0.8 mm, 18 faces (baked)
FEATURE [Part::Feature] Part__Feature012  label="ESP32-S3-WROOM-013"
  shape: bbox 0.85 x 0.9 x 0.8 mm, 18 faces (baked)
FEATURE [Part::Feature] Part__Feature013  label="ESP32-S3-WROOM-014"
  shape: bbox 0.85 x 0.9 x 0.8 mm, 18 faces (baked)
FEATURE [Part::Feature] Part__Feature014  label="ESP32-S3-WROOM-015"
  shape: bbox 0.85 x 0.9 x 0.8 mm, 18 faces (baked)
FEATURE [Part::Feature] Part__Feature015  label="ESP32-S3-WROOM-016"
  shape: bbox 0.85 x 0.9 x 0.8 mm, 18 faces (baked)
FEATURE [Part::Feature] Part__Feature016  label="ESP32-S3-WROOM-017"
  shape: bbox 0.9 x 0.85 x 0.8 mm, 18 faces (baked)
FEATURE [Part::Feature] Part__Feature017  label="ESP32-S3-WROOM-018"
  shape: bbox 0.9 x 0.85 x 0.8 mm, 18 faces (baked)
FEATURE [Part::Feature] Part__Feature018  label="ESP32-S3-WROOM-019"
  shape: bbox 0.9 x 0.85 x 0.8 mm, 18 faces (baked)
FEATURE [Part::Feature] Part__Feature019  label="ESP32-S3-WROOM-020"
  shape: bbox 0.9 x 0.85 x 0.8 mm, 18 faces (baked)
FEATURE [Part::Feature] Part__Feature020  label="ESP32-S3-WROOM-021"
  shape: bbox 0.9 x 0.85 x 0.8 mm, 18 faces (baked)
FEATURE [Part::Feature] Part__Feature021  label="ESP32-S3-WROOM-022"
  shape: bbox 0.9 x 0.85 x 0.8 mm, 18 faces (baked)
FEATURE [Part::Feature] Part__Feature022  label="ESP32-S3-WROOM-023"
  shape: bbox 0.85 x 0.9 x 0.8 mm, 18 faces (baked)
FEATURE [Part::Feature] Part__Feature023  label="ESP32-S3-WROOM-024"
  shape: bbox 0.85 x 0.9 x 0.8 mm, 18 faces (baked)
FEATURE [Part::Feature] Part__Feature024  label="ESP32-S3-WROOM-025"
  shape: bbox 0.85 x 0.9 x 0.8 mm, 18 faces (baked)
FEATURE [Part::Feature] Part__Feature025  label="ESP32-S3-WROOM-026"
  shape: bbox 0.85 x 0.9 x 0.8 mm, 18 faces (baked)
FEATURE [Part::Feature] Part__Feature026  label="ESP32-S3-WROOM-027"
  shape: bbox 0.85 x 0.9 x 0.8 mm, 18 faces (baked)
FEATURE [Part::Feature] Part__Feature027  label="ESP32-S3-WROOM-028"
  shape: bbox 0.85 x 0.9 x 0.8 mm, 18 faces (baked)
FEATURE [Part::Feature] Part__Feature028  label="ESP32-S3-WROOM-029"
  shape: bbox 0.85 x 0.9 x 0.8 mm, 18 faces (baked)
FEATURE [Part::Feature] Part__Feature029  label="ESP32-S3-WROOM-030"
  shape: bbox 0.85 x 0.9 x 0.8 mm, 18 faces (baked)
FEATURE [Part::Feature] Part__Feature030  label="ESP32-S3-WROOM-031"
  shape: bbox 0.85 x 0.9 x 0.8 mm, 18 faces (baked)
FEATURE [Part::Feature] Part__Feature031  label="ESP32-S3-WROOM-032"
  shape: bbox 0.85 x 0.9 x 0.8 mm, 18 faces (baked)
FEATURE [Part::Feature] Part__Feature032  label="ESP32-S3-WROOM-033"
  shape: bbox 0.85 x 0.9 x 0.8 mm, 18 faces (baked)
FEATURE [Part::Feature] Part__Feature033  label="ESP32-S3-WROOM-034"
  shape: bbox 0.85 x 0.9 x 0.8 mm, 18 faces (baked)
FEATURE [Part::Feature] Part__Feature034  label="ESP32-S3-WROOM-035"
  shape: bbox 0.85 x 0.9 x 0.8 mm, 18 faces (baked)
FEATURE [Part::Feature] Part__Feature035  label="ESP32-S3-WROOM-036"
  shape: bbox 0.85 x 0.9 x 0.8 mm, 18 faces (baked)
FEATURE [Part::Feature] Part__Feature036  label="ESP32-S3-WROOM-037"
  shape: bbox 0.9 x 0.85 x 0.8 mm, 18 faces (baked)
FEATURE [Part::Feature] Part__Feature037  label="ESP32-S3-WROOM-038"
  shape: bbox 0.9 x 0.85 x 0.8 mm, 18 faces (baked)
FEATURE [Part::Feature] Part__Feature038  label="ESP32-S3-WROOM-039"
  shape: bbox 0.9 x 0.85 x 0.8 mm, 18 faces (baked)
FEATURE [Part::Feature] Part__Feature039  label="ESP32-S3-WROOM-040"
  shape: bbox 0.9 x 0.85 x 0.8 mm, 18 faces (baked)
FEATURE [Part::Feature] Part__Feature040  label="ESP32-S3-WROOM-041"
  shape: bbox 0.9 x 0.85 x 0.8 mm, 18 faces (baked)
FEATURE [Part::Feature] Part__Feature041  label="ESP32-S3-WROOM-042"
  shape: bbox 0.9 x 0.85 x 0.8 mm, 18 faces (baked)
FEATURE [Part::Feature] Part__Feature042  label="ESP32-S3-WROOM-043"
  shape: bbox 0.85 x 0.9 x 0.8 mm, 18 faces (baked)
FEATURE [Part::Feature] Part__Feature043  label="ESP32-S3-WROOM-044"
  shape: bbox 0.9 x 0.9 x 0.4 mm, 6 faces (baked)
FEATURE [Part::Feature] Part__Feature044  label="ESP32-S3-WROOM-045"
  shape: bbox 0.9 x 0.9 x 0.4 mm, 6 faces (baked)
FEATURE [Part::Feature] Part__Feature045  label="ESP32-S3-WROOM-046"
  shape: bbox 0.9 x 0.9 x 0.4 mm, 6 faces (baked)
FEATURE [Part::Feature] Part__Feature046  label="ESP32-S3-WROOM-047"
  shape: bbox 0.9 x 0.9 x 0.4 mm, 6 faces (baked)
FEATURE [Part::Feature] Part__Feature047  label="ESP32-S3-WROOM-048"
  shape: bbox 0.9 x 0.9 x 0.4 mm, 6 faces (baked)
FEATURE [Part::Feature] Part__Feature048  label="ESP32-S3-WROOM-049"
  shape: bbox 0.9 x 0.9 x 0.4 mm, 6 faces (baked)
FEATURE [Part::Feature] Part__Feature049  label="ESP32-S3-WROOM-050"
  shape: bbox 0.9 x 0.9 x 0.4 mm, 6 faces (baked)
FEATURE [Part::Feature] Part__Feature050  label="ESP32-S3-WROOM-051"
  shape: bbox 0.9 x 0.9 x 0.4 mm, 6 faces (baked)
FEATURE [Part::Feature] Part__Feature051  label="ESP32-S3-WROOM-052"
  shape: bbox 0.9 x 0.9 x 0.4 mm, 6 faces (baked)
FEATURE [App::Part] ESP32_S3_WROOM_1  label="U1_ESP32-S3-WROOM-053_c624d21733e4"
  Group = -> [Part__Feature,Part__Feature001,Part__Feature002,Part__Feature003,Part__Feature004,Part__Feature005,Part__Feature006,Part__Feature007,Part__Feature008,Part__Feature009,Part__Feature010,Part__Feature011,Part__Feature012,Part__Feature013,Part__Feature014,Part__Feature015,Part__Feature016,Part__Feature017,Part__Feature018,Part__Feature019,Part__Feature020,Part__Feature021,Part__Feature022,+29 more]
  Origin = -> Origin014
  Placement = pos=(22.3,31.76,0) rot=(0,0,1;0rad)
FEATURE [Part::Feature] Shape  label="C19_C_0805_2012Metric_26fd48477d25"
  Placement = pos=(18.4125,0.6,0) rot=(0,0,1;0rad)
  shape: bbox 2 x 1.25 x 1.25 mm, 28 faces (baked)
FEATURE [Part::Feature] Shape001  label="J10_PinHeader_1x05_P254mm_Vertical_dc3fed828ccc"
  Placement = pos=(39.6,26.5,0) rot=(0,0,1;0rad)
  shape: bbox 2.54 x 12.7 x 11.54 mm, 124 faces (baked)
FEATURE [Part::Feature] Shape002  label="R5_R_0805_2012Metric_788835a672ef"
  Placement = pos=(33.9,35.6,0) rot=(0,0,-1;1.5708rad)
  shape: bbox 1.2 x 2 x 0.45 mm, 26 faces (baked)
FEATURE [Part::Feature] Shape003  label="J7_PinHeader_2x03_P254mm_Vertical_023641c5d71e"
  Placement = pos=(-14.1,2.53852,0) rot=(0,0,1;0rad)
  shape: bbox 5.08 x 7.62 x 11.54 mm, 130 faces (baked)
FEATURE [Part::Feature] Shape004  label="C8_C_0805_2012Metric_9741fdc80887"
  Placement = pos=(-52.7,-2.7,0) rot=(0,0,1;0rad)
  shape: bbox 2 x 1.25 x 1.25 mm, 28 faces (baked)
FEATURE [Part::Feature] Shape005  label="D1_D_0805_cce9275b7e79"
  Placement = pos=(19.1,-17.65,0) rot=(0,0,1;0rad)
  shape: bbox 2 x 1.27 x 0.8 mm, 39 faces (baked)
FEATURE [Part::Feature] Shape006  label="C21_C_0805_2012Metric_e03d09828eb5"
  Placement = pos=(10.8,-13.4,0) rot=(0,0,-1;1.5708rad)
  shape: bbox 1.25 x 2 x 1.25 mm, 28 faces (baked)
FEATURE [Part::Feature] Shape007  label="C22_C_0805_2012Metric_1ce2ee12faa2"
  Placement = pos=(-0.3,-17.1,0) rot=(0,0,1;1.5708rad)
  shape: bbox 1.25 x 2 x 1.25 mm, 28 faces (baked)
FEATURE [Part::Feature] Shape008  label="C4_C_0805_2012Metric_5c24b972b890"
  Placement = pos=(-52.73,5.37,0) rot=(0,0,1;1.5708rad)
  shape: bbox 1.25 x 2 x 1.25 mm, 28 faces (baked)
FEATURE [Part::Feature] Shape009  label="RN1_R_Array_Convex_4x0603_1acbb4c46aad"
  Placement = pos=(-7,22.9,0) rot=(0,0,1;0rad)
  shape: bbox 1.6 x 3.2 x 0.5 mm, 206 faces (baked)
FEATURE [Part::Feature] Shape010  label="Q2_SOT_23_d12cdb4fd70f"
  Placement = pos=(21.1375,-13.55,0) rot=(0,0,1;0rad)
  shape: bbox 2.5 x 3 x 1.2 mm, 76 faces (baked)
FEATURE [Part::Feature] Shape011  label="J6_Molex_53261_0471_3f66be4bf628"
  Placement = pos=(48.625,18.55,0) rot=(0,0,1;1.5708rad)
  shape: bbox 5.2 x 10.15 x 3.4 mm, 195 faces (baked)
FEATURE [Part::Feature] Shape012  label="R1_R_0805_2012Metric_823a484d09a1"
  Placement = pos=(23.55,-17.7,0) rot=(0,0,1;0rad)
  shape: bbox 2 x 1.2 x 0.45 mm, 26 faces (baked)
FEATURE [Part::Feature] Shape013  label="C7_C_0805_2012Metric_e62b596d6a96"
  Placement = pos=(-42.5,2.95,0) rot=(0,0,1;0rad)
  shape: bbox 2 x 1.25 x 1.25 mm, 28 faces (baked)
FEATURE [Part::Feature] Shape014  label="R4_R_0805_2012Metric_ea5be46a4302"
  Placement = pos=(15.2,-31.2,0) rot=(0,0,1;3.14159rad)
  shape: bbox 2 x 1.2 x 0.45 mm, 26 faces (baked)
FEATURE [Part::Feature] Shape015  label="R7_R_0805_2012Metric_b0f0b3fe1814"
  Placement = pos=(26.9875,2.35,0) rot=(0,0,1;0rad)
  shape: bbox 2 x 1.2 x 0.45 mm, 26 faces (baked)
FEATURE [Part::Feature] Shape016  label="C23_C_0805_2012Metric_d44cc2f27c51"
  Placement = pos=(1.9,-17.1,0) rot=(0,0,1;1.5708rad)
  shape: bbox 1.25 x 2 x 1.25 mm, 28 faces (baked)
FEATURE [Part::Feature] Shape017  label="J5_PinHeader_1x08_P100mm_Vertical_d7e881798f32"
  Placement = pos=(35.6,23.2,0) rot=(0,0,1;3.14159rad)
  shape: bbox 1.27 x 8 x 7.8 mm, 196 faces (baked)
FEATURE [Part::Feature] Shape018  label="J3_Molex_53261_0271_87608ef02900"
  Placement = pos=(69.5,0,0) rot=(0,0,1;1.5708rad)
  shape: bbox 5.2 x 7.65 x 3.4 mm, 136 faces (baked)
FEATURE [Part::Feature] Shape019  label="RN4_R_Array_Convex_4x0603_d281b5a66cfe"
  Placement = pos=(24.95,13.575,0) rot=(0,0,1;0rad)
  shape: bbox 1.6 x 3.2 x 0.5 mm, 206 faces (baked)
FEATURE [Part::Feature] Shape020  label="C15_C_0805_2012Metric_8773bb8645d6"
  Placement = pos=(9.3,22.7,0) rot=(0,0,1;0rad)
  shape: bbox 2 x 1.25 x 1.25 mm, 28 faces (baked)
FEATURE [Part::Feature] Shape021  label="C14_C_0805_2012Metric_63d380e5cf47"
  Placement = pos=(4.9,-13.8,0) rot=(0,0,1;3.14159rad)
  shape: bbox 2 x 1.25 x 1.25 mm, 28 faces (baked)
FEATURE [Part::Feature] Shape022  label="C13_C_0805_2012Metric_1b100b9b5587"
  Placement = pos=(9.55,32.4,0) rot=(0,0,1;0rad)
  shape: bbox 2 x 1.25 x 1.25 mm, 28 faces (baked)
FEATURE [Part::Feature] Shape023  label="J8_Molex_53261_0471_d6c9e72b29f6"
  Placement = pos=(48.5,-18,0) rot=(0,0,1;1.5708rad)
  shape: bbox 5.2 x 10.15 x 3.4 mm, 195 faces (baked)
FEATURE [Part::Feature] Shape024  label="U4_LGA_12_2x2mm_P05mm_1f9bbc4cbc01"
  Placement = pos=(15.35,3,0) rot=(0,0,1;0rad)
  shape: bbox 2 x 2 x 1.025 mm, 68 faces (baked)
FEATURE [Part::Feature] Shape025  label="J2_PinHeader_2x03_P254mm_Vertical_de2fef7f1bf9"
  Placement = pos=(-104.24,2.53852,0) rot=(0,0,1;0rad)
  shape: bbox 5.08 x 7.62 x 11.54 mm, 130 faces (baked)
FEATURE [Part::Feature] Shape026  label="J4_PinHeader_2x03_P254mm_Vertical_2aeac4dca5ee"
  Placement = pos=(-63.92,2.53852,0) rot=(0,0,1;0rad)
  shape: bbox 5.08 x 7.62 x 11.54 mm, 130 faces (baked)
FEATURE [Part::Feature] Shape027  label="C17_C_0805_2012Metric_ed2f9a119429"
  Placement = pos=(18.4125,5.35,0) rot=(0,0,1;0rad)
  shape: bbox 2 x 1.25 x 1.25 mm, 28 faces (baked)
FEATURE [Part::Feature] Shape028  label="C3_C_0805_2012Metric_760d56f9e662"
  Placement = pos=(52.55,-1.4,0) rot=(0,0,1;0rad)
  shape: bbox 2 x 1.25 x 1.25 mm, 28 faces (baked)
FEATURE [Part::Feature] Shape029  label="R6_R_0805_2012Metric_66182406f4be"
  Placement = pos=(26.9875,5.3,0) rot=(0,0,1;0rad)
  shape: bbox 2 x 1.2 x 0.45 mm, 26 faces (baked)
FEATURE [Part::Feature] Shape030  label="C1_C_0805_2012Metric_e668bec0ee1c"
  Placement = pos=(9.45,29,0) rot=(0,0,1;0rad)
  shape: bbox 2 x 1.25 x 1.25 mm, 28 faces (baked)
FEATURE [Part::Feature] Shape031  label="R2_R_0805_2012Metric_3f8e44fbbcb6"
  Placement = pos=(12.9,-13.4,0) rot=(0,0,-1;1.5708rad)
  shape: bbox 1.2 x 2 x 0.45 mm, 26 faces (baked)
FEATURE [Part::Feature] Shape032  label="C20_C_0805_2012Metric_b540955cd545"
  Placement = pos=(9.6,-19,0) rot=(0,0,-1;1.5708rad)
  shape: bbox 1.25 x 2 x 1.25 mm, 28 faces (baked)
FEATURE [Part::Feature] Shape033  label="U6_SOT_563_0436caf67fba"
  Placement = pos=(6.4625,-16.1,0) rot=(0,0,1;0rad)
  shape: bbox 1.6 x 1.6 x 0.63 mm, 54 faces (baked)
FEATURE [Part::Feature] Shape034  label="C9_C_0805_2012Metric_3dc5c18cbf9c"
  Placement = pos=(4.9,-11.6,0) rot=(0,0,1;3.14159rad)
  shape: bbox 2 x 1.25 x 1.25 mm, 28 faces (baked)
FEATURE [Part::Feature] Shape035  label="C2_C_0805_2012Metric_1857aedbd14c"
  Placement = pos=(52.55,1.9,0) rot=(0,0,1;0rad)
  shape: bbox 2 x 1.25 x 1.25 mm, 28 faces (baked)
FEATURE [Part::Feature] Shape036  label="C16_C_0805_2012Metric_b8e457a2bea5"
  Placement = pos=(9.3,19.6,0) rot=(0,0,1;0rad)
  shape: bbox 2 x 1.25 x 1.25 mm, 28 faces (baked)
FEATURE [Part::Feature] Shape037  label="C5_C_0805_2012Metric_0fde993ad897"
  Placement = pos=(-54.98,5.37,0) rot=(0,0,1;1.5708rad)
  shape: bbox 1.25 x 2 x 1.25 mm, 28 faces (baked)
FEATURE [Part::Feature] Shape038  label="R3_R_0805_2012Metric_7e654b9285f6"
  Placement = pos=(8.7,-13.4,0) rot=(0,0,-1;1.5708rad)
  shape: bbox 1.2 x 2 x 0.45 mm, 26 faces (baked)
FEATURE [Part::Feature] Shape039  label="C18_C_0805_2012Metric_b2bf85d01791"
  Placement = pos=(18.4125,-1.55,0) rot=(0,0,1;0rad)
  shape: bbox 2 x 1.25 x 1.25 mm, 28 faces (baked)
FEATURE [Part::Feature] Shape040  label="Q1_SOT_23_dc4bbaa07a02"
  Placement = pos=(26.6,-13.5375,0) rot=(0,0,1;0rad)
  shape: bbox 2.5 x 3 x 1.2 mm, 76 faces (baked)
FEATURE [Part::Feature] Shape041  label="J9_PinHeader_1x03_P254mm_Vertical_4236c5868489"
  Placement = pos=(62.2,2.44,0) rot=(0,0,1;0rad)
  shape: bbox 2.54 x 7.62 x 11.54 mm, 76 faces (baked)
FEATURE [Part::Feature] Shape042  label="C6_C_0805_2012Metric_107644ad76d7"
  Placement = pos=(-42.5,5.1,0) rot=(0,0,1;0rad)
  shape: bbox 2 x 1.25 x 1.25 mm, 28 faces (baked)
FEATURE [Part::Feature] Shape043  label="C12_C_0805_2012Metric_f2baf2638779"
  Placement = pos=(9.55,35.41,0) rot=(0,0,1;0rad)
  shape: bbox 2 x 1.25 x 1.25 mm, 28 faces (baked)
FEATURE [App::Part] Top_259c
  Group = -> [ESP32_S3_WROOM_1,Shape,Shape001,Shape002,Shape003,Shape004,Shape005,Shape006,Shape007,Shape008,Shape009,Shape010,Shape011,Shape012,Shape013,Shape014,Shape015,Shape016,Shape017,Shape018,Shape019,Shape020,Shape021,Shape022,Shape023,Shape024,Shape025,Shape026,Shape027,Shape028,Shape029,Shape030,Shape031,Shape032,Shape033,Shape034,Shape035,Shape036,Shape037,Shape038,Shape039,Shape040,Shape041,+2 more]
  Origin = -> Origin009
FEATURE [App::Part] Step_Models_259c
  Group = -> [Top_259c]
  Origin = -> Origin008
FEATURE [App::Part] Board_259c  label="NeoSword_Kicad"
  Group = -> [Local_CS_259c,Board_Geoms_259c,Step_Models_259c]
  Origin = -> Origin007
FEATURE [PartDesign::SubShapeBinder] Binder
  BindCopyOnChange = 0
  BindMode = 0
  ClaimChildren = false
  Context = -> Part [Body002.Binder.]
  Fuse = false
  MakeFace = true
  OffsetFill = false
  OffsetIntersection = false
  OffsetJoinType = 0
  OffsetOpenResult = false
  PartialLoad = false
  Placement = pos=(0,164,0.8) rot=(0,0,1;-1.5708rad)
  Refine = true
  Relative = true
  Support = -> [Board_259c[Board_Geoms_259c.]]
  _Version = 2
FEATURE [Sketcher::SketchObject] Sketch019
  ArcFitTolerance = 1e-06
  AttachmentOffset = pos=(0,0,0.8) rot=(0,0,1;0rad)
  AttachmentSupport = -> [XY_Plane003]
  ExternalGeometry = -> [Binder]
  FullyConstrained = false
  MakeInternals = false
  MapMode = 5
  Placement = pos=(0,0,0.8) rot=(0,0,1;0rad)
  sketch-geometry (4):
    g0: LineSegment StartX=-15.4865 StartY=105.896 StartZ=0 EndX=-15.4865 EndY=84.1148 EndZ=0
    g1: LineSegment StartX=-15.4865 StartY=84.1148 StartZ=0 EndX=15.5135 EndY=84.1148 EndZ=0
    g2: LineSegment StartX=15.5135 StartY=84.1148 StartZ=0 EndX=15.5135 EndY=105.896 EndZ=0
    g3: LineSegment StartX=15.5135 StartY=105.896 StartZ=0 EndX=-15.4865 EndY=105.896 EndZ=0
  constraints (11):
    c: Coincident(g0,g1)
    c: Coincident(g1,g2)
    c: Coincident(g2,g3)
    c: Coincident(g3,g0)
    c: Vertical(g0)
    c: Vertical(g2)
    c: Horizontal(g1)
    c: Horizontal(g3)
    c: DistanceX(g0,g-4) = 0.5
    c: DistanceX(g-5,g1) = 0.5
    c: DistanceY(g1,g-5) = 0.5
FEATURE [PartDesign::Pocket] Pocket002
  BaseFeature = -> Pocket
  Direction = (0,0,-1)
  Length = 17
  Length2 = 5
  Profile = -> Sketch019
  ReferenceAxis = -> Sketch019 [N_Axis]
  Refine = true
  Suppressed = false
  Type = 0
FEATURE [Sketcher::SketchObject] Sketch020
  ArcFitTolerance = 1e-06
  AttachmentOffset = pos=(0,0,0.8) rot=(0,0,1;0rad)
  AttachmentSupport = -> [XY_Plane003]
  ExternalGeometry = -> [Binder]
  FullyConstrained = true
  MakeInternals = false
  MapMode = 5
  Placement = pos=(0,0,0.8) rot=(0,0,1;0rad)
  sketch-geometry (3):
    g0: Circle CenterX=-11.1 CenterY=94.9 CenterZ=0 NormalX=0 NormalY=0 NormalZ=1 AngleXU=0 Radius=2
    g1: Circle CenterX=11.3 CenterY=94.9 CenterZ=0 NormalX=0 NormalY=0 NormalZ=1 AngleXU=0 Radius=2
    g2: Circle CenterX=0.013518 CenterY=88.3 CenterZ=0 NormalX=0 NormalY=0 NormalZ=1 AngleXU=0 Radius=2
  constraints (6):
    c: Coincident(g0,g-3)
    c: Coincident(g1,g-4)
    c: Coincident(g2,g-5)
    c: Diameter(g0) = 4
    c: Diameter(g2) = 4
    c: Diameter(g1) = 4
FEATURE [PartDesign::Pocket] Pocket003
  BaseFeature = -> Pocket002
  Direction = (0,0,-1)
  Length = 4
  Length2 = 5
  Profile = -> Sketch020
  ReferenceAxis = -> Sketch020 [N_Axis]
  Refine = true
  Reversed = true
  Suppressed = false
  Type = 0
FEATURE [PartDesign::SubShapeBinder] Binder001
  BindCopyOnChange = 0
  BindMode = 0
  ClaimChildren = false
  Context = -> Part [Body001.Binder001.]
  Fuse = false
  MakeFace = true
  OffsetFill = false
  OffsetIntersection = false
  OffsetJoinType = 0
  OffsetOpenResult = false
  PartialLoad = false
  Refine = true
  Relative = true
  Support = -> [Body002[Binder.]]
  _Version = 2
FEATURE [Sketcher::SketchObject] Sketch021
  ArcFitTolerance = 1e-06
  AttachmentOffset = pos=(0,0,0.8) rot=(0,0,1;0rad)
  AttachmentSupport = -> [XY_Plane002]
  ExternalGeometry = -> [Binder001]
  FullyConstrained = false
  MakeInternals = false
  MapMode = 5
  Placement = pos=(0,0,0.8) rot=(0,0,1;0rad)
  sketch-geometry (4):
    g0: LineSegment StartX=-15.4865 StartY=106.312 StartZ=0 EndX=-15.4865 EndY=84.1148 EndZ=0
    g1: LineSegment StartX=-15.4865 StartY=84.1148 StartZ=0 EndX=15.5135 EndY=84.1148 EndZ=0
    g2: LineSegment StartX=15.5135 StartY=84.1148 StartZ=0 EndX=15.5135 EndY=106.312 EndZ=0
    g3: LineSegment StartX=15.5135 StartY=106.312 StartZ=0 EndX=-15.4865 EndY=106.312 EndZ=0
  constraints (11):
    c: Coincident(g0,g1)
    c: Coincident(g1,g2)
    c: Coincident(g2,g3)
    c: Coincident(g3,g0)
    c: Vertical(g0)
    c: Vertical(g2)
    c: Horizontal(g1)
    c: Horizontal(g3)
    c: DistanceY(g1,g-4) = 0.5
    c: DistanceX(g-4,g1) = 0.5
    c: DistanceX(g0,g-3) = 0.5
FEATURE [PartDesign::Pocket] Pocket004
  BaseFeature = -> Mirrored
  Direction = (0,0,-1)
  Length = 15
  Length2 = 5
  Placement = pos=(0,0,0) rot=(1,1,1;2.0944rad)
  Profile = -> Sketch021
  ReferenceAxis = -> Sketch021 [N_Axis]
  Refine = true
  Suppressed = false
  Type = 0
FEATURE [PartDesign::Body] Body001  label="Wings"
  AllowCompound = true
  Group = -> [Sketch001,Sketch002,Sketch003,AdditivePipe,Sketch004,Sketch005,Sketch006,AdditivePipe001,Sketch007,Sketch008,Sketch009,AdditivePipe002,Mirrored,Binder001,Sketch021,Pocket004]
  Origin = -> Origin002
  Tip = -> Pocket004
FEATURE [PartDesign::SubShapeBinder] Binder002  label="Blade Binder"
  BindCopyOnChange = 0
  BindMode = 0
  ClaimChildren = false
  Context = -> Part [Body.Binder002.]
  Fuse = false
  MakeFace = true
  OffsetFill = false
  OffsetIntersection = false
  OffsetJoinType = 0
  OffsetOpenResult = false
  PartialLoad = false
  Refine = true
  Relative = true
  Support = -> [Body002[Binder.]]
  _Version = 2
FEATURE [Sketcher::SketchObject] Sketch022
  ArcFitTolerance = 1e-06
  AttachmentSupport = -> [XY_Plane001]
  ExternalGeometry = -> [Binder002]
  FullyConstrained = true
  MakeInternals = false
  MapMode = 5
  sketch-geometry (4):
    g0: LineSegment StartX=-14.9865 StartY=104.615 StartZ=0 EndX=-14.9865 EndY=84.1148 EndZ=0
    g1: LineSegment StartX=-14.9865 StartY=84.1148 StartZ=0 EndX=15.0135 EndY=84.1148 EndZ=0
    g2: LineSegment StartX=15.0135 StartY=84.1148 StartZ=0 EndX=15.0135 EndY=104.615 EndZ=0
    g3: LineSegment StartX=15.0135 StartY=104.615 StartZ=0 EndX=-14.9865 EndY=104.615 EndZ=0
  constraints (11):
    c: Coincident(g0,g1)
    c: Coincident(g1,g2)
    c: Coincident(g2,g3)
    c: Coincident(g3,g0)
    c: Vertical(g0)
    c: Vertical(g2)
    c: Horizontal(g1)
    c: Horizontal(g3)
    c: Coincident(g0,g-3)
    c: Vertical(g1,g-4)
    c: DistanceY(g1,g-4) = 0.5
FEATURE [PartDesign::Pocket] Pocket005  label="Blade Cutout"
  BaseFeature = -> Pocket001
  Direction = (0,0,-1)
  Length = 16
  Length2 = 5
  Profile = -> Sketch022
  ReferenceAxis = -> Sketch022 [N_Axis]
  Refine = true
  Suppressed = false
  Type = 0
FEATURE [Sketcher::SketchObject] Sketch023
  ArcFitTolerance = 1e-06
  AttachmentOffset = pos=(0,0,-12) rot=(0,0,1;0rad)
  AttachmentSupport = -> [XY_Plane001]
  FullyConstrained = false
  MakeInternals = false
  MapMode = 5
  Placement = pos=(0,0,-12) rot=(0,0,1;0rad)
  sketch-geometry (4):
    g0: LineSegment StartX=96.2114 StartY=-112.844 StartZ=0 EndX=96.2114 EndY=110.337 EndZ=0
    g1: LineSegment StartX=96.2114 StartY=110.337 StartZ=0 EndX=-102.527 EndY=110.337 EndZ=0
    g2: LineSegment StartX=-102.527 StartY=110.337 StartZ=0 EndX=-102.527 EndY=-112.844 EndZ=0
    g3: LineSegment StartX=-102.527 StartY=-112.844 StartZ=0 EndX=96.2114 EndY=-112.844 EndZ=0
  constraints (8):
    c: Coincident(g0,g1)
    c: Coincident(g1,g2)
    c: Coincident(g2,g3)
    c: Coincident(g3,g0)
    c: Vertical(g0)
    c: Vertical(g2)
    c: Horizontal(g1)
    c: Horizontal(g3)
FEATURE [PartDesign::Pocket] Pocket006  label="Slice Door"
  BaseFeature = -> Pocket005
  Direction = (0,0,-1)
  Length = 18
  Length2 = 5
  Profile = -> Sketch023
  ReferenceAxis = -> Sketch023 [N_Axis]
  Refine = true
  Suppressed = false
  Type = 0
FEATURE [Sketcher::SketchObject] Sketch024
  ArcFitTolerance = 1e-06
  AttachmentOffset = pos=(0,0,-12) rot=(0,0,1;0rad)
  AttachmentSupport = -> [XY_Plane005]
  FullyConstrained = false
  MakeInternals = false
  MapMode = 5
  Placement = pos=(0,0,-12) rot=(0,0,1;0rad)
  sketch-geometry (4):
    g0: LineSegment StartX=-66.1141 StartY=83.0367 StartZ=0 EndX=-66.1141 EndY=-96.7387 EndZ=0
    g1: LineSegment StartX=-66.1141 StartY=-96.7387 StartZ=0 EndX=72.9518 EndY=-96.7387 EndZ=0
    g2: LineSegment StartX=72.9518 StartY=-96.7387 StartZ=0 EndX=72.9518 EndY=83.0367 EndZ=0
    g3: LineSegment StartX=72.9518 StartY=83.0367 StartZ=0 EndX=-66.1141 EndY=83.0367 EndZ=0
  constraints (8):
    c: Coincident(g0,g1)
    c: Coincident(g1,g2)
    c: Coincident(g2,g3)
    c: Coincident(g3,g0)
    c: Vertical(g0)
    c: Vertical(g2)
    c: Horizontal(g1)
    c: Horizontal(g3)
FEATURE [PartDesign::Pocket] Pocket007
  BaseFeature = -> AdditiveHelix001
  Direction = (0,0,-1)
  Length = 13
  Length2 = 5
  Placement = pos=(0,0,0) rot=(1,1,1;2.0944rad)
  Profile = -> Sketch024
  ReferenceAxis = -> Sketch024 [N_Axis]
  Refine = true
  Suppressed = false
  Type = 0
FEATURE [PartDesign::Body] Body004  label="LacesOut"
  AllowCompound = true
  Group = -> [Sketch015,Revolution001,Sketch016,Revolution002,Sketch017,AdditiveHelix,Sketch018,AdditiveHelix001,Sketch024,Pocket007]
  Origin = -> Origin005
  Tip = -> Pocket007
FEATURE [Sketcher::SketchObject] Sketch025
  ArcFitTolerance = 1e-06
  AttachmentSupport = -> [XZ_Plane015]
  FullyConstrained = false
  MakeInternals = false
  MapMode = 5
  Placement = pos=(0,0,0) rot=(1,0,0;1.5708rad)
  expr: Constraints[1] = 17.5 * 2
  sketch-geometry (9):
    g0: Circle [constr] CenterX=0 CenterY=0 CenterZ=0 NormalX=0 NormalY=0 NormalZ=1 AngleXU=0 Radius=17.5
    g1: Circle [constr] CenterX=7.3 CenterY=0 CenterZ=0 NormalX=0 NormalY=0 NormalZ=1 AngleXU=0 Radius=7.25
    g2: Circle [constr] CenterX=-7.3 CenterY=0 CenterZ=0 NormalX=0 NormalY=0 NormalZ=1 AngleXU=0 Radius=7.25
    g3: LineSegment StartX=-10 StartY=8.70069 StartZ=0 EndX=10 EndY=8.70069 EndZ=0
    g4: ArcOfCircle CenterX=-7.3 CenterY=0 CenterZ=0 NormalX=0 NormalY=0 NormalZ=1 AngleXU=0 Radius=7.3 StartAngle=0.594038 EndAngle=1.73593
    g5: ArcOfCircle CenterX=7.3 CenterY=0 CenterZ=0 NormalX=0 NormalY=0 NormalZ=1 AngleXU=0 Radius=7.3 StartAngle=1.40566 EndAngle=2.54755
    g6: LineSegment StartX=10 StartY=8.70069 StartZ=0 EndX=8.5 EndY=7.20069 EndZ=0
    g7: LineSegment StartX=-10 StartY=8.70069 StartZ=0 EndX=-8.5 EndY=7.20069 EndZ=0
    g8: ArcOfCircle CenterX=-2.333e-13 CenterY=4.93057 CenterZ=0 NormalX=0 NormalY=0 NormalZ=1 AngleXU=0 Radius=1.50911 StartAngle=3.73563 EndAngle=5.68915
  constraints (22):
    c: Coincident(g0,g-1)
    c: Diameter(g0) = 35
    c: PointOnObject(g1,g-1)
    c: Diameter(g1) = 14.5
    c: Diameter(g2) = 14.5
    c: DistanceX(g2,g0) = 7.3
    c: Symmetric(g2,g1,g-2)
    c: Coincident(g4,g2)
    c: Coincident(g5,g1)
    c: DistanceY(g5,g3) = 1.5
    c: Coincident(g6,g3)
    c: Coincident(g6,g5)
    c: Coincident(g7,g3)
    c: Coincident(g7,g4)
    c: Radius(g5) = 7.3
    c: Angle(g3,g6) = 0.785398
    c: Angle(g7,g3) = 0.785398
    c: Symmetric(g3,g3,g-2)
    c: DistanceX(g3,g-1) = 10
    c: Tangent(g4,g8) = 1.5708
    c: Tangent(g5,g8) = 1.5708
    c: Radius(g4) = 7.3
FEATURE [PartDesign::Pad] Pad001
  Direction = (0,-1,2e-16)
  Length = 100
  Length2 = 10
  Placement = pos=(0,0,0) rot=(1,0,0;1.5708rad)
  Profile = -> Sketch025
  ReferenceAxis = -> Sketch025 [N_Axis]
  Refine = true
  Suppressed = false
  Type = 0
FEATURE [Sketcher::SketchObject] Sketch026
  ArcFitTolerance = 1e-06
  AttachmentOffset = pos=(0,0,-4) rot=(0,0,1;0rad)
  AttachmentSupport = -> [XZ_Plane015]
  ExternalGeometry = -> [Pad001]
  FullyConstrained = false
  MakeInternals = false
  MapMode = 5
  Placement = pos=(0,4,-9e-16) rot=(1,0,0;1.5708rad)
  sketch-geometry (4):
    g0: LineSegment StartX=-2.44114 StartY=8.70069 StartZ=0 EndX=-2.44114 EndY=6.70069 EndZ=0
    g1: LineSegment StartX=-2.44114 StartY=6.70069 StartZ=0 EndX=2.44114 EndY=6.70069 EndZ=0
    g2: LineSegment StartX=2.44114 StartY=6.70069 StartZ=0 EndX=2.44114 EndY=8.70069 EndZ=0
    g3: LineSegment StartX=2.44114 StartY=8.70069 StartZ=0 EndX=-2.44114 EndY=8.70069 EndZ=0
  constraints (10):
    c: Coincident(g0,g1)
    c: Coincident(g1,g2)
    c: Coincident(g2,g3)
    c: Coincident(g3,g0)
    c: Vertical(g0)
    c: Vertical(g2)
    c: Horizontal(g1)
    c: PointOnObject(g0,g-3)
    c: Symmetric(g0,g2,g-2)
    c: DistanceY(g2,g2) = 2
FEATURE [PartDesign::Pad] Pad002
  BaseFeature = -> Pad001
  Direction = (0,-1,2e-16)
  Length = 109
  Length2 = 10
  Placement = pos=(0,0,0) rot=(1,0,0;1.5708rad)
  Profile = -> Sketch026
  ReferenceAxis = -> Sketch026 [N_Axis]
  Refine = true
  Suppressed = false
  Type = 0
FEATURE [PartDesign::Body] Body005  label="BatteryGuide_depricated"
  AllowCompound = true
  Group = -> [Sketch025,Pad001,Sketch026,Pad002]
  Origin = -> Origin015
  Tip = -> Pad002
FEATURE [PartDesign::SubShapeBinder] Binder003  label="Battery Roof Binder"
  BindCopyOnChange = 0
  BindMode = 0
  ClaimChildren = false
  Context = -> Part [Body.Binder003.]
  Fuse = false
  MakeFace = true
  OffsetFill = false
  OffsetIntersection = false
  OffsetJoinType = 0
  OffsetOpenResult = false
  PartialLoad = false
  Placement = pos=(0,55,0) rot=(0,0,1;0rad)
  Refine = true
  Relative = true
  Support = -> [Body005]
  _Version = 2
FEATURE [Sketcher::SketchObject] Sketch027
  ArcFitTolerance = 1e-06
  AttachmentOffset = pos=(0,0,47) rot=(0,0,1;0rad)
  AttachmentSupport = -> [XZ_Plane001]
  ExternalGeometry = -> [Pocket006,Binder003]
  FullyConstrained = false
  MakeInternals = false
  MapMode = 5
  Placement = pos=(0,-47,1.04e-14) rot=(1,0,0;1.5708rad)
  sketch-geometry (13):
    g0: Circle [constr] CenterX=-7.3 CenterY=0 CenterZ=0 NormalX=0 NormalY=0 NormalZ=1 AngleXU=0 Radius=7.25
    g1: Circle [constr] CenterX=7.3 CenterY=0 CenterZ=0 NormalX=0 NormalY=0 NormalZ=1 AngleXU=0 Radius=7.25
    g2: ArcOfCircle CenterX=-0.019986 CenterY=0.0158232 CenterZ=0 NormalX=0 NormalY=0 NormalZ=1 AngleXU=0 Radius=14.9842 StartAngle=1.56946 EndAngle=3.37438
    g3: LineSegment StartX=-14.6 StartY=-3.44093 StartZ=0 EndX=-14.6 EndY=9e-16 EndZ=0
    g4: ArcOfCircle CenterX=-7.3 CenterY=0 CenterZ=0 NormalX=0 NormalY=0 NormalZ=1 AngleXU=0 Radius=7.3 StartAngle=1.74278 EndAngle=3.14159
    g5: LineSegment StartX=-8.54929 StartY=7.19231 StartZ=0 EndX=-10.1782 EndY=8.77123 EndZ=0
    g6: LineSegment StartX=-10.1782 StartY=8.77123 StartZ=0 EndX=0 EndY=8.77123 EndZ=0
    g7: Circle [constr] CenterX=7.3 CenterY=0 CenterZ=0 NormalX=0 NormalY=0 NormalZ=1 AngleXU=0 Radius=7.25
    g8: ArcOfCircle CenterX=0.019986 CenterY=0.0158232 CenterZ=0 NormalX=0 NormalY=0 NormalZ=1 AngleXU=0 Radius=14.9842 StartAngle=6.0504 EndAngle=7.85532
    g9: LineSegment StartX=14.6 StartY=-3.44093 StartZ=0 EndX=14.6 EndY=9e-16 EndZ=0
    g10: ArcOfCircle CenterX=7.3 CenterY=0 CenterZ=0 NormalX=0 NormalY=0 NormalZ=1 AngleXU=0 Radius=7.3 StartAngle=1e-16 EndAngle=1.39881
    g11: LineSegment StartX=8.54929 StartY=7.19231 StartZ=0 EndX=10.1782 EndY=8.77123 EndZ=0
    g12: LineSegment StartX=10.1782 StartY=8.77123 StartZ=0 EndX=0 EndY=8.77123 EndZ=0
  constraints (28):
    c: PointOnObject(g0,g-1)
    c: Diameter(g1) = 14.5
    c: Diameter(g0) = 14.5
    c: Symmetric(g0,g1,g-2)
    c: DistanceX(g0,g-1) = 7.3
    c: Coincident(g3,g2)
    c: PointOnObject(g3,g-1)
    c: Tangent(g4,g3) = 1.5708
    c: PointOnObject(g2,g-3)
    c: Radius(g4) = 7.3
    c: Coincident(g0,g4)
    c: Distance(g-6,g4) = 0.05
    c: Coincident(g4,g5)
    c: Coincident(g5,g6)
    c: PointOnObject(g6,g-2)
    c: Horizontal(g6)
    c: PointOnObject(g2,g-2)
    c: PointOnObject(g2,g-3)
    c: Diameter(g7) = 14.5
    c: Coincident(g9,g8)
    c: Tangent(g10,g9) = -1.5708
    c: Radius(g10) = 7.3
    c: Coincident(g7,g10)
    c: Coincident(g10,g11)
    c: Coincident(g11,g12)
    c: Horizontal(g12)
    c: Coincident(g2,g8)
    c: Coincident(g6,g12)
FEATURE [PartDesign::Pad] Pad003  label="Battery Shape Cutout"
  BaseFeature = -> Pocket006
  Direction = (0,-1,2e-16)
  Length = 108
  Length2 = 10
  Profile = -> Sketch027
  ReferenceAxis = -> Sketch027 [N_Axis]
  Refine = true
  Reversed = true
  Suppressed = false
  Type = 0
FEATURE [Sketcher::SketchObject] Sketch028
  ArcFitTolerance = 1e-06
  AttachmentOffset = pos=(0,0,47) rot=(0,0,1;0rad)
  AttachmentSupport = -> [XZ_Plane001]
  ExternalGeometry = -> [Binder003,Pad003]
  FullyConstrained = false
  MakeInternals = false
  MapMode = 5
  Placement = pos=(0,-47,1.04e-14) rot=(1,0,0;1.5708rad)
  sketch-geometry (15):
    g0: LineSegment StartX=-2.54114 StartY=8.75069 StartZ=0 EndX=-2.54114 EndY=6.60069 EndZ=0
    g1: LineSegment StartX=-2.54114 StartY=6.60069 StartZ=0 EndX=2.54114 EndY=6.60069 EndZ=0
    g2: LineSegment StartX=2.54114 StartY=6.60069 StartZ=0 EndX=2.54114 EndY=8.75069 EndZ=0
    g3: LineSegment StartX=2.54114 StartY=8.75069 StartZ=0 EndX=-2.54114 EndY=8.75069 EndZ=0
    g4: Circle [constr] CenterX=7.3 CenterY=0 CenterZ=0 NormalX=0 NormalY=0 NormalZ=1 AngleXU=0 Radius=7.25
    g5: Circle [constr] CenterX=-7.3 CenterY=0 CenterZ=0 NormalX=0 NormalY=0 NormalZ=1 AngleXU=0 Radius=7.25
    g6: Circle [constr] CenterX=-31.1948 CenterY=-18.5655 CenterZ=0 NormalX=0 NormalY=0 NormalZ=1 AngleXU=0 Radius=7.1
    g7: ArcOfCircle CenterX=1.5452 CenterY=-4.05126 CenterZ=0 NormalX=0 NormalY=0 NormalZ=1 AngleXU=0 Radius=15 StartAngle=3.46568 EndAngle=3.70009
    g8: LineSegment StartX=-12.6739 StartY=-8.82797 StartZ=0 EndX=-13.3268 EndY=-6.88456 EndZ=0
    g9: ArcOfCircle CenterX=0 CenterY=0 CenterZ=0 NormalX=0 NormalY=0 NormalZ=1 AngleXU=0 Radius=15 StartAngle=3.61843 EndAngle=4.06889
    g10: LineSegment StartX=-9 StartY=-12 StartZ=0 EndX=-11.1756 EndY=-12 EndZ=0
    g11: ArcOfCircle CenterX=-1.5452 CenterY=-4.05126 CenterZ=0 NormalX=0 NormalY=0 NormalZ=1 AngleXU=0 Radius=15 StartAngle=5.72468 EndAngle=5.95909
    g12: LineSegment StartX=12.6739 StartY=-8.82797 StartZ=0 EndX=13.3268 EndY=-6.88456 EndZ=0
    g13: ArcOfCircle CenterX=0 CenterY=0 CenterZ=0 NormalX=0 NormalY=0 NormalZ=1 AngleXU=0 Radius=15 StartAngle=5.35589 EndAngle=5.80635
    g14: LineSegment StartX=9 StartY=-12 StartZ=0 EndX=11.1756 EndY=-12 EndZ=0
  constraints (32):
    c: Coincident(g0,g1)
    c: Coincident(g1,g2)
    c: Coincident(g2,g3)
    c: Coincident(g3,g0)
    c: Vertical(g0)
    c: Vertical(g2)
    c: Horizontal(g1)
    c: Horizontal(g3)
    c: DistanceX(g0,g-3) = 0.1
    c: DistanceX(g-4,g2) = 0.1
    c: DistanceY(g1,g-4) = 0.1
    c: DistanceY(g-4,g2) = 0.05
    c: PointOnObject(g4,g-1)
    c: Diameter(g4) = 14.5
    c: Diameter(g5) = 14.5
    c: DistanceX(g5,g-1) = 7.3
    c: Symmetric(g5,g4,g-2)
    c: Diameter(g6) = 14.2
    c: Radius(g7) = 15
    c: Horizontal(g-6,g7)
    c: PointOnObject(g8,g-5)
    c: Tangent(g8,g7) = 1.5708
    c: Coincident(g9,g-1)
    c: Coincident(g9,g8)
    c: Coincident(g9,g-5)
    c: Coincident(g10,g-5)
    c: Coincident(g10,g7)
    c: Radius(g11) = 15
    c: Tangent(g12,g11) = -1.5708
    c: Coincident(g13,g12)
    c: Coincident(g14,g11)
    c: Coincident(g13,g14)
FEATURE [PartDesign::Pocket] Pocket008  label="Battery Roof"
  BaseFeature = -> Pad003
  Direction = (0,1,-2e-16)
  Length = 103
  Length2 = 5
  Profile = -> Sketch028
  ReferenceAxis = -> Sketch028 [N_Axis]
  Refine = true
  Suppressed = false
  Type = 0
FEATURE [Sketcher::SketchObject] Sketch029
  ArcFitTolerance = 1e-06
  AttachmentOffset = pos=(0,0,56) rot=(0,0,1;0rad)
  AttachmentSupport = -> [XZ_Plane001]
  FullyConstrained = false
  MakeInternals = false
  MapMode = 5
  Placement = pos=(0,-56,1.24e-14) rot=(1,0,0;1.5708rad)
  sketch-geometry (4):
    g0: LineSegment StartX=-2.54114 StartY=8.75069 StartZ=0 EndX=-2.54114 EndY=6.60069 EndZ=0
    g1: LineSegment StartX=-2.54114 StartY=6.60069 StartZ=0 EndX=2.54114 EndY=6.60069 EndZ=0
    g2: LineSegment StartX=2.54114 StartY=6.60069 StartZ=0 EndX=2.54114 EndY=8.75069 EndZ=0
    g3: LineSegment StartX=2.54114 StartY=8.75069 StartZ=0 EndX=-2.54114 EndY=8.75069 EndZ=0
  constraints (8):
    c: Coincident(g0,g1)
    c: Coincident(g1,g2)
    c: Coincident(g2,g3)
    c: Coincident(g3,g0)
    c: Vertical(g0)
    c: Vertical(g2)
    c: Horizontal(g1)
    c: Horizontal(g3)
FEATURE [PartDesign::Pocket] Pocket009  label="Battery Roof Bar"
  BaseFeature = -> Pocket008
  Direction = (0,1,-2e-16)
  Length = 119
  Length2 = 5
  Profile = -> Sketch029
  ReferenceAxis = -> Sketch029 [N_Axis]
  Refine = true
  Suppressed = false
  Type = 0
FEATURE [Sketcher::SketchObject] Sketch030
  ArcFitTolerance = 1e-06
  AttachmentSupport = -> [XY_Plane018]
  FullyConstrained = false
  MakeInternals = false
  MapMode = 5
  sketch-geometry (15):
    g0: LineSegment StartX=17.5 StartY=50 StartZ=0 EndX=17.5 EndY=-50 EndZ=0
    g1: ArcOfCircle CenterX=27.5 CenterY=-50 CenterZ=0 NormalX=0 NormalY=0 NormalZ=1 AngleXU=0 Radius=10 StartAngle=3.14159 EndAngle=4.2478
    g2: LineSegment StartX=16.7299 StartY=-68.7091 StartZ=0 EndX=8.15223 EndY=-80.5471 EndZ=0
    g3: LineSegment StartX=8.15223 StartY=-80.5471 StartZ=0 EndX=0 EndY=-80.5471 EndZ=0
    g4: ArcOfCircle CenterX=8.2468 CenterY=-56.3383 CenterZ=0 NormalX=0 NormalY=0 NormalZ=1 AngleXU=0 Radius=15 StartAngle=5.31348 EndAngle=6.10885
    g5: ArcOfCircle CenterX=27.468 CenterY=46.0956 CenterZ=0 NormalX=0 NormalY=0 NormalZ=1 AngleXU=0 Radius=10.7054 StartAngle=1.80342 EndAngle=2.76827
    g6: LineSegment StartX=25.0001 StartY=56.5127 StartZ=0 EndX=25.0155 EndY=56.5163 EndZ=0
    g7: LineSegment StartX=25.0155 StartY=56.5163 StartZ=0 EndX=25 EndY=60 EndZ=0
    g8: ArcOfCircle CenterX=35.5717 CenterY=83.343 CenterZ=0 NormalX=0 NormalY=0 NormalZ=1 AngleXU=0 Radius=25.6254 StartAngle=3.07689 EndAngle=4.28714
    g9: LineSegment [constr] StartX=25 StartY=60 StartZ=0 EndX=41.707 EndY=52.4336 EndZ=0
    g10: LineSegment StartX=10 StartY=85 StartZ=0 EndX=2.99673 EndY=85 EndZ=0
    g11: LineSegment [constr] StartX=0 StartY=50.6044 StartZ=0 EndX=0 EndY=85 EndZ=0
    g12: LineSegment StartX=0 StartY=-80.5471 StartZ=0 EndX=0 EndY=-47.458 EndZ=0
    g13: LineSegment StartX=0 StartY=-47.458 StartZ=0 EndX=0 EndY=85 EndZ=0
    g14: LineSegment StartX=2.99673 StartY=85 StartZ=0 EndX=0 EndY=85 EndZ=0
  constraints (31):
    c: Symmetric(g0,g0,g-1)
    c: DistanceY(g0,g0) = 100
    c: DistanceX(g-1,g0) = 17.5
    c: Tangent(g1,g0) = -1.5708
    c: Coincident(g3,g2)
    c: PointOnObject(g3,g-2)
    c: Horizontal(g3)
    c: Coincident(g4,g1)
    c: Coincident(g2,g4)
    c: Radius(g1) = 10
    c: Radius(g4) = 15
    c: Coincident(g5,g0)
    c: Tangent(g6,g5) = 1.5708
    c: Coincident(g7,g6)
    c: Coincident(g8,g7)
    c: Coincident(g9,g7)
    c: Tangent(g8,g9)
    c: Coincident(g10,g8)
    c: PointOnObject(g11,g-2)
    c: Horizontal(g10)
    c: DistanceX(g11,g10) = 10
    c: DistanceX(g-1,g7) = 25
    c: DistanceY(g-1,g11) = 85
    c: DistanceY(g-1,g7) = 60
    c: Coincident(g3,g12)
    c: PointOnObject(g12,g-2)
    c: Coincident(g13,g12)
    c: Coincident(g13,g11)
    c: Coincident(g14,g10)
    c: Coincident(g14,g11)
    c: Horizontal(g14)
FEATURE [PartDesign::Revolution] Revolution003
  Angle = 360
  Angle2 = 60
  Axis = (0,1,0)
  Base = (0,0,0)
  Profile = -> Sketch030
  ReferenceAxis = -> Sketch030 [V_Axis]
  Refine = true
  Reversed = true
  Suppressed = false
  Type = 0
FEATURE [Sketcher::SketchObject] Sketch031
  ArcFitTolerance = 1e-06
  AttachmentSupport = -> [YZ_Plane019]
  FullyConstrained = true
  MakeInternals = false
  MapMode = 5
  Placement = pos=(0,0,0) rot=(0.57735,0.57735,0.57735;2.0944rad)
  sketch-geometry (4):
    g0: ArcOfCircle CenterX=-52 CenterY=17.5 CenterZ=0 NormalX=0 NormalY=0 NormalZ=1 AngleXU=0 Radius=0.6 StartAngle=1.5708 EndAngle=4.71239
    g1: ArcOfCircle CenterX=-50 CenterY=17.5 CenterZ=0 NormalX=0 NormalY=0 NormalZ=1 AngleXU=0 Radius=0.6 StartAngle=4.71239 EndAngle=7.85398
    g2: LineSegment StartX=-52 StartY=18.1 StartZ=0 EndX=-50 EndY=18.1 EndZ=0
    g3: LineSegment StartX=-52 StartY=16.9 StartZ=0 EndX=-50 EndY=16.9 EndZ=0
  constraints (10):
    c: Tangent(g0,g2) = 1.5708
    c: Tangent(g0,g3) = -1.5708
    c: Tangent(g1,g2) = 1.5708
    c: Tangent(g1,g3) = -1.5708
    c: Equal(g0,g1)
    c: Horizontal(g2)
    c: DistanceX(g0,g1) = 2
    c: DistanceY(g1,g1) = 1.2
    c: DistanceY(g-1,g0) = 17.5
    c: DistanceX(g1,g-1) = 50
FEATURE [PartDesign::Revolution] Revolution004
  Angle = 360
  Angle2 = 60
  Axis = (0,1,0)
  Base = (0,0,0)
  Placement = pos=(0,0,0) rot=(1,1,1;2.0944rad)
  Profile = -> Sketch031
  ReferenceAxis = -> Sketch031 [H_Axis]
  Refine = true
  Suppressed = false
  Type = 0
FEATURE [Sketcher::SketchObject] Sketch032
  ArcFitTolerance = 1e-06
  AttachmentSupport = -> [YZ_Plane019]
  FullyConstrained = true
  MakeInternals = false
  MapMode = 5
  Placement = pos=(0,0,0) rot=(0.57735,0.57735,0.57735;2.0944rad)
  sketch-geometry (4):
    g0: ArcOfCircle CenterX=-52 CenterY=17.5 CenterZ=0 NormalX=0 NormalY=0 NormalZ=1 AngleXU=0 Radius=0.6 StartAngle=1.5708 EndAngle=4.71239
    g1: ArcOfCircle CenterX=-50 CenterY=17.5 CenterZ=0 NormalX=0 NormalY=0 NormalZ=1 AngleXU=0 Radius=0.6 StartAngle=4.71239 EndAngle=7.85398
    g2: LineSegment StartX=-52 StartY=18.1 StartZ=0 EndX=-50 EndY=18.1 EndZ=0
    g3: LineSegment StartX=-52 StartY=16.9 StartZ=0 EndX=-50 EndY=16.9 EndZ=0
  constraints (10):
    c: Tangent(g0,g2) = 1.5708
    c: Tangent(g0,g3) = -1.5708
    c: Tangent(g1,g2) = 1.5708
    c: Tangent(g1,g3) = -1.5708
    c: Equal(g0,g1)
    c: Horizontal(g2)
    c: DistanceX(g0,g1) = 2
    c: DistanceY(g1,g1) = 1.2
    c: DistanceY(g-1,g0) = 17.5
    c: DistanceX(g1,g-1) = 50
FEATURE [PartDesign::AdditiveHelix] AdditiveHelix002
  Angle = 0
  Axis = (0,1,0)
  Base = (0,0,0)
  BaseFeature = -> Revolution004
  Growth = 0
  HasBeenEdited = true
  Height = 100
  LeftHanded = false
  Mode = 0
  Outside = false
  Pitch = 15
  Placement = pos=(0,0,0) rot=(1,1,1;2.0944rad)
  Profile = -> Sketch032
  ReferenceAxis = -> Sketch032 [H_Axis]
  Refine = true
  Suppressed = false
  Tolerance = 0.1
  Turns = 6.66667
FEATURE [Sketcher::SketchObject] Sketch033
  ArcFitTolerance = 1e-06
  AttachmentSupport = -> [YZ_Plane019]
  FullyConstrained = true
  MakeInternals = false
  MapMode = 5
  Placement = pos=(0,0,0) rot=(0.57735,0.57735,0.57735;2.0944rad)
  sketch-geometry (4):
    g0: ArcOfCircle CenterX=-52 CenterY=17.5 CenterZ=0 NormalX=0 NormalY=0 NormalZ=1 AngleXU=0 Radius=0.6 StartAngle=1.5708 EndAngle=4.71239
    g1: ArcOfCircle CenterX=-50 CenterY=17.5 CenterZ=0 NormalX=0 NormalY=0 NormalZ=1 AngleXU=0 Radius=0.6 StartAngle=4.71239 EndAngle=7.85398
    g2: LineSegment StartX=-52 StartY=18.1 StartZ=0 EndX=-50 EndY=18.1 EndZ=0
    g3: LineSegment StartX=-52 StartY=16.9 StartZ=0 EndX=-50 EndY=16.9 EndZ=0
  constraints (10):
    c: Tangent(g0,g2) = 1.5708
    c: Tangent(g0,g3) = -1.5708
    c: Tangent(g1,g2) = 1.5708
    c: Tangent(g1,g3) = -1.5708
    c: Equal(g0,g1)
    c: Horizontal(g2)
    c: DistanceX(g0,g1) = 2
    c: DistanceY(g1,g1) = 1.2
    c: DistanceY(g-1,g0) = 17.5
    c: DistanceX(g1,g-1) = 50
FEATURE [PartDesign::AdditiveHelix] AdditiveHelix003
  Angle = 0
  Axis = (0,1,0)
  Base = (0,0,0)
  BaseFeature = -> AdditiveHelix002
  Growth = 0
  HasBeenEdited = true
  Height = 100
  LeftHanded = true
  Mode = 0
  Outside = false
  Pitch = 15
  Placement = pos=(0,0,0) rot=(1,1,1;2.0944rad)
  Profile = -> Sketch033
  ReferenceAxis = -> Sketch033 [H_Axis]
  Refine = true
  Suppressed = false
  Tolerance = 0.1
  Turns = 6.66667
FEATURE [Sketcher::SketchObject] Sketch034
  ArcFitTolerance = 1e-06
  AttachmentOffset = pos=(0,0,-12) rot=(0,0,1;0rad)
  AttachmentSupport = -> [XY_Plane019]
  FullyConstrained = false
  MakeInternals = false
  MapMode = 5
  Placement = pos=(0,0,-12) rot=(0,0,1;0rad)
  sketch-geometry (4):
    g0: LineSegment StartX=-45.5492 StartY=69.0537 StartZ=0 EndX=-45.5492 EndY=-94.9035 EndZ=0
    g1: LineSegment StartX=-45.5492 StartY=-94.9035 StartZ=0 EndX=41.2372 EndY=-94.9035 EndZ=0
    g2: LineSegment StartX=41.2372 StartY=-94.9035 StartZ=0 EndX=41.2372 EndY=69.0537 EndZ=0
    g3: LineSegment StartX=41.2372 StartY=69.0537 StartZ=0 EndX=-45.5492 EndY=69.0537 EndZ=0
  constraints (8):
    c: Coincident(g0,g1)
    c: Coincident(g1,g2)
    c: Coincident(g2,g3)
    c: Coincident(g3,g0)
    c: Vertical(g0)
    c: Vertical(g2)
    c: Horizontal(g1)
    c: Horizontal(g3)
FEATURE [PartDesign::Pocket] Pocket010
  BaseFeature = -> AdditiveHelix003
  Direction = (0,0,-1)
  Length = 39
  Length2 = 5
  Placement = pos=(0,0,0) rot=(1,1,1;2.0944rad)
  Profile = -> Sketch034
  ReferenceAxis = -> Sketch034 [N_Axis]
  Refine = true
  Reversed = true
  Suppressed = false
  Type = 0
FEATURE [PartDesign::Body] Body007  label="RoundedLaces"
  AllowCompound = true
  Group = -> [Sketch031,Revolution004,Sketch032,AdditiveHelix002,Sketch033,AdditiveHelix003,Sketch034,Pocket010]
  Origin = -> Origin019
  Tip = -> Pocket010
FEATURE [Sketcher::SketchObject] Sketch035
  ArcFitTolerance = 1e-06
  AttachmentOffset = pos=(0,0,-12) rot=(0,0,1;0rad)
  AttachmentSupport = -> [XY_Plane018]
  FullyConstrained = false
  MakeInternals = false
  MapMode = 5
  Placement = pos=(0,0,-12) rot=(0,0,1;0rad)
  sketch-geometry (4):
    g0: LineSegment StartX=-84.5744 StartY=135.69 StartZ=0 EndX=-84.5744 EndY=-134.051 EndZ=0
    g1: LineSegment StartX=-84.5744 StartY=-134.051 StartZ=0 EndX=84.3229 EndY=-134.051 EndZ=0
    g2: LineSegment StartX=84.3229 StartY=-134.051 StartZ=0 EndX=84.3229 EndY=135.69 EndZ=0
    g3: LineSegment StartX=84.3229 StartY=135.69 StartZ=0 EndX=-84.5744 EndY=135.69 EndZ=0
  constraints (8):
    c: Coincident(g0,g1)
    c: Coincident(g1,g2)
    c: Coincident(g2,g3)
    c: Coincident(g3,g0)
    c: Vertical(g0)
    c: Vertical(g2)
    c: Horizontal(g1)
    c: Horizontal(g3)
FEATURE [PartDesign::Pocket] Pocket011
  BaseFeature = -> Revolution003
  Direction = (0,0,-1)
  Length = 44
  Length2 = 5
  Profile = -> Sketch035
  ReferenceAxis = -> Sketch035 [N_Axis]
  Refine = true
  Reversed = true
  Suppressed = false
  Type = 0
FEATURE [PartDesign::SubShapeBinder] Binder004
  BindCopyOnChange = 0
  BindMode = 0
  ClaimChildren = false
  Context = -> Part002 [Body006.Binder004.]
  Fuse = false
  MakeFace = true
  OffsetFill = false
  OffsetIntersection = false
  OffsetJoinType = 0
  OffsetOpenResult = false
  PartialLoad = false
  Refine = true
  Relative = true
  Support = -> [Part[Body.]]
  _Version = 2
FEATURE [Sketcher::SketchObject] Sketch037
  ArcFitTolerance = 1e-06
  AttachmentOffset = pos=(0,0,-45) rot=(0,0,1;0rad)
  AttachmentSupport = -> [XZ_Plane021]
  FullyConstrained = false
  MakeInternals = false
  MapMode = 5
  Placement = pos=(0,45,-1e-14) rot=(1,0,0;1.5708rad)
  sketch-geometry (10):
    g0: Circle [constr] CenterX=7.3 CenterY=0 CenterZ=0 NormalX=0 NormalY=0 NormalZ=1 AngleXU=0 Radius=7.25
    g1: Circle [constr] CenterX=-7.3 CenterY=0 CenterZ=0 NormalX=0 NormalY=0 NormalZ=1 AngleXU=0 Radius=7.25
    g2: ArcOfCircle CenterX=-7.3 CenterY=0 CenterZ=0 NormalX=0 NormalY=0 NormalZ=1 AngleXU=0 Radius=7.3 StartAngle=4.30708 EndAngle=5.615
    g3: ArcOfCircle CenterX=7.3 CenterY=0 CenterZ=0 NormalX=0 NormalY=0 NormalZ=1 AngleXU=0 Radius=7.3 StartAngle=3.80978 EndAngle=5.12153
    g4: ArcOfCircle CenterX=3e-16 CenterY=-5.76194 CenterZ=0 NormalX=0 NormalY=0 NormalZ=1 AngleXU=0 Radius=2 StartAngle=0.668187 EndAngle=2.47341
    g5: LineSegment StartX=-10.8756 StartY=-11.4562 StartZ=0 EndX=-10.8756 EndY=-7.16805 EndZ=0
    g6: LineSegment StartX=10.903 StartY=-11.4562 StartZ=0 EndX=10.903 EndY=-7.15622 EndZ=0
    g7: ArcOfCircle CenterX=-10.3756 CenterY=-7.16805 CenterZ=0 NormalX=0 NormalY=0 NormalZ=1 AngleXU=0 Radius=0.5 StartAngle=1.16549 EndAngle=3.14159
    g8: ArcOfCircle CenterX=10.403 CenterY=-7.15622 CenterZ=0 NormalX=0 NormalY=0 NormalZ=1 AngleXU=0 Radius=0.5 StartAngle=-9e-16 EndAngle=1.97994
    g9: LineSegment StartX=10.903 StartY=-11.4562 StartZ=0 EndX=-10.8756 EndY=-11.4562 EndZ=0
  constraints (24):
    c: PointOnObject(g0,g-1)
    c: Diameter(g1) = 14.5
    c: Diameter(g0) = 14.5
    c: Symmetric(g1,g0,g-2)
    c: DistanceX(g1,g-1) = 7.3
    c: Coincident(g3,g0)
    c: Radius(g2) = 7.3
    c: Coincident(g1,g2)
    c: Tangent(g2,g4) = 1.5708
    c: Tangent(g3,g4) = 1.5708
    c: Vertical(g5)
    c: Vertical(g6)
    c: Radius(g3) = 7.3
    c: Tangent(g2,g7) = 1.5708
    c: Tangent(g5,g7) = 1.5708
    c: Tangent(g3,g8) = 1.5708
    c: Tangent(g6,g8) = -1.5708
    c: Radius(g8) = 0.5
    c: Radius(g7) = 0.5
    c: Radius(g4) = 2
    c: Coincident(g9,g6)
    c: Coincident(g9,g5)
    c: DistanceY(g6,g6) = 4.3
    c: Horizontal(g9)
FEATURE [PartDesign::Pad] Pad005
  Direction = (0,-1,2e-16)
  Length = 30
  Length2 = 10
  Placement = pos=(0,0,0) rot=(1,0,0;1.5708rad)
  Profile = -> Sketch037
  ReferenceAxis = -> Sketch037 [N_Axis]
  Refine = true
  Suppressed = false
  Type = 0
FEATURE [Sketcher::SketchObject] Sketch038
  ArcFitTolerance = 1e-06
  AttachmentOffset = pos=(0,0,-12) rot=(0,0,1;0rad)
  AttachmentSupport = -> [XY_Plane018]
  FullyConstrained = false
  MakeInternals = false
  MapMode = 5
  Placement = pos=(0,0,-12) rot=(0,0,1;0rad)
  sketch-geometry (4):
    g0: Circle CenterX=-5.5 CenterY=30 CenterZ=0 NormalX=0 NormalY=0 NormalZ=1 AngleXU=0 Radius=0.9
    g1: Circle CenterX=-5.5 CenterY=-30 CenterZ=0 NormalX=0 NormalY=0 NormalZ=1 AngleXU=0 Radius=0.9
    g2: Circle CenterX=5.5 CenterY=30 CenterZ=0 NormalX=0 NormalY=0 NormalZ=1 AngleXU=0 Radius=0.9
    g3: Circle CenterX=5.5 CenterY=-30 CenterZ=0 NormalX=0 NormalY=0 NormalZ=1 AngleXU=0 Radius=0.9
  constraints (9):
    c: Diameter(g0) = 1.8
    c: DistanceX(g0,g-1) = 5.5
    c: DistanceY(g-1,g0) = 30
    c: Diameter(g1) = 1.8
    c: Diameter(g2) = 1.8
    c: Diameter(g3) = 1.8
    c: Horizontal(g0,g2)
    c: DistanceY(g1,g-1) = 30
    c: Horizontal(g1,g3)
FEATURE [PartDesign::Pocket] Pocket012
  BaseFeature = -> Pocket011
  Direction = (0,0,-1)
  Length = 4
  Length2 = 5
  Profile = -> Sketch038
  ReferenceAxis = -> Sketch038 [N_Axis]
  Refine = true
  Suppressed = false
  Type = 0
FEATURE [Sketcher::SketchObject] Sketch039
  ArcFitTolerance = 1e-06
  AttachmentOffset = pos=(0,0,45) rot=(0,0,1;0rad)
  AttachmentSupport = -> [XZ_Plane018]
  ExternalGeometry = -> [Pocket012]
  FullyConstrained = true
  MakeInternals = false
  MapMode = 5
  Placement = pos=(0,-45,1e-14) rot=(1,0,0;1.5708rad)
  sketch-geometry (3):
    g0: LineSegment StartX=-4 StartY=-12 StartZ=0 EndX=0 EndY=-16 EndZ=0
    g1: LineSegment StartX=0 StartY=-16 StartZ=0 EndX=4 EndY=-12 EndZ=0
    g2: LineSegment StartX=-4 StartY=-12 StartZ=0 EndX=4 EndY=-12 EndZ=0
  constraints (8):
    c: PointOnObject(g0,g-7)
    c: PointOnObject(g0,g-2)
    c: Coincident(g0,g1)
    c: Coincident(g0,g2)
    c: Coincident(g2,g1)
    c: Symmetric(g0,g1,g-2)
    c: DistanceX(g0,g-1) = 4
    c: Distance(g0,g2) = 4
FEATURE [PartDesign::Pocket] Pocket013
  BaseFeature = -> Pocket012
  Direction = (0,1,-2e-16)
  Length = 30
  Length2 = 5
  Profile = -> Sketch039
  ReferenceAxis = -> Sketch039 [N_Axis]
  Refine = true
  Suppressed = false
  Type = 0
FEATURE [Sketcher::SketchObject] Sketch040
  ArcFitTolerance = 1e-06
  AttachmentOffset = pos=(0,0,-45.5) rot=(0,0,1;0rad)
  AttachmentSupport = -> [XZ_Plane018]
  FullyConstrained = false
  MakeInternals = false
  MapMode = 5
  Placement = pos=(0,45.5,-1.01e-14) rot=(1,0,0;1.5708rad)
  sketch-geometry (3):
    g0: LineSegment StartX=-4 StartY=-12 StartZ=0 EndX=0 EndY=-16 EndZ=0
    g1: LineSegment StartX=0 StartY=-16 StartZ=0 EndX=4 EndY=-12 EndZ=0
    g2: LineSegment StartX=-4 StartY=-12 StartZ=0 EndX=4 EndY=-12 EndZ=0
  constraints (7):
    c: PointOnObject(g0,g-2)
    c: Coincident(g0,g1)
    c: Coincident(g0,g2)
    c: Coincident(g2,g1)
    c: Symmetric(g0,g1,g-2)
    c: DistanceX(g0,g-1) = 4
    c: Distance(g0,g2) = 4
FEATURE [PartDesign::Pocket] Pocket014
  BaseFeature = -> Pocket013
  Direction = (0,1,-2e-16)
  Length = 30
  Length2 = 5
  Profile = -> Sketch040
  ReferenceAxis = -> Sketch040 [N_Axis]
  Refine = true
  Reversed = true
  Suppressed = false
  Type = 0
FEATURE [Sketcher::SketchObject] Sketch041
  ArcFitTolerance = 1e-06
  AttachmentSupport = -> [XY_Plane021]
  FullyConstrained = false
  MakeInternals = false
  MapMode = 5
  sketch-geometry (4):
    g0: Circle CenterX=-5.5 CenterY=30 CenterZ=0 NormalX=0 NormalY=0 NormalZ=1 AngleXU=0 Radius=0.9
    g1: Circle CenterX=-5.5 CenterY=-30 CenterZ=0 NormalX=0 NormalY=0 NormalZ=1 AngleXU=0 Radius=0.9
    g2: Circle CenterX=5.5 CenterY=30 CenterZ=0 NormalX=0 NormalY=0 NormalZ=1 AngleXU=0 Radius=0.9
    g3: Circle CenterX=5.5 CenterY=-30 CenterZ=0 NormalX=0 NormalY=0 NormalZ=1 AngleXU=0 Radius=0.9
  constraints (9):
    c: Diameter(g0) = 1.8
    c: DistanceX(g0,g-1) = 5.5
    c: DistanceY(g-1,g0) = 30
    c: Diameter(g1) = 1.8
    c: Diameter(g2) = 1.8
    c: Diameter(g3) = 1.8
    c: Horizontal(g0,g2)
    c: DistanceY(g1,g-1) = 30
    c: Horizontal(g1,g3)
FEATURE [Sketcher::SketchObject] Sketch042
  ArcFitTolerance = 1e-06
  AttachmentOffset = pos=(0,0,-45) rot=(0,0,1;0rad)
  AttachmentSupport = -> [XZ_Plane021]
  FullyConstrained = true
  MakeInternals = false
  MapMode = 5
  Placement = pos=(0,45,-1e-14) rot=(1,0,0;1.5708rad)
  sketch-geometry (3):
    g0: LineSegment StartX=-4 StartY=-11.4 StartZ=0 EndX=0 EndY=-15.4 EndZ=0
    g1: LineSegment StartX=0 StartY=-15.4 StartZ=0 EndX=4 EndY=-11.4 EndZ=0
    g2: LineSegment StartX=-4 StartY=-11.4 StartZ=0 EndX=4 EndY=-11.4 EndZ=0
  constraints (8):
    c: PointOnObject(g0,g-2)
    c: Coincident(g0,g1)
    c: Coincident(g0,g2)
    c: Coincident(g2,g1)
    c: Symmetric(g0,g1,g-2)
    c: DistanceX(g0,g-1) = 4
    c: Distance(g0,g2) = 4
    c: DistanceY(g1,g-1) = 11.4
FEATURE [PartDesign::Pad] Pad006
  BaseFeature = -> Pad005
  Direction = (0,-1,2e-16)
  Length = 30
  Length2 = 10
  Placement = pos=(0,0,0) rot=(1,0,0;1.5708rad)
  Profile = -> Sketch042
  ReferenceAxis = -> Sketch042 [N_Axis]
  Refine = true
  Suppressed = false
  Type = 0
FEATURE [Sketcher::SketchObject] Sketch043
  ArcFitTolerance = 1e-06
  AttachmentOffset = pos=(0,0,-9) rot=(0,0,1;0rad)
  AttachmentSupport = -> [XY_Plane021]
  FullyConstrained = false
  MakeInternals = false
  MapMode = 5
  Placement = pos=(0,0,-9) rot=(0,0,1;0rad)
  sketch-geometry (4):
    g0: Circle CenterX=-5.5 CenterY=30 CenterZ=0 NormalX=0 NormalY=0 NormalZ=1 AngleXU=0 Radius=0.9
    g1: Circle CenterX=-5.5 CenterY=-30 CenterZ=0 NormalX=0 NormalY=0 NormalZ=1 AngleXU=0 Radius=0.9
    g2: Circle CenterX=5.5 CenterY=30 CenterZ=0 NormalX=0 NormalY=0 NormalZ=1 AngleXU=0 Radius=0.9
    g3: Circle CenterX=5.5 CenterY=-30 CenterZ=0 NormalX=0 NormalY=0 NormalZ=1 AngleXU=0 Radius=0.9
  constraints (10):
    c: Diameter(g0) = 1.8
    c: DistanceX(g0,g-1) = 5.5
    c: DistanceY(g-1,g0) = 30
    c: Diameter(g1) = 1.8
    c: Diameter(g3) = 1.8
    c: Horizontal(g0,g2)
    c: DistanceY(g1,g-1) = 30
    c: Horizontal(g1,g3)
    c: DistanceY(g-3,g-4) = 30
    c: DistanceY(g-3,g2) = 15
FEATURE [Sketcher::SketchObject] Sketch044
  ArcFitTolerance = 1e-06
  AttachmentOffset = pos=(0,0,15) rot=(0,0,1;0rad)
  AttachmentSupport = -> [XZ_Plane022]
  FullyConstrained = false
  MakeInternals = false
  MapMode = 5
  Placement = pos=(0,-15,3.3e-15) rot=(1,0,0;1.5708rad)
  sketch-geometry (13):
    g0: Circle [constr] CenterX=7.3 CenterY=0 CenterZ=0 NormalX=0 NormalY=0 NormalZ=1 AngleXU=0 Radius=7.25
    g1: Circle [constr] CenterX=-7.3 CenterY=0 CenterZ=0 NormalX=0 NormalY=0 NormalZ=1 AngleXU=0 Radius=7.25
    g2: ArcOfCircle CenterX=-7.3 CenterY=0 CenterZ=0 NormalX=0 NormalY=0 NormalZ=1 AngleXU=0 Radius=7.3 StartAngle=4.30708 EndAngle=5.615
    g3: ArcOfCircle CenterX=7.3 CenterY=0 CenterZ=0 NormalX=0 NormalY=0 NormalZ=1 AngleXU=0 Radius=7.3 StartAngle=3.80978 EndAngle=5.1177
    g4: ArcOfCircle CenterX=3e-16 CenterY=-5.76194 CenterZ=0 NormalX=0 NormalY=0 NormalZ=1 AngleXU=0 Radius=2 StartAngle=0.668187 EndAngle=2.47341
    g5: LineSegment StartX=-10.8756 StartY=-12.0091 StartZ=0 EndX=-10.8756 EndY=-7.16805 EndZ=0
    g6: LineSegment StartX=10.8756 StartY=-12.0091 StartZ=0 EndX=10.8756 EndY=-7.16805 EndZ=0
    g7: ArcOfCircle CenterX=-10.3756 CenterY=-7.16805 CenterZ=0 NormalX=0 NormalY=0 NormalZ=1 AngleXU=0 Radius=0.5 StartAngle=1.16549 EndAngle=3.14159
    g8: ArcOfCircle CenterX=10.3756 CenterY=-7.16805 CenterZ=0 NormalX=0 NormalY=0 NormalZ=1 AngleXU=0 Radius=0.5 StartAngle=0 EndAngle=1.9761
    g9: LineSegment StartX=-10.8756 StartY=-12.0091 StartZ=0 EndX=-4 EndY=-12.0091 EndZ=0
    g10: LineSegment StartX=-4 StartY=-12.0091 StartZ=0 EndX=0 EndY=-16.0091 EndZ=0
    g11: LineSegment StartX=0 StartY=-16.0091 StartZ=0 EndX=4 EndY=-12.0091 EndZ=0
    g12: LineSegment StartX=4 StartY=-12.0091 StartZ=0 EndX=10.8756 EndY=-12.0091 EndZ=0
  constraints (31):
    c: PointOnObject(g0,g-1)
    c: Diameter(g1) = 14.5
    c: Diameter(g0) = 14.5
    c: Symmetric(g1,g0,g-2)
    c: DistanceX(g1,g-1) = 7.3
    c: Coincident(g3,g0)
    c: Radius(g2) = 7.3
    c: Coincident(g1,g2)
    c: Tangent(g2,g4) = 1.5708
    c: Tangent(g3,g4) = 1.5708
    c: Vertical(g5)
    c: Vertical(g6)
    c: Radius(g3) = 7.3
    c: Tangent(g2,g7) = 1.5708
    c: Tangent(g5,g7) = 1.5708
    c: Tangent(g3,g8) = 1.5708
    c: Tangent(g6,g8) = -1.5708
    c: Radius(g8) = 0.5
    c: Radius(g7) = 0.5
    c: Radius(g4) = 2
    c: Coincident(g5,g9)
    c: Horizontal(g9)
    c: Coincident(g9,g10)
    c: PointOnObject(g10,g-2)
    c: Coincident(g10,g11)
    c: Coincident(g11,g12)
    c: Coincident(g12,g6)
    c: Horizontal(g12)
    c: Symmetric(g9,g11,g-2)
    c: DistanceX(g9,g-1) = 4
    c: DistanceY(g10,g11) = 4
FEATURE [PartDesign::Pad] Pad007
  Direction = (0,-1,2e-16)
  Length = 30
  Length2 = 10
  Placement = pos=(0,0,0) rot=(1,0,0;1.5708rad)
  Profile = -> Sketch044
  ReferenceAxis = -> Sketch044 [N_Axis]
  Refine = true
  Suppressed = false
  Type = 0
FEATURE [Sketcher::SketchObject] Sketch045
  ArcFitTolerance = 1e-06
  AttachmentOffset = pos=(0,0,-9) rot=(0,0,1;0rad)
  AttachmentSupport = -> [XY_Plane022]
  ExternalGeometry = -> [Pad007]
  FullyConstrained = false
  MakeInternals = false
  MapMode = 5
  Placement = pos=(0,0,-9) rot=(0,0,1;0rad)
  sketch-geometry (4):
    g0: Circle CenterX=-5.5 CenterY=30 CenterZ=0 NormalX=0 NormalY=0 NormalZ=1 AngleXU=0 Radius=0.9
    g1: Circle CenterX=-5.5 CenterY=-30 CenterZ=0 NormalX=0 NormalY=0 NormalZ=1 AngleXU=0 Radius=0.9
    g2: Circle CenterX=5.5 CenterY=30 CenterZ=0 NormalX=0 NormalY=0 NormalZ=1 AngleXU=0 Radius=0.9
    g3: Circle CenterX=5.5 CenterY=-30 CenterZ=0 NormalX=0 NormalY=0 NormalZ=1 AngleXU=0 Radius=0.9
  constraints (10):
    c: Diameter(g0) = 1.8
    c: DistanceX(g0,g-1) = 5.5
    c: DistanceY(g-1,g0) = 30
    c: Diameter(g1) = 1.8
    c: Diameter(g2) = 1.8
    c: Diameter(g3) = 1.8
    c: Horizontal(g0,g2)
    c: DistanceY(g1,g-1) = 30
    c: Horizontal(g1,g3)
    c: DistanceY(g3,g-3) = 15
FEATURE [PartDesign::Pocket] Pocket015
  BaseFeature = -> Pad007
  Direction = (0,0,-1)
  Length = 5
  Length2 = 5
  Placement = pos=(0,0,0) rot=(1,0,0;1.5708rad)
  Profile = -> Sketch045
  ReferenceAxis = -> Sketch045 [N_Axis]
  Refine = true
  Suppressed = false
  Type = 0
FEATURE [PartDesign::Body] Body009  label="Top Part"
  AllowCompound = true
  Group = -> [Sketch044,Pad007,Sketch045,Pocket015]
  Origin = -> Origin022
  Tip = -> Pocket015
FEATURE [PartDesign::Pocket] Pocket016
  BaseFeature = -> Pad006
  Direction = (0,0,-1)
  Length = 5
  Length2 = 5
  Placement = pos=(0,0,0) rot=(1,0,0;1.5708rad)
  Profile = -> Sketch043
  ReferenceAxis = -> Sketch043 [N_Axis]
  Refine = true
  Suppressed = false
  Type = 0
FEATURE [PartDesign::Body] Body008  label="Bottom Part"
  AllowCompound = true
  Group = -> [Sketch037,Pad005,Sketch041,Sketch042,Pad006,Sketch043,Pocket016]
  Origin = -> Origin021
  Tip = -> Pocket016
FEATURE [App::Part] Part003  label="Battery Lid part Duex"
  Group = -> [Body008,Body009]
  Origin = -> Origin020
FEATURE [Sketcher::SketchObject] Sketch046
  ArcFitTolerance = 1e-06
  AttachmentOffset = pos=(0,0,-11) rot=(0,0,1;0rad)
  AttachmentSupport = -> [XY_Plane018]
  FullyConstrained = true
  MakeInternals = false
  MapMode = 5
  Placement = pos=(0,0,-11) rot=(0,0,1;0rad)
  sketch-geometry (2):
    g0: Circle CenterX=0 CenterY=62 CenterZ=0 NormalX=0 NormalY=0 NormalZ=1 AngleXU=0 Radius=1.6
    g1: Circle CenterX=0 CenterY=-63 CenterZ=0 NormalX=0 NormalY=0 NormalZ=1 AngleXU=0 Radius=1.6
  constraints (6):
    c: PointOnObject(g0,g-2)
    c: PointOnObject(g1,g-2)
    c: Diameter(g1) = 3.2
    c: Diameter(g0) = 3.2
    c: DistanceY(g-1,g0) = 62
    c: DistanceY(g1,g-1) = 63
FEATURE [PartDesign::Pocket] Pocket017
  BaseFeature = -> Pocket014
  Direction = (0,0,-1)
  Length = 25
  Length2 = 5
  Profile = -> Sketch046
  ReferenceAxis = -> Sketch046 [N_Axis]
  Refine = true
  Suppressed = false
  Type = 0
FEATURE [Sketcher::SketchObject] Sketch047
  ArcFitTolerance = 1e-06
  AttachmentOffset = pos=(0,0,-15) rot=(0,0,1;0rad)
  AttachmentSupport = -> [XY_Plane018]
  FullyConstrained = true
  MakeInternals = false
  MapMode = 5
  Placement = pos=(0,0,-15) rot=(0,0,1;0rad)
  sketch-geometry (2):
    g0: Circle CenterX=0 CenterY=62 CenterZ=0 NormalX=0 NormalY=0 NormalZ=1 AngleXU=0 Radius=3.15
    g1: Circle CenterX=0 CenterY=-63 CenterZ=0 NormalX=0 NormalY=0 NormalZ=1 AngleXU=0 Radius=3.15
  constraints (6):
    c: PointOnObject(g0,g-2)
    c: PointOnObject(g1,g-2)
    c: Diameter(g1) = 6.3
    c: Diameter(g0) = 6.3
    c: DistanceY(g-1,g0) = 62
    c: DistanceY(g1,g-1) = 63
FEATURE [PartDesign::Pocket] Pocket018
  BaseFeature = -> Pocket017
  Direction = (0,0,-1)
  Length = 12
  Length2 = 5
  Profile = -> Sketch047
  ReferenceAxis = -> Sketch047 [N_Axis]
  Refine = true
  Suppressed = false
  Type = 0
FEATURE [PartDesign::Fillet] Fillet
  Base = -> Pocket018 [Edge40,Edge36]
  BaseFeature = -> Pocket018
  Radius = 1
  Refine = true
  SupportTransform = false
  Suppressed = false
  UseAllEdges = false
FEATURE [PartDesign::Body] Body006  label="RoundedBit"
  AllowCompound = true
  Group = -> [Sketch030,Revolution003,Sketch035,Pocket011,Binder004,Sketch038,Pocket012,Sketch039,Pocket013,Sketch040,Pocket014,Sketch046,Pocket017,Sketch047,Pocket018,Fillet]
  Origin = -> Origin018
  Tip = -> Fillet
FEATURE [App::Part] Part002  label="Battery Lid"
  Group = -> [Body006,Body007]
  Origin = -> Origin017
FEATURE [Sketcher::SketchObject] Sketch048
  ArcFitTolerance = 1e-06
  AttachmentOffset = pos=(0,0,-13) rot=(0,0,1;0rad)
  AttachmentSupport = -> [XY_Plane001]
  FullyConstrained = true
  MakeInternals = false
  MapMode = 5
  Placement = pos=(0,0,-13) rot=(0,0,1;0rad)
  sketch-geometry (2):
    g0: Circle CenterX=0 CenterY=62 CenterZ=0 NormalX=0 NormalY=0 NormalZ=1 AngleXU=0 Radius=2
    g1: Circle CenterX=0 CenterY=-63 CenterZ=0 NormalX=0 NormalY=0 NormalZ=1 AngleXU=0 Radius=2
  constraints (6):
    c: PointOnObject(g0,g-2)
    c: PointOnObject(g1,g-2)
    c: Diameter(g1) = 4
    c: Diameter(g0) = 4
    c: DistanceY(g-1,g0) = 62
    c: DistanceY(g1,g-1) = 63
FEATURE [PartDesign::Pocket] Pocket019  label="Heat Set Inserts"
  BaseFeature = -> Pocket009
  Direction = (0,0,-1)
  Length = 5
  Length2 = 5
  Profile = -> Sketch048
  ReferenceAxis = -> Sketch048 [N_Axis]
  Refine = true
  Reversed = true
  Suppressed = false
  Type = 0
FEATURE [Sketcher::SketchObject] Sketch049
  ArcFitTolerance = 1e-06
  AttachmentSupport = -> [XY_Plane023]
  FullyConstrained = true
  MakeInternals = false
  MapMode = 5
  expr: Constraints[9] = 15.5 * 2 + 1
  sketch-geometry (8):
    g0: LineSegment StartX=-16 StartY=28.5 StartZ=0 EndX=-16 EndY=-28.5 EndZ=0
    g1: LineSegment StartX=-16 StartY=-28.5 StartZ=0 EndX=16 EndY=-28.5 EndZ=0
    g2: LineSegment StartX=16 StartY=-28.5 StartZ=0 EndX=16 EndY=28.5 EndZ=0
    g3: LineSegment StartX=16 StartY=28.5 StartZ=0 EndX=-16 EndY=28.5 EndZ=0
    g4: LineSegment StartX=-18 StartY=30.5 StartZ=0 EndX=-18 EndY=-30.5 EndZ=0
    g5: LineSegment StartX=-18 StartY=-30.5 StartZ=0 EndX=18 EndY=-30.5 EndZ=0
    g6: LineSegment StartX=18 StartY=-30.5 StartZ=0 EndX=18 EndY=30.5 EndZ=0
    g7: LineSegment StartX=18 StartY=30.5 StartZ=0 EndX=-18 EndY=30.5 EndZ=0
  constraints (23):
    c: Coincident(g0,g1)
    c: Coincident(g1,g2)
    c: Coincident(g2,g3)
    c: Coincident(g3,g0)
    c: Vertical(g0)
    c: Vertical(g2)
    c: Horizontal(g1)
    c: Horizontal(g3)
    c: DistanceY(g2,g2) = 57
    c: DistanceX(g3,g3) = 32
    c: Symmetric(g0,g1,g-1)
    c: Coincident(g4,g5)
    c: Coincident(g5,g6)
    c: Coincident(g6,g7)
    c: Coincident(g7,g4)
    c: Vertical(g4)
    c: Vertical(g6)
    c: Horizontal(g5)
    c: Horizontal(g7)
    c: DistanceY(g2,g6) = 2
    c: DistanceX(g2,g6) = 2
    c: DistanceX(g4,g0) = 2
    c: DistanceY(g5,g1) = 2
FEATURE [PartDesign::Pad] Pad008  label="Outer Box"
  Direction = (0,0,1)
  Length = 16
  Length2 = 10
  Profile = -> Sketch049
  ReferenceAxis = -> Sketch049 [N_Axis]
  Refine = true
  Suppressed = false
  Type = 0
FEATURE [Sketcher::SketchObject] Sketch050
  ArcFitTolerance = 1e-06
  AttachmentSupport = -> [YZ_Plane023]
  ExternalGeometry = -> [Pad008]
  FullyConstrained = false
  MakeInternals = false
  MapMode = 5
  Placement = pos=(0,0,0) rot=(0.57735,0.57735,0.57735;2.0944rad)
  sketch-geometry (8):
    g0: LineSegment StartX=-28.5 StartY=15.3 StartZ=0 EndX=-26.2 EndY=15.3 EndZ=0
    g1: LineSegment StartX=-26.2 StartY=15.3 StartZ=0 EndX=-26.2 EndY=2.3 EndZ=0
    g2: LineSegment StartX=-26.2 StartY=2.3 StartZ=0 EndX=-28.5 EndY=0 EndZ=0
    g3: LineSegment StartX=-28.5 StartY=15.3 StartZ=0 EndX=-28.5 EndY=0 EndZ=0
    g4: LineSegment StartX=28.5 StartY=15.5417 StartZ=0 EndX=26.2 EndY=15.5417 EndZ=0
    g5: LineSegment StartX=26.2 StartY=15.5417 StartZ=0 EndX=26.2 EndY=2.3 EndZ=0
    g6: LineSegment StartX=26.2 StartY=2.3 StartZ=0 EndX=28.5 EndY=0 EndZ=0
    g7: LineSegment StartX=28.5 StartY=15.5417 StartZ=0 EndX=28.5 EndY=0 EndZ=0
  constraints (22):
    c: PointOnObject(g0,g-3)
    c: Horizontal(g0)
    c: Coincident(g0,g1)
    c: Vertical(g1)
    c: Coincident(g1,g2)
    c: Coincident(g2,g-3)
    c: DistanceY(g1,g1) = 13
    c: Angle(g2,g-3) = 0.785398
    c: Coincident(g0,g3)
    c: Coincident(g3,g2)
    c: Horizontal(g4)
    c: Coincident(g4,g5)
    c: Vertical(g5)
    c: Coincident(g5,g6)
    c: Coincident(g4,g7)
    c: Coincident(g7,g6)
    c: DistanceX(g0,g0) = 2.3
    c: DistanceY(g-1,g1) = 2.3
    c: Distance(g4,g4) = 2.3
    c: Vertical(g7)
    c: Symmetric(g2,g6,g-2)
    c: Horizontal(g1,g5)
FEATURE [PartDesign::Pad] Pad009  label="Large Bracket"
  BaseFeature = -> Pad008
  Direction = (1,0,0)
  Length = 30
  Length2 = 10
  Midplane = true
  Profile = -> Sketch050
  ReferenceAxis = -> Sketch050 [N_Axis]
  Refine = true
  Suppressed = false
  Type = 0
FEATURE [Sketcher::SketchObject] Sketch051
  ArcFitTolerance = 1e-06
  AttachmentOffset = pos=(0,0,14) rot=(0,0,1;0rad)
  AttachmentSupport = -> [XY_Plane023]
  ExternalGeometry = -> [Pad009]
  FullyConstrained = false
  MakeInternals = false
  MapMode = 5
  Placement = pos=(0,0,14) rot=(0,0,1;0rad)
  sketch-geometry (10):
    g0: LineSegment StartX=-13.75 StartY=-28.5 StartZ=0 EndX=13.75 EndY=-28.5 EndZ=0
    g1: LineSegment StartX=13.75 StartY=-28.5 StartZ=0 EndX=13.75 EndY=-28 EndZ=0
    g2: LineSegment StartX=13.75 StartY=-28 StartZ=0 EndX=11.5 EndY=-28 EndZ=0
    g3: LineSegment StartX=-13.75 StartY=-28 StartZ=0 EndX=-13.75 EndY=-28.5 EndZ=0
    g4: LineSegment StartX=11.5 StartY=-28 StartZ=0 EndX=-13.75 EndY=-28 EndZ=0
    g5: LineSegment StartX=-13.75 StartY=28.5 StartZ=0 EndX=13.75 EndY=28.5 EndZ=0
    g6: LineSegment StartX=13.75 StartY=28.5 StartZ=0 EndX=13.75 EndY=28 EndZ=0
    g7: LineSegment StartX=13.75 StartY=28 StartZ=0 EndX=11.5 EndY=28 EndZ=0
    g8: LineSegment StartX=-13.75 StartY=28 StartZ=0 EndX=-13.75 EndY=28.5 EndZ=0
    g9: LineSegment StartX=11.5 StartY=28 StartZ=0 EndX=-13.75 EndY=28 EndZ=0
  constraints (20):
    c: Coincident(g0,g1)
    c: Coincident(g1,g2)
    c: Coincident(g4,g3)
    c: Coincident(g3,g0)
    c: Horizontal(g0)
    c: Vertical(g1)
    c: Vertical(g3)
    c: PointOnObject(g0,g-4)
    c: DistanceX(g4,g2) = 27.5
    c: Symmetric(g4,g1,g-2)
    c: DistanceY(g1,g1) = 0.5
    c: Coincident(g2,g4)
    c: Coincident(g5,g6)
    c: Coincident(g6,g7)
    c: Coincident(g9,g8)
    c: Coincident(g8,g5)
    c: Horizontal(g5)
    c: Vertical(g6)
    c: Vertical(g8)
    c: Coincident(g7,g9)
FEATURE [PartDesign::Pocket] Pocket020  label="Terminal Cutout"
  BaseFeature = -> Pad009
  Direction = (0,0,-1)
  Length = 19
  Length2 = 5
  Profile = -> Sketch051
  ReferenceAxis = -> Sketch051 [N_Axis]
  Refine = true
  Suppressed = false
  Type = 0
FEATURE [Sketcher::SketchObject] Sketch052
  ArcFitTolerance = 1e-06
  AttachmentSupport = -> [XY_Plane023]
  FullyConstrained = false
  MakeInternals = false
  MapMode = 5
  sketch-geometry (8):
    g0: LineSegment StartX=11.5 StartY=-28 StartZ=0 EndX=11.5 EndY=-23.9819 EndZ=0
    g1: LineSegment StartX=11.5 StartY=-23.9819 StartZ=0 EndX=-11.5 EndY=-23.9819 EndZ=0
    g2: LineSegment StartX=-11.5 StartY=-23.9819 StartZ=0 EndX=-11.5 EndY=-28 EndZ=0
    g3: LineSegment StartX=-11.5 StartY=-28 StartZ=0 EndX=11.5 EndY=-28 EndZ=0
    g4: LineSegment StartX=11.5 StartY=28 StartZ=0 EndX=11.5 EndY=23.9819 EndZ=0
    g5: LineSegment StartX=11.5 StartY=23.9819 StartZ=0 EndX=-11.5 EndY=23.9819 EndZ=0
    g6: LineSegment StartX=-11.5 StartY=23.9819 StartZ=0 EndX=-11.5 EndY=28 EndZ=0
    g7: LineSegment StartX=-11.5 StartY=28 StartZ=0 EndX=11.5 EndY=28 EndZ=0
  constraints (16):
    c: Coincident(g0,g1)
    c: Coincident(g1,g2)
    c: Vertical(g0)
    c: Vertical(g2)
    c: DistanceX(g1,g1) = 23
    c: Symmetric(g1,g0,g-2)
    c: Coincident(g3,g2)
    c: Coincident(g3,g0)
    c: Horizontal(g3)
    c: Coincident(g4,g5)
    c: Coincident(g5,g6)
    c: Vertical(g4)
    c: Vertical(g6)
    c: Coincident(g7,g6)
    c: Coincident(g7,g4)
    c: Horizontal(g7)
FEATURE [PartDesign::Pocket] Pocket021  label="Double Contact Cutout"
  BaseFeature = -> Pocket020
  Direction = (0,0,-1)
  Length = 25
  Length2 = 5
  Profile = -> Sketch052
  ReferenceAxis = -> Sketch052 [N_Axis]
  Refine = true
  Reversed = true
  Suppressed = false
  Type = 0
FEATURE [Sketcher::SketchObject] Sketch053
  ArcFitTolerance = 1e-06
  AttachmentOffset = pos=(0,0,25) rot=(0,0,1;0rad)
  AttachmentSupport = -> [XZ_Plane023]
  ExternalGeometry = -> [Pocket021]
  FullyConstrained = false
  MakeInternals = false
  MapMode = 5
  Placement = pos=(0,-25,5.6e-15) rot=(1,0,0;1.5708rad)
  sketch-geometry (6):
    g0: LineSegment StartX=13.75 StartY=0.5 StartZ=0 EndX=11.5 EndY=2.75 EndZ=0
    g1: LineSegment StartX=11.5 StartY=2.75 StartZ=0 EndX=11.5 EndY=0.5 EndZ=0
    g2: LineSegment StartX=11.5 StartY=0.5 StartZ=0 EndX=13.75 EndY=0.5 EndZ=0
    g3: LineSegment StartX=-13.75 StartY=0.5 StartZ=0 EndX=-11.5 EndY=2.75 EndZ=0
    g4: LineSegment StartX=-11.5 StartY=2.75 StartZ=0 EndX=-11.5 EndY=0.5 EndZ=0
    g5: LineSegment StartX=-11.5 StartY=0.5 StartZ=0 EndX=-13.75 EndY=0.5 EndZ=0
  constraints (12):
    c: Coincident(g-3,g0)
    c: Coincident(g0,g1)
    c: Coincident(g1,g-3)
    c: Vertical(g1)
    c: Coincident(g1,g2)
    c: Coincident(g2,g0)
    c: Angle(g0,g2) = 0.785398
    c: Coincident(g3,g4)
    c: Vertical(g4)
    c: Coincident(g4,g5)
    c: Coincident(g5,g3)
    c: Angle(g3,g5) = -0.785398
FEATURE [PartDesign::Pocket] Pocket022  label="Double Contact Corners"
  BaseFeature = -> Pocket021
  Direction = (0,1,-2e-16)
  Length = 3
  Length2 = 5
  Profile = -> Sketch053
  ReferenceAxis = -> Sketch053 [N_Axis]
  Refine = true
  Reversed = true
  Suppressed = false
  Type = 0
FEATURE [Sketcher::SketchObject] Sketch054
  ArcFitTolerance = 1e-06
  AttachmentSupport = -> [YZ_Plane023]
  ExternalGeometry = -> [Pocket022]
  FullyConstrained = false
  MakeInternals = false
  MapMode = 5
  Placement = pos=(0,0,0) rot=(0.57735,0.57735,0.57735;2.0944rad)
  sketch-geometry (2):
    g0: LineSegment StartX=-28.0325 StartY=9 StartZ=0 EndX=-28.0325 EndY=7 EndZ=0
    g1: ArcOfCircle CenterX=-28.0325 CenterY=8 CenterZ=0 NormalX=0 NormalY=0 NormalZ=1 AngleXU=0 Radius=1 StartAngle=4.71239 EndAngle=7.85398
  constraints (6):
    c: Vertical(g0)
    c: Coincident(g1,g0)
    c: DistanceY(g0,g0) = 2
    c: DistanceY(g0,g-4) = 5
    c: DistanceY(g-5,g0) = 4.7
    c: Coincident(g0,g1)
FEATURE [PartDesign::Pocket] Pocket023  label="Double Dimple"
  BaseFeature = -> Pocket022
  Direction = (-1,0,0)
  Length = 30
  Length2 = 5
  Midplane = true
  Profile = -> Sketch054
  ReferenceAxis = -> Sketch054 [N_Axis]
  Refine = true
  Suppressed = false
  Type = 0
FEATURE [Sketcher::SketchObject] Sketch055
  ArcFitTolerance = 1e-06
  AttachmentSupport = -> [YZ_Plane023]
  FullyConstrained = false
  MakeInternals = false
  MapMode = 5
  Placement = pos=(0,0,0) rot=(0.57735,0.57735,0.57735;2.0944rad)
  sketch-geometry (4):
    g0: LineSegment StartX=28.5 StartY=15.3 StartZ=0 EndX=26.2 EndY=15.3 EndZ=0
    g1: LineSegment StartX=26.2 StartY=15.3 StartZ=0 EndX=26.2 EndY=2.3 EndZ=0
    g2: LineSegment StartX=26.2 StartY=2.3 StartZ=0 EndX=28.5 EndY=0 EndZ=0
    g3: LineSegment StartX=28.5 StartY=15.3 StartZ=0 EndX=28.5 EndY=0 EndZ=0
  constraints (9):
    c: Horizontal(g0)
    c: Coincident(g0,g1)
    c: Vertical(g1)
    c: Coincident(g1,g2)
    c: Coincident(g0,g3)
    c: Coincident(g3,g2)
    c: Distance(g0,g0) = 2.3
    c: Vertical(g3)
    c: DistanceY(g1,g1) = 13
FEATURE [PartDesign::Pad] Pad010
  BaseFeature = -> Pocket023
  Direction = (1,0,0)
  Length = 2.8
  Length2 = 10
  Midplane = true
  Profile = -> Sketch055
  ReferenceAxis = -> Sketch055 [N_Axis]
  Refine = true
  Suppressed = false
  Type = 0
FEATURE [Sketcher::SketchObject] Sketch056
  ArcFitTolerance = 1e-06
  AttachmentSupport = -> [YZ_Plane023]
  ExternalGeometry = -> [Pad010]
  FullyConstrained = true
  MakeInternals = false
  MapMode = 5
  Placement = pos=(0,0,0) rot=(0.57735,0.57735,0.57735;2.0944rad)
  sketch-geometry (5):
    g0: LineSegment StartX=28 StartY=14 StartZ=0 EndX=28 EndY=0.5 EndZ=0
    g1: LineSegment StartX=28 StartY=0.5 StartZ=0 EndX=26.2 EndY=2.3 EndZ=0
    g2: LineSegment StartX=26.2 StartY=2.3 StartZ=0 EndX=26.2 EndY=15.3 EndZ=0
    g3: LineSegment StartX=26.2 StartY=15.3 StartZ=0 EndX=28 EndY=15.3 EndZ=0
    g4: LineSegment StartX=28 StartY=15.3 StartZ=0 EndX=28 EndY=14 EndZ=0
  constraints (11):
    c: Coincident(g-3,g0)
    c: PointOnObject(g0,g-5)
    c: Vertical(g0)
    c: Coincident(g0,g1)
    c: Coincident(g1,g-5)
    c: Coincident(g1,g2)
    c: Coincident(g2,g-4)
    c: Coincident(g2,g3)
    c: Coincident(g3,g-3)
    c: Coincident(g3,g4)
    c: Coincident(g4,g0)
FEATURE [PartDesign::Pad] Pad011
  BaseFeature = -> Pad010
  Direction = (1,0,0)
  Length = 5
  Length2 = 10
  Midplane = true
  Profile = -> Sketch056
  ReferenceAxis = -> Sketch056 [N_Axis]
  Refine = true
  Suppressed = false
  Type = 0
FEATURE [Sketcher::SketchObject] Sketch057
  ArcFitTolerance = 1e-06
  AttachmentSupport = -> [YZ_Plane023]
  FullyConstrained = false
  MakeInternals = false
  MapMode = 5
  Placement = pos=(0,0,0) rot=(0.57735,0.57735,0.57735;2.0944rad)
  sketch-geometry (4):
    g0: LineSegment [constr] StartX=-28.0325 StartY=9 StartZ=0 EndX=-28.0325 EndY=7 EndZ=0
    g1: ArcOfCircle [constr] CenterX=-28.0325 CenterY=8 CenterZ=0 NormalX=0 NormalY=0 NormalZ=1 AngleXU=0 Radius=1 StartAngle=4.71239 EndAngle=7.85398
    g2: LineSegment StartX=28.0325 StartY=9 StartZ=0 EndX=28.0325 EndY=7 EndZ=0
    g3: ArcOfCircle CenterX=28.0325 CenterY=8 CenterZ=0 NormalX=0 NormalY=0 NormalZ=1 AngleXU=0 Radius=1 StartAngle=1.5708 EndAngle=4.71239
  constraints (7):
    c: Vertical(g0)
    c: Coincident(g1,g0)
    c: DistanceY(g0,g0) = 2
    c: Coincident(g0,g1)
    c: Vertical(g2)
    c: Coincident(g3,g2)
    c: Coincident(g2,g3)
FEATURE [PartDesign::Pocket] Pocket024
  BaseFeature = -> Pad011
  Direction = (-1,0,0)
  Length = 31
  Length2 = 5
  Midplane = true
  Profile = -> Sketch057
  ReferenceAxis = -> Sketch057 [N_Axis]
  Refine = true
  Suppressed = false
  Type = 0
FEATURE [Sketcher::SketchObject] Sketch058
  ArcFitTolerance = 1e-06
  AttachmentOffset = pos=(0,0,-27) rot=(0,0,1;0rad)
  AttachmentSupport = -> [XZ_Plane023]
  ExternalGeometry = -> [Pocket024]
  FullyConstrained = false
  MakeInternals = false
  MapMode = 5
  Placement = pos=(0,27,-6e-15) rot=(1,0,0;1.5708rad)
  sketch-geometry (8):
    g0: LineSegment StartX=-5 StartY=14 StartZ=0 EndX=-5 EndY=17.3416 EndZ=0
    g1: LineSegment StartX=-5 StartY=17.3416 StartZ=0 EndX=-9 EndY=17.3416 EndZ=0
    g2: LineSegment StartX=-9 StartY=17.3416 StartZ=0 EndX=-9 EndY=14 EndZ=0
    g3: LineSegment StartX=-9 StartY=14 StartZ=0 EndX=-5 EndY=14 EndZ=0
    g4: LineSegment StartX=5 StartY=14 StartZ=0 EndX=5 EndY=17.3416 EndZ=0
    g5: LineSegment StartX=5 StartY=17.3416 StartZ=0 EndX=9 EndY=17.3416 EndZ=0
    g6: LineSegment StartX=9 StartY=17.3416 StartZ=0 EndX=9 EndY=14 EndZ=0
    g7: LineSegment StartX=9 StartY=14 StartZ=0 EndX=5 EndY=14 EndZ=0
  constraints (21):
    c: DistanceY(g-1,g-7) = 14
    c: Coincident(g0,g1)
    c: Coincident(g1,g2)
    c: Coincident(g2,g3)
    c: Coincident(g3,g0)
    c: Vertical(g0)
    c: Vertical(g2)
    c: Horizontal(g1)
    c: Horizontal(g3)
    c: PointOnObject(g0,g-8)
    c: DistanceX(g1,g1) = 4
    c: DistanceX(g-6,g-5) = 9
    c: DistanceX(g0,g-5) = 2.5
    c: Coincident(g4,g5)
    c: Coincident(g5,g6)
    c: Coincident(g6,g7)
    c: Coincident(g7,g4)
    c: Vertical(g4)
    c: Vertical(g6)
    c: Horizontal(g5)
    c: Horizontal(g7)
FEATURE [PartDesign::Pocket] Pocket025
  BaseFeature = -> Pocket024
  Direction = (0,1,-2e-16)
  Length = 5
  Length2 = 5
  Profile = -> Sketch058
  ReferenceAxis = -> Sketch058 [N_Axis]
  Refine = true
  Suppressed = false
  Type = 0
FEATURE [Sketcher::SketchObject] Sketch059
  ArcFitTolerance = 1e-06
  AttachmentOffset = pos=(0,0,-26) rot=(0,0,1;0rad)
  AttachmentSupport = -> [XZ_Plane023]
  ExternalGeometry = -> [Pocket025]
  FullyConstrained = false
  MakeInternals = false
  MapMode = 5
  Placement = pos=(0,26,-5.8e-15) rot=(1,0,0;1.5708rad)
  sketch-geometry (12):
    g0: LineSegment StartX=13.75 StartY=0.5 StartZ=0 EndX=11.5 EndY=2.75 EndZ=0
    g1: LineSegment StartX=11.5 StartY=2.75 StartZ=0 EndX=11.5 EndY=0.5 EndZ=0
    g2: LineSegment StartX=11.5 StartY=0.5 StartZ=0 EndX=13.75 EndY=0.5 EndZ=0
    g3: LineSegment StartX=-13.75 StartY=0.5 StartZ=0 EndX=-11.5 EndY=2.75 EndZ=0
    g4: LineSegment StartX=-11.5 StartY=2.75 StartZ=0 EndX=-11.5 EndY=0.5 EndZ=0
    g5: LineSegment StartX=-11.5 StartY=0.5 StartZ=0 EndX=-13.75 EndY=0.5 EndZ=0
    g6: LineSegment StartX=-1.4 StartY=0.5 StartZ=0 EndX=-2.5 EndY=1.6 EndZ=0
    g7: LineSegment StartX=-2.5 StartY=1.6 StartZ=0 EndX=-2.5 EndY=0.5 EndZ=0
    g8: LineSegment StartX=-2.5 StartY=0.5 StartZ=0 EndX=-1.4 EndY=0.5 EndZ=0
    g9: LineSegment StartX=1.4 StartY=0.5 StartZ=0 EndX=2.5 EndY=1.6 EndZ=0
    g10: LineSegment StartX=2.5 StartY=1.6 StartZ=0 EndX=2.5 EndY=0.5 EndZ=0
    g11: LineSegment StartX=2.5 StartY=0.5 StartZ=0 EndX=1.4 EndY=0.5 EndZ=0
  constraints (21):
    c: Coincident(g0,g1)
    c: Vertical(g1)
    c: Coincident(g1,g2)
    c: Coincident(g2,g0)
    c: Angle(g0,g2) = 0.785398
    c: Coincident(g3,g4)
    c: Vertical(g4)
    c: Coincident(g4,g5)
    c: Coincident(g5,g3)
    c: Angle(g3,g5) = -0.785398
    c: Coincident(g-3,g6)
    c: PointOnObject(g6,g-4)
    c: Coincident(g6,g7)
    c: Coincident(g7,g-4)
    c: Coincident(g7,g8)
    c: Coincident(g8,g6)
    c: Angle(g6,g8) = 0.785398
    c: Coincident(g9,g10)
    c: Coincident(g10,g11)
    c: Coincident(g11,g9)
    c: Angle(g9,g11) = -0.785398
FEATURE [PartDesign::Pocket] Pocket026
  BaseFeature = -> Pocket025
  Direction = (0,1,-2e-16)
  Length = 2
  Length2 = 5
  Profile = -> Sketch059
  ReferenceAxis = -> Sketch059 [N_Axis]
  Refine = true
  Suppressed = false
  Type = 0
FEATURE [PartDesign::Body] Body010  label="BatteryContactTest"
  AllowCompound = true
  Group = -> [Sketch049,Pad008,Sketch050,Pad009,Sketch051,Pocket020,Sketch052,Pocket021,Sketch053,Pocket022,Sketch054,Pocket023,Sketch055,Pad010,Sketch056,Pad011,Sketch057,Pocket024,Sketch058,Pocket025,Sketch059,Pocket026]
  Origin = -> Origin023
  Tip = -> Pocket026
FEATURE [Sketcher::SketchObject] Sketch060
  ArcFitTolerance = 1e-06
  AttachmentSupport = -> [YZ_Plane001]
  ExternalGeometry = -> [Pocket019]
  FullyConstrained = false
  MakeInternals = false
  MapMode = 5
  Placement = pos=(0,0,0) rot=(0.57735,0.57735,0.57735;2.0944rad)
  sketch-geometry (6):
    g0: LineSegment StartX=-51.46 StartY=6.1181 StartZ=0 EndX=-51.46 EndY=-7.00052 EndZ=0
    g1: LineSegment StartX=-51.46 StartY=-7.00052 StartZ=0 EndX=-51.46 EndY=-7.00052 EndZ=0
    g2: LineSegment StartX=-49.46 StartY=-6.8819 StartZ=0 EndX=-49.46 EndY=6.1181 EndZ=0
    g3: LineSegment StartX=-49.46 StartY=6.1181 StartZ=0 EndX=-51.46 EndY=6.1181 EndZ=0
    g4: LineSegment StartX=-49.46 StartY=-6.8819 StartZ=0 EndX=-51.46 EndY=-8.8819 EndZ=0
    g5: LineSegment StartX=-51.46 StartY=-8.8819 StartZ=0 EndX=-51.46 EndY=-7.00052 EndZ=0
  constraints (17):
    c: Coincident(g0,g1)
    c: Coincident(g2,g3)
    c: Coincident(g3,g0)
    c: Vertical(g0)
    c: Horizontal(g1)
    c: Horizontal(g3)
    c: PointOnObject(g0,g-3)
    c: DistanceY(g2,g2) = 13
    c: DistanceX(g3,g3) = 2
    c: Coincident(g2,g4)
    c: PointOnObject(g4,g-3)
    c: Coincident(g4,g5)
    c: Coincident(g5,g0)
    c: PointOnObject(g1,g5)
    c: Angle(g2,g4) = 2.35619
    c: Vertical(g2)
    c: DistanceY(g0,g-4) = 0.482592
FEATURE [PartDesign::Pad] Pad012  label="Double Battery Support"
  BaseFeature = -> Pocket019
  Direction = (1,0,0)
  Length = 30
  Length2 = 10
  Midplane = true
  Profile = -> Sketch060
  ReferenceAxis = -> Sketch060 [N_Axis]
  Refine = true
  Suppressed = false
  Type = 0
FEATURE [Sketcher::SketchObject] Sketch061
  ArcFitTolerance = 1e-06
  AttachmentSupport = -> [XY_Plane001]
  ExternalGeometry = -> [Pad012]
  FullyConstrained = true
  MakeInternals = false
  MapMode = 5
  sketch-geometry (8):
    g0: LineSegment StartX=-12.5 StartY=-49.46 StartZ=0 EndX=-12.5 EndY=-50.46 EndZ=0
    g1: LineSegment StartX=12.5 StartY=-50.46 StartZ=0 EndX=12.5 EndY=-49.46 EndZ=0
    g2: LineSegment StartX=12.5 StartY=-49.46 StartZ=0 EndX=-12.5 EndY=-49.46 EndZ=0
    g3: LineSegment StartX=-14.25 StartY=-50.46 StartZ=0 EndX=-14.25 EndY=-51.56 EndZ=0
    g4: LineSegment StartX=-14.25 StartY=-51.56 StartZ=0 EndX=14.25 EndY=-51.56 EndZ=0
    g5: LineSegment StartX=14.25 StartY=-51.56 StartZ=0 EndX=14.25 EndY=-50.46 EndZ=0
    g6: LineSegment StartX=-12.5 StartY=-50.46 StartZ=0 EndX=-14.25 EndY=-50.46 EndZ=0
    g7: LineSegment StartX=12.5 StartY=-50.46 StartZ=0 EndX=14.25 EndY=-50.46 EndZ=0
  constraints (23):
    c: Coincident(g1,g2)
    c: Coincident(g2,g0)
    c: Vertical(g0)
    c: Vertical(g1)
    c: PointOnObject(g0,g-3)
    c: Symmetric(g0,g1,g-2)
    c: DistanceX(g2,g2) = 25
    c: DistanceY(g1,g1) = 1
    c: Coincident(g3,g4)
    c: Coincident(g4,g5)
    c: Coincident(g6,g3)
    c: Vertical(g3)
    c: Vertical(g5)
    c: Horizontal(g4)
    c: Horizontal(g3,g0)
    c: Symmetric(g3,g5,g-2)
    c: DistanceY(g5,g5) = 1.1
    c: DistanceX(g4,g4) = 28.5
    c: Coincident(g7,g1)
    c: Coincident(g7,g5)
    c: Horizontal(g7)
    c: Coincident(g0,g6)
    c: DistanceY(g4,g-1) = 51.56
FEATURE [PartDesign::Pocket] Pocket027  label="Double Battery Cutout"
  BaseFeature = -> Pad012
  Direction = (0,0,-1)
  Length = 13
  Length2 = 5
  Midplane = true
  Profile = -> Sketch061
  ReferenceAxis = -> Sketch061 [N_Axis]
  Refine = true
  Suppressed = false
  Type = 0
FEATURE [Sketcher::SketchObject] Sketch062
  ArcFitTolerance = 1e-06
  AttachmentOffset = pos=(0,0,6) rot=(0,0,1;0rad)
  AttachmentSupport = -> [XY_Plane001]
  FullyConstrained = false
  MakeInternals = false
  MapMode = 5
  Placement = pos=(0,0,6) rot=(0,0,1;0rad)
  sketch-geometry (6):
    g0: LineSegment StartX=-14.25 StartY=-50.4 StartZ=0 EndX=-14.25 EndY=-51.5 EndZ=0
    g1: LineSegment StartX=-14.25 StartY=-51.5 StartZ=0 EndX=14.25 EndY=-51.5 EndZ=0
    g2: LineSegment StartX=14.25 StartY=-51.5 StartZ=0 EndX=14.25 EndY=-50.4 EndZ=0
    g3: LineSegment StartX=-12.5 StartY=-50.4 StartZ=0 EndX=-14.25 EndY=-50.4 EndZ=0
    g4: LineSegment StartX=12.5 StartY=-50.4 StartZ=0 EndX=14.25 EndY=-50.4 EndZ=0
    g5: LineSegment StartX=-12.5 StartY=-50.4 StartZ=0 EndX=12.5 EndY=-50.4 EndZ=0
  constraints (15):
    c: Coincident(g0,g1)
    c: Coincident(g1,g2)
    c: Coincident(g3,g0)
    c: Vertical(g0)
    c: Vertical(g2)
    c: Horizontal(g1)
    c: Symmetric(g0,g2,g-2)
    c: DistanceY(g2,g2) = 1.1
    c: DistanceX(g1,g1) = 28.5
    c: Coincident(g4,g2)
    c: Horizontal(g4)
    c: Coincident(g5,g3)
    c: Coincident(g5,g4)
    c: Horizontal(g5)
    c: DistanceY(g1,g-1) = 51.5
FEATURE [PartDesign::Pocket] Pocket028  label="Double Battery Insert Cutout"
  BaseFeature = -> Pocket027
  Direction = (0,0,-1)
  Length = 3
  Length2 = 5
  Profile = -> Sketch062
  ReferenceAxis = -> Sketch062 [N_Axis]
  Refine = true
  Reversed = true
  Suppressed = false
  Type = 0
FEATURE [Sketcher::SketchObject] Sketch063
  ArcFitTolerance = 1e-06
  AttachmentSupport = -> [YZ_Plane001]
  ExternalGeometry = -> [Pocket028]
  FullyConstrained = false
  MakeInternals = false
  MapMode = 5
  Placement = pos=(0,0,0) rot=(0.57735,0.57735,0.57735;2.0944rad)
  sketch-geometry (4):
    g0: LineSegment StartX=57.54 StartY=6.6007 StartZ=0 EndX=57.54 EndY=-8.8819 EndZ=0
    g1: LineSegment StartX=57.54 StartY=-8.8819 StartZ=0 EndX=55.54 EndY=-6.8819 EndZ=0
    g2: LineSegment StartX=55.54 StartY=-6.8819 StartZ=0 EndX=55.54 EndY=6.6007 EndZ=0
    g3: LineSegment StartX=55.54 StartY=6.6007 StartZ=0 EndX=57.54 EndY=6.6007 EndZ=0
  constraints (11):
    c: Vertical(g0)
    c: Coincident(g0,g1)
    c: Coincident(g1,g2)
    c: Vertical(g2)
    c: Coincident(g2,g3)
    c: Coincident(g3,g0)
    c: Horizontal(g3)
    c: Angle(g1,g2) = 2.35619
    c: DistanceX(g-4,g1) = 105
    c: Horizontal(g-4,g1)
    c: DistanceX(g3,g3) = 2
FEATURE [PartDesign::Pad] Pad013  label="Dual Single Battery Support"
  BaseFeature = -> Pocket028
  Direction = (1,0,0)
  Length = 30
  Length2 = 10
  Midplane = true
  Profile = -> Sketch063
  ReferenceAxis = -> Sketch063 [N_Axis]
  Refine = true
  Suppressed = false
  Type = 0
FEATURE [Sketcher::SketchObject] Sketch064
  ArcFitTolerance = 1e-06
  AttachmentSupport = -> [XY_Plane001]
  ExternalGeometry = -> [Pad013]
  FullyConstrained = false
  MakeInternals = false
  MapMode = 5
  sketch-geometry (36):
    g0: LineSegment [constr] StartX=-12.5 StartY=-49.46 StartZ=0 EndX=-12.5 EndY=-50.46 EndZ=0
    g1: LineSegment [constr] StartX=12.5 StartY=-50.46 StartZ=0 EndX=12.5 EndY=-49.46 EndZ=0
    g2: LineSegment [constr] StartX=12.5 StartY=-49.46 StartZ=0 EndX=-12.5 EndY=-49.46 EndZ=0
    g3: LineSegment [constr] StartX=-14.25 StartY=-50.46 StartZ=0 EndX=-14.25 EndY=-51.56 EndZ=0
    g4: LineSegment [constr] StartX=-14.25 StartY=-51.56 StartZ=0 EndX=14.25 EndY=-51.56 EndZ=0
    g5: LineSegment [constr] StartX=14.25 StartY=-51.56 StartZ=0 EndX=14.25 EndY=-50.46 EndZ=0
    g6: LineSegment [constr] StartX=-12.5 StartY=-50.46 StartZ=0 EndX=-14.25 EndY=-50.46 EndZ=0
    g7: LineSegment [constr] StartX=12.5 StartY=-50.46 StartZ=0 EndX=14.25 EndY=-50.46 EndZ=0
    g8: LineSegment StartX=-3 StartY=55.54 StartZ=0 EndX=-3 EndY=56.54 EndZ=0
    g9: LineSegment StartX=-12 StartY=56.54 StartZ=0 EndX=-12 EndY=55.54 EndZ=0
    g10: LineSegment StartX=-12 StartY=55.54 StartZ=0 EndX=-3 EndY=55.54 EndZ=0
    g11: LineSegment StartX=-14 StartY=57.64 StartZ=0 EndX=-14 EndY=56.54 EndZ=0
    g12: LineSegment StartX=-14 StartY=56.54 StartZ=0 EndX=-12 EndY=56.54 EndZ=0
    g13: LineSegment StartX=-3 StartY=56.54 StartZ=0 EndX=-1 EndY=56.54 EndZ=0
    g14: LineSegment StartX=-1 StartY=57.64 StartZ=0 EndX=-1 EndY=56.54 EndZ=0
    g15: LineSegment StartX=-14 StartY=57.64 StartZ=0 EndX=-9 EndY=57.64 EndZ=0
    g16: LineSegment StartX=-1 StartY=57.64 StartZ=0 EndX=-6 EndY=57.64 EndZ=0
    g17: ArcOfCircle CenterX=-5.27457 CenterY=57.8893 CenterZ=0 NormalX=0 NormalY=0 NormalZ=1 AngleXU=0 Radius=0.76706 StartAngle=1.8666 EndAngle=3.47258
    g18: ArcOfCircle CenterX=-8.19795 CenterY=57.64 CenterZ=0 NormalX=0 NormalY=0 NormalZ=1 AngleXU=0 Radius=0.802053 StartAngle=3.13046 EndAngle=3.14159
    g19: LineSegment StartX=-8.99995 StartY=57.6489 StartZ=0 EndX=-8.92397 EndY=64.4737 EndZ=0
    g20: LineSegment StartX=-5.49818 StartY=58.623 StartZ=0 EndX=0 EndY=60.2986 EndZ=0
    g21: LineSegment StartX=-8.92397 StartY=64.4737 StartZ=0 EndX=0 EndY=71.4039 EndZ=0
    g22: LineSegment StartX=3 StartY=55.54 StartZ=0 EndX=3 EndY=56.54 EndZ=0
    g23: LineSegment StartX=12 StartY=56.54 StartZ=0 EndX=12 EndY=55.54 EndZ=0
    g24: LineSegment StartX=12 StartY=55.54 StartZ=0 EndX=3 EndY=55.54 EndZ=0
    g25: LineSegment StartX=14 StartY=57.64 StartZ=0 EndX=14 EndY=56.54 EndZ=0
    g26: LineSegment StartX=14 StartY=56.54 StartZ=0 EndX=12 EndY=56.54 EndZ=0
    g27: LineSegment StartX=3 StartY=56.54 StartZ=0 EndX=1 EndY=56.54 EndZ=0
    g28: LineSegment StartX=1 StartY=57.64 StartZ=0 EndX=1 EndY=56.54 EndZ=0
    g29: LineSegment StartX=14 StartY=57.64 StartZ=0 EndX=9.02184 EndY=57.64 EndZ=0
    g30: LineSegment StartX=1 StartY=57.64 StartZ=0 EndX=6.01036 EndY=57.64 EndZ=0
    g31: ArcOfCircle CenterX=5.28012 CenterY=57.8878 CenterZ=0 NormalX=0 NormalY=0 NormalZ=1 AngleXU=0 Radius=0.771129 StartAngle=5.9561 EndAngle=7.55891
    g32: ArcOfCircle CenterX=8.2227 CenterY=57.679 CenterZ=0 NormalX=0 NormalY=0 NormalZ=1 AngleXU=0 Radius=0.8001 StartAngle=6.23438 EndAngle=6.27458
    g33: LineSegment StartX=9.02277 StartY=57.6722 StartZ=0 EndX=9.0785 EndY=64.148 EndZ=0
    g34: LineSegment StartX=5.50437 StartY=58.6256 StartZ=0 EndX=0 EndY=60.2986 EndZ=0
    g35: LineSegment StartX=9.0785 StartY=64.148 StartZ=0 EndX=0 EndY=71.4039 EndZ=0
  constraints (85):
    c: Coincident(g1,g2)
    c: Coincident(g2,g0)
    c: Vertical(g0)
    c: Vertical(g1)
    c: Symmetric(g0,g1,g-2)
    c: DistanceX(g2,g2) = 25
    c: DistanceY(g1,g1) = 1
    c: Coincident(g3,g4)
    c: Coincident(g4,g5)
    c: Coincident(g6,g3)
    c: Vertical(g3)
    c: Vertical(g5)
    c: Horizontal(g4)
    c: Horizontal(g3,g0)
    c: Symmetric(g3,g5,g-2)
    c: DistanceY(g5,g5) = 1.1
    c: DistanceX(g4,g4) = 28.5
    c: Coincident(g7,g1)
    c: Coincident(g7,g5)
    c: Horizontal(g7)
    c: Coincident(g0,g6)
    c: DistanceY(g4,g-1) = 51.56
    c: DistanceY(g-1,g-3) = 55.54
    c: Coincident(g9,g10)
    c: Coincident(g10,g8)
    c: Vertical(g8)
    c: Vertical(g9)
    c: Horizontal(g10)
    c: PointOnObject(g8,g-3)
    c: Coincident(g11,g12)
    c: Vertical(g11)
    c: Horizontal(g12)
    c: Horizontal(g8,g13)
    c: DistanceY(g11,g11) = 1.1
    c: DistanceY(g-3,g11) = 1
    c: PointOnObject(g12,g9)
    c: PointOnObject(g13,g8)
    c: Horizontal(g13)
    c: Coincident(g14,g13)
    c: Vertical(g14)
    c: Distance(g14,g-2) = 1
    c: DistanceX(g11,g13) = 13
    c: DistanceX(g8,g13) = 2
    c: DistanceX(g11,g9) = 2
    c: Coincident(g15,g11)
    c: Horizontal(g15)
    c: Horizontal(g11,g14)
    c: Coincident(g16,g14)
    c: Horizontal(g16)
    c: DistanceX(g15,g16) = 3
    c: Coincident(g17,g16)
    c: Coincident(g18,g15)
    c: DistanceX(g11,g15) = 5
    c: Horizontal(g15,g18)
    c: Tangent(g19,g18) = 1.5708
    c: PointOnObject(g20,g-2)
    c: Tangent(g20,g17) = 1.5708
    c: Coincident(g21,g19)
    c: PointOnObject(g21,g-2)
    c: Coincident(g23,g24)
    c: Coincident(g24,g22)
    c: Vertical(g22)
    c: Vertical(g23)
    c: Horizontal(g24)
    c: Coincident(g25,g26)
    c: Vertical(g25)
    c: Horizontal(g26)
    c: PointOnObject(g26,g23)
    c: PointOnObject(g27,g22)
    c: Horizontal(g27)
    c: Coincident(g28,g27)
    c: Vertical(g28)
    c: Coincident(g29,g25)
    c: Horizontal(g29)
    c: Coincident(g30,g28)
    c: Horizontal(g30)
    c: Coincident(g31,g30)
    c: Coincident(g32,g29)
    c: Tangent(g33,g32) = -1.5708
    c: Tangent(g34,g31) = -1.5708
    c: Coincident(g35,g33)
    c: Coincident(g20,g34)
    c: Coincident(g21,g35)
    c: Horizontal(g14,g28)
    c: Horizontal(g30,g29)
FEATURE [PartDesign::Pocket] Pocket029  label="Dual Single Batt Cutout"
  BaseFeature = -> Pad013
  Direction = (0,0,-1)
  Length = 12
  Length2 = 5
  Midplane = true
  Profile = -> Sketch064
  ReferenceAxis = -> Sketch064 [N_Axis]
  Refine = true
  Suppressed = false
  Type = 0
FEATURE [Sketcher::SketchObject] Sketch065  label="Fix me"
  ArcFitTolerance = 1e-06
  AttachmentOffset = pos=(0,0,4) rot=(0,0,1;0rad)
  AttachmentSupport = -> [XY_Plane001]
  ExternalGeometry = -> [Pocket029]
  FullyConstrained = false
  MakeInternals = false
  MapMode = 5
  Placement = pos=(0,0,4) rot=(0,0,1;0rad)
  sketch-geometry (26):
    g0: LineSegment StartX=-14 StartY=57.64 StartZ=0 EndX=-14 EndY=56.54 EndZ=0
    g1: LineSegment StartX=-14 StartY=56.54 StartZ=0 EndX=-12 EndY=56.54 EndZ=0
    g2: LineSegment StartX=14 StartY=56.54 StartZ=0 EndX=14 EndY=57.6722 EndZ=0
    g3: LineSegment StartX=-3 StartY=55.54 StartZ=0 EndX=-3 EndY=56.54 EndZ=0
    g4: LineSegment StartX=-12 StartY=56.54 StartZ=0 EndX=-12 EndY=55.54 EndZ=0
    g5: LineSegment StartX=-12 StartY=55.54 StartZ=0 EndX=-3 EndY=55.54 EndZ=0
    g6: LineSegment StartX=12 StartY=55.54 StartZ=0 EndX=12 EndY=56.54 EndZ=0
    g7: LineSegment StartX=3 StartY=56.54 StartZ=0 EndX=3 EndY=55.54 EndZ=0
    g8: LineSegment StartX=3 StartY=55.54 StartZ=0 EndX=12 EndY=55.54 EndZ=0
    g9: LineSegment StartX=12 StartY=56.54 StartZ=0 EndX=14 EndY=56.54 EndZ=0
    g10: LineSegment StartX=-14 StartY=57.64 StartZ=0 EndX=-8.99995 EndY=57.6489 EndZ=0
    g11: LineSegment StartX=9.06551 StartY=57.6722 StartZ=0 EndX=14 EndY=57.6722 EndZ=0
    g12: LineSegment StartX=-3 StartY=56.54 StartZ=0 EndX=-1 EndY=56.54 EndZ=0
    g13: LineSegment StartX=-1 StartY=56.54 StartZ=0 EndX=-1 EndY=57.64 EndZ=0
    g14: LineSegment StartX=-1 StartY=57.64 StartZ=0 EndX=-6 EndY=57.64 EndZ=0
    g15: LineSegment StartX=-6 StartY=57.64 StartZ=0 EndX=-5.49818 EndY=58.623 EndZ=0
    g16: LineSegment StartX=1 StartY=57.64 StartZ=0 EndX=1 EndY=56.54 EndZ=0
    g17: LineSegment StartX=1 StartY=56.54 StartZ=0 EndX=3 EndY=56.54 EndZ=0
    g18: LineSegment StartX=1 StartY=57.64 StartZ=0 EndX=6.01036 EndY=57.64 EndZ=0
    g19: LineSegment StartX=6.01036 StartY=57.64 StartZ=0 EndX=5.54541 EndY=58.6268 EndZ=0
    g20: LineSegment StartX=-8.99995 StartY=62.4726 StartZ=0 EndX=0 EndY=62.4106 EndZ=0
    g21: LineSegment StartX=0 StartY=62.4106 StartZ=0 EndX=9.06551 EndY=62.4726 EndZ=0
    g22: LineSegment StartX=-8.99995 StartY=62.4726 StartZ=0 EndX=-8.99995 EndY=57.6489 EndZ=0
    g23: LineSegment StartX=9.06551 StartY=62.4726 StartZ=0 EndX=9.06551 EndY=57.6722 EndZ=0
    g24: LineSegment StartX=-5.49818 StartY=58.623 StartZ=0 EndX=0 EndY=60.0901 EndZ=0
    g25: LineSegment StartX=0 StartY=60.0901 StartZ=0 EndX=5.54541 EndY=58.6268 EndZ=0
  constraints (56):
    c: Coincident(g0,g1)
    c: Coincident(g9,g2)
    c: Vertical(g0)
    c: Vertical(g2)
    c: Horizontal(g1)
    c: Coincident(g0,g-3)
    c: Coincident(g9,g-4)
    c: Coincident(g4,g5)
    c: Coincident(g5,g3)
    c: Vertical(g3)
    c: Vertical(g4)
    c: Horizontal(g5)
    c: Coincident(g3,g-5)
    c: Coincident(g7,g8)
    c: Coincident(g8,g6)
    c: Vertical(g6)
    c: Vertical(g7)
    c: Coincident(g6,g-8)
    c: Coincident(g7,g-7)
    c: Coincident(g0,g10)
    c: Coincident(g10,g-9)
    c: Coincident(g11,g2)
    c: Horizontal(g11)
    c: Coincident(g3,g12)
    c: Coincident(g12,g-17)
    c: Horizontal(g12)
    c: Coincident(g12,g13)
    c: Coincident(g13,g-21)
    c: Coincident(g13,g14)
    c: Coincident(g14,g-21)
    c: Coincident(g14,g15)
    c: Coincident(g15,g-12)
    c: Coincident(g16,g-18)
    c: Coincident(g16,g17)
    c: Coincident(g17,g7)
    c: Horizontal(g17)
    c: Coincident(g16,g18)
    c: Coincident(g18,g-20)
    c: Horizontal(g18)
    c: Coincident(g18,g19)
    c: Coincident(g1,g4)
    c: Coincident(g1,g-6)
    c: Coincident(g6,g9)
    c: PointOnObject(g20,g-2)
    c: Coincident(g20,g21)
    c: Horizontal(g20,g21)
    c: Coincident(g22,g20)
    c: Coincident(g22,g10)
    c: Vertical(g22)
    c: Coincident(g23,g21)
    c: Coincident(g23,g11)
    c: Vertical(g23)
    c: Coincident(g15,g24)
    c: PointOnObject(g24,g-2)
    c: Coincident(g24,g25)
    c: Coincident(g25,g19)
FEATURE [PartDesign::Pocket] Pocket030
  BaseFeature = -> Pocket029
  Direction = (0,0,-1)
  Length = 5
  Length2 = 5
  Profile = -> Sketch065
  ReferenceAxis = -> Sketch065 [N_Axis]
  Refine = true
  Reversed = true
  Suppressed = false
  Type = 0
FEATURE [Sketcher::SketchObject] Sketch066
  ArcFitTolerance = 1e-06
  AttachmentOffset = pos=(0,0,7) rot=(0,0,1;0rad)
  AttachmentSupport = -> [XY_Plane001]
  FullyConstrained = false
  MakeInternals = false
  MapMode = 5
  Placement = pos=(0,0,7) rot=(0,0,1;0rad)
  sketch-geometry (4):
    g0: LineSegment StartX=-7.9 StartY=83 StartZ=0 EndX=0 EndY=68 EndZ=0
    g1: LineSegment StartX=0 StartY=98 StartZ=0 EndX=7.9 EndY=83 EndZ=0
    g2: LineSegment StartX=7.9 StartY=83 StartZ=0 EndX=0 EndY=68 EndZ=0
    g3: LineSegment StartX=-7.9 StartY=83 StartZ=0 EndX=0 EndY=98 EndZ=0
  constraints (10):
    c: PointOnObject(g1,g-2)
    c: Coincident(g1,g2)
    c: Coincident(g0,g2)
    c: Symmetric(g0,g1,g-2)
    c: DistanceY(g-1,g1) = 98
    c: DistanceX(g-1,g1) = 7.9
    c: Coincident(g3,g0)
    c: Coincident(g3,g1)
    c: DistanceY(g0,g1) = 30
    c: DistanceY(g1,g1) = 15
FEATURE [PartDesign::Pocket] Pocket031  label="Diamond Recess"
  BaseFeature = -> Pocket030
  Direction = (0,0,-1)
  Length = 5
  Length2 = 5
  Profile = -> Sketch066
  ReferenceAxis = -> Sketch066 [N_Axis]
  Refine = true
  Reversed = true
  Suppressed = false
  Type = 0
FEATURE [PartDesign::SubtractiveCylinder] Cylinder
  Angle = 360
  AttacherType = Attacher::AttachEngine3D
  AttachmentOffset = pos=(0,0,-85) rot=(0,0,1;0rad)
  AttachmentSupport = -> [XZ_Plane003]
  BaseFeature = -> Pocket003
  FirstAngle = 0
  Height = 28
  MapMode = 5
  Placement = pos=(0,85,-1.89e-14) rot=(1,0,0;1.5708rad)
  Radius = 4
  Refine = true
  SecondAngle = 0
  Suppressed = false
FEATURE [Sketcher::SketchObject] Sketch067
  ArcFitTolerance = 1e-06
  AttachmentOffset = pos=(0,0,7) rot=(0,0,1;0rad)
  AttachmentSupport = -> [XY_Plane003]
  FullyConstrained = false
  MakeInternals = false
  MapMode = 5
  Placement = pos=(0,0,7) rot=(0,0,1;0rad)
  sketch-geometry (4):
    g0: LineSegment StartX=-7.9 StartY=83 StartZ=0 EndX=-9e-16 EndY=68 EndZ=0
    g1: LineSegment StartX=0 StartY=98 StartZ=0 EndX=7.9 EndY=83 EndZ=0
    g2: LineSegment StartX=7.9 StartY=83 StartZ=0 EndX=-9e-16 EndY=68 EndZ=0
    g3: LineSegment StartX=-7.9 StartY=83 StartZ=0 EndX=0 EndY=98 EndZ=0
  constraints (10):
    c: PointOnObject(g1,g-2)
    c: Coincident(g1,g2)
    c: Coincident(g0,g2)
    c: Symmetric(g0,g1,g-2)
    c: DistanceY(g-1,g1) = 98
    c: DistanceX(g-1,g1) = 7.9
    c: Coincident(g3,g0)
    c: Coincident(g3,g1)
    c: DistanceY(g0,g1) = 30
    c: DistanceY(g1,g1) = 15
FEATURE [PartDesign::Pocket] Pocket032
  BaseFeature = -> Cylinder
  Direction = (0,0,-1)
  Length = 5
  Length2 = 5
  Placement = pos=(0,85,-1.89e-14) rot=(1,0,0;1.5708rad)
  Profile = -> Sketch067
  ReferenceAxis = -> Sketch067 [N_Axis]
  Refine = true
  Reversed = true
  Suppressed = false
  Type = 0
FEATURE [PartDesign::SubShapeBinder] Binder005
  BindCopyOnChange = 0
  BindMode = 0
  ClaimChildren = false
  Context = -> Part001 [Body011.Binder005.]
  Fuse = false
  MakeFace = true
  OffsetFill = false
  OffsetIntersection = false
  OffsetJoinType = 0
  OffsetOpenResult = false
  PartialLoad = false
  Refine = true
  Relative = true
  Support = -> [Part[Body.]]
  _Version = 2
FEATURE [Sketcher::SketchObject] Sketch068
  ArcFitTolerance = 1e-06
  AttachmentOffset = pos=(0,0,9) rot=(0,0,1;0rad)
  AttachmentSupport = -> [XY_Plane024]
  ExternalGeometry = -> [Binder005]
  FullyConstrained = true
  MakeInternals = false
  MapMode = 5
  Placement = pos=(0,0,9) rot=(0,0,1;0rad)
  constraints (2):
    c: DistanceY(g-3,g-4) = 53.11
    c: Distance(g-10,g-9) = 12.4428
FEATURE [Sketcher::SketchObject] Sketch069
  ArcFitTolerance = 1e-06
  AttachmentSupport = -> [XZ_Plane024]
  ExternalGeometry = -> [Binder005]
  FullyConstrained = true
  MakeInternals = false
  MapMode = 5
  Placement = pos=(0,0,0) rot=(1,0,0;1.5708rad)
  sketch-geometry (8):
    g0: LineSegment [constr] StartX=2.1e-15 StartY=17.5 StartZ=0 EndX=-15.1554 EndY=-8.75 EndZ=0
    g1: LineSegment [constr] StartX=-15.1554 StartY=-8.75 StartZ=0 EndX=-15.1554 EndY=28.9 EndZ=0
    g2: LineSegment [constr] StartX=-15.1554 StartY=28.9 StartZ=0 EndX=1.8e-15 EndY=28.9 EndZ=0
    g3: LineSegment [constr] StartX=2.1e-15 StartY=28.9 StartZ=0 EndX=2.1e-15 EndY=17.5 EndZ=0
    g4: LineSegment [constr] StartX=11.9 StartY=-12 StartZ=0 EndX=-2.47559e-07 EndY=16.9 EndZ=0
    g5: LineSegment [constr] StartX=-2.47559e-07 StartY=16.9 StartZ=0 EndX=-2.47559e-07 EndY=28.9 EndZ=0
    g6: LineSegment [constr] StartX=-2.47559e-07 StartY=28.9 StartZ=0 EndX=11.9 EndY=28.9 EndZ=0
    g7: LineSegment [constr] StartX=11.9 StartY=28.9 StartZ=0 EndX=11.9 EndY=-12 EndZ=0
  constraints (21):
    c: Coincident(g0,g1)
    c: Coincident(g1,g2)
    c: Coincident(g2,g3)
    c: Coincident(g3,g0)
    c: Horizontal(g2)
    c: Vertical(g1)
    c: Vertical(g3)
    c: Coincident(g0,g-5)
    c: Coincident(g4,g5)
    c: Coincident(g5,g6)
    c: Coincident(g6,g7)
    c: Coincident(g7,g4)
    c: Horizontal(g6)
    c: Vertical(g5)
    c: Vertical(g7)
    c: Coincident(g4,g-6)
    c: Coincident(g4,g-6)
    c: Coincident(g0,g-5)
    c: DistanceY(g5,g5) = 12
    c: Horizontal(g1,g6)
    c: DistanceY(g5,g-4) = -40.9
FEATURE [PartDesign::Body] Body011  label="Measurements"
  AllowCompound = true
  Group = -> [Binder005,Sketch068,Sketch069]
  Origin = -> Origin024
FEATURE [PartDesign::SubShapeBinder] Binder006
  BindCopyOnChange = 0
  BindMode = 0
  ClaimChildren = false
  Context = -> Part001 [Body012.Binder006.]
  Fuse = false
  MakeFace = true
  OffsetFill = false
  OffsetIntersection = false
  OffsetJoinType = 0
  OffsetOpenResult = false
  PartialLoad = false
  Refine = true
  Relative = true
  Support = -> [Part[Body002.]]
  _Version = 2
FEATURE [Sketcher::SketchObject] Sketch070
  ArcFitTolerance = 1e-06
  AttachmentSupport = -> [XY_Plane025]
  ExternalGeometry = -> [Binder006]
  FullyConstrained = false
  MakeInternals = false
  MapMode = 5
  sketch-geometry (10):
    g0: Circle [constr] CenterX=0 CenterY=110.615 CenterZ=0 NormalX=0 NormalY=0 NormalZ=1 AngleXU=0 Radius=11.7
    g1: LineSegment [constr] StartX=-6.20296 StartY=92.1148 StartZ=0 EndX=8.19492 EndY=92.1148 EndZ=0
    g2: LineSegment StartX=-14.9865 StartY=84.6148 StartZ=0 EndX=15.0135 EndY=84.6148 EndZ=0
    g3: LineSegment StartX=15.0135 StartY=84.6148 StartZ=0 EndX=15.0135 EndY=105.713 EndZ=0
    g4: LineSegment StartX=-14.9865 StartY=105.713 StartZ=0 EndX=-14.9865 EndY=84.6148 EndZ=0
    g5: Circle CenterX=11.3 CenterY=94.9 CenterZ=0 NormalX=0 NormalY=0 NormalZ=1 AngleXU=0 Radius=1.6
    g6: Circle CenterX=-11.1 CenterY=94.9 CenterZ=0 NormalX=0 NormalY=0 NormalZ=1 AngleXU=0 Radius=1.6
    g7: ArcOfCircle CenterX=0 CenterY=110.615 CenterZ=0 NormalX=0 NormalY=0 NormalZ=1 AngleXU=0 Radius=13.5445 StartAngle=0 EndAngle=3.14159
    g8: LineSegment StartX=13.5445 StartY=110.615 StartZ=0 EndX=15.0135 EndY=105.713 EndZ=0
    g9: LineSegment StartX=-13.5445 StartY=110.615 StartZ=0 EndX=-14.9865 EndY=105.713 EndZ=0
  constraints (25):
    c: PointOnObject(g0,g-2)
    c: Diameter(g0) = 23.4
    c: Horizontal(g1)
    c: DistanceY(g-8,g1) = 8
    c: Coincident(g2,g3)
    c: Coincident(g4,g2)
    c: Horizontal(g2)
    c: Vertical(g3)
    c: Vertical(g4)
    c: DistanceX(g2,g-8) = 0.5
    c: DistanceY(g-8,g2) = 0.5
    c: DistanceX(g-7,g2) = 0.5
    c: Coincident(g5,g-3)
    c: Coincident(g6,g-4)
    c: Diameter(g6) = 3.2
    c: Diameter(g5) = 3.2
    c: Coincident(g7,g0)
    c: Horizontal(g7,g0)
    c: Horizontal(g0,g7)
    c: Coincident(g8,g7)
    c: Coincident(g8,g3)
    c: Coincident(g9,g7)
    c: Coincident(g9,g4)
    c: DistanceY(g2,g0) = 26
    c: Horizontal(g4,g3)
FEATURE [PartDesign::SubShapeBinder] Binder007
  BindCopyOnChange = 0
  BindMode = 0
  ClaimChildren = false
  Context = -> Part001 [Body012.Binder007.]
  Fuse = false
  MakeFace = true
  OffsetFill = false
  OffsetIntersection = false
  OffsetJoinType = 0
  OffsetOpenResult = false
  PartialLoad = false
  Refine = true
  Relative = true
  Support = -> [Part[Body.Binder002.]]
  _Version = 2
FEATURE [PartDesign::Pad] Pad014
  Direction = (0,0,1)
  Length = 9
  Length2 = 10
  Profile = -> Sketch070
  ReferenceAxis = -> Sketch070 [N_Axis]
  Refine = true
  Reversed = true
  Suppressed = false
  Type = 0
FEATURE [Sketcher::SketchObject] Sketch071
  ArcFitTolerance = 1e-06
  AttachmentOffset = pos=(0,0,-1) rot=(0,0,1;0rad)
  AttachmentSupport = -> [XY_Plane025]
  ExternalGeometry = -> [Pad014]
  FullyConstrained = false
  MakeInternals = false
  MapMode = 5
  Placement = pos=(0,0,-1) rot=(0,0,1;0rad)
  sketch-geometry (27):
    g0: Circle [constr] CenterX=0 CenterY=110.615 CenterZ=0 NormalX=0 NormalY=0 NormalZ=1 AngleXU=0 Radius=11.7
    g1: Circle CenterX=0 CenterY=110.615 CenterZ=0 NormalX=0 NormalY=0 NormalZ=1 AngleXU=0 Radius=1.5
    g2: Circle CenterX=0 CenterY=114.115 CenterZ=0 NormalX=0 NormalY=0 NormalZ=1 AngleXU=0 Radius=1.5
    g3: Circle CenterX=0 CenterY=117.615 CenterZ=0 NormalX=0 NormalY=0 NormalZ=1 AngleXU=0 Radius=1.5
    g4: Circle CenterX=0 CenterY=121.115 CenterZ=0 NormalX=0 NormalY=0 NormalZ=1 AngleXU=0 Radius=1.5
    g5: LineSegment [constr] StartX=-17.1977 StartY=110.615 StartZ=0 EndX=29.8628 EndY=110.615 EndZ=0
    g6: Circle CenterX=0 CenterY=107.115 CenterZ=0 NormalX=0 NormalY=0 NormalZ=1 AngleXU=0 Radius=1.5
    g7: Circle CenterX=0 CenterY=103.615 CenterZ=0 NormalX=0 NormalY=0 NormalZ=1 AngleXU=0 Radius=1.5
    g8: Circle CenterX=0 CenterY=100.115 CenterZ=0 NormalX=0 NormalY=0 NormalZ=1 AngleXU=0 Radius=1.5
    g9: Circle CenterX=3.5 CenterY=110.615 CenterZ=0 NormalX=0 NormalY=0 NormalZ=1 AngleXU=0 Radius=1.5
    g10: Circle CenterX=7 CenterY=110.615 CenterZ=0 NormalX=0 NormalY=0 NormalZ=1 AngleXU=0 Radius=1.5
    g11: Circle CenterX=10.5 CenterY=110.615 CenterZ=0 NormalX=0 NormalY=0 NormalZ=1 AngleXU=0 Radius=1.5
    g12: Circle CenterX=-3.5 CenterY=110.615 CenterZ=0 NormalX=0 NormalY=0 NormalZ=1 AngleXU=0 Radius=1.5
    g13: Circle CenterX=-7 CenterY=110.615 CenterZ=0 NormalX=0 NormalY=0 NormalZ=1 AngleXU=0 Radius=1.5
    g14: Circle CenterX=-10.5 CenterY=110.615 CenterZ=0 NormalX=0 NormalY=0 NormalZ=1 AngleXU=0 Radius=1.5
    g15: Circle CenterX=3.5 CenterY=114.115 CenterZ=0 NormalX=0 NormalY=0 NormalZ=1 AngleXU=0 Radius=1.5
    g16: Circle CenterX=7 CenterY=114.115 CenterZ=0 NormalX=0 NormalY=0 NormalZ=1 AngleXU=0 Radius=1.5
    g17: Circle CenterX=-3.5 CenterY=114.115 CenterZ=0 NormalX=0 NormalY=0 NormalZ=1 AngleXU=0 Radius=1.5
    g18: Circle CenterX=-7 CenterY=114.115 CenterZ=0 NormalX=0 NormalY=0 NormalZ=1 AngleXU=0 Radius=1.5
    g19: Circle CenterX=3.5 CenterY=117.615 CenterZ=0 NormalX=0 NormalY=0 NormalZ=1 AngleXU=0 Radius=1.5
    g20: Circle CenterX=-3.5 CenterY=117.615 CenterZ=0 NormalX=0 NormalY=0 NormalZ=1 AngleXU=0 Radius=1.5
    g21: Circle CenterX=-3.5 CenterY=103.615 CenterZ=0 NormalX=0 NormalY=0 NormalZ=1 AngleXU=0 Radius=1.5
    g22: Circle CenterX=-3.5 CenterY=107.115 CenterZ=0 NormalX=0 NormalY=0 NormalZ=1 AngleXU=0 Radius=1.5
    g23: Circle CenterX=-7 CenterY=107.115 CenterZ=0 NormalX=0 NormalY=0 NormalZ=1 AngleXU=0 Radius=1.5
    g24: Circle CenterX=3.5 CenterY=103.615 CenterZ=0 NormalX=0 NormalY=0 NormalZ=1 AngleXU=0 Radius=1.5
    g25: Circle CenterX=3.5 CenterY=107.115 CenterZ=0 NormalX=0 NormalY=0 NormalZ=1 AngleXU=0 Radius=1.5
    g26: Circle CenterX=7 CenterY=107.115 CenterZ=0 NormalX=0 NormalY=0 NormalZ=1 AngleXU=0 Radius=1.5
  constraints (55):
    c: PointOnObject(g0,g-2)
    c: DistanceY(g-3,g0) = 26
    c: Diameter(g0) = 23.4
    c: Coincident(g1,g0)
    c: Diameter(g1) = 3
    c: Diameter(g2) = 3
    c: Diameter(g3) = 3
    c: Diameter(g4) = 3
    c: Horizontal(g5)
    c: PointOnObject(g0,g5)
    c: Diameter(g6) = 3
    c: Diameter(g7) = 3
    c: Diameter(g8) = 3
    c: Diameter(g9) = 3
    c: Diameter(g10) = 3
    c: Diameter(g11) = 3
    c: Diameter(g12) = 3
    c: Diameter(g13) = 3
    c: Diameter(g14) = 3
    c: Diameter(g15) = 3
    c: Diameter(g16) = 3
    c: Diameter(g17) = 3
    c: Diameter(g18) = 3
    c: Diameter(g19) = 3
    c: Diameter(g20) = 3
    c: Diameter(g25) = 3
    c: Diameter(g26) = 3
    c: Diameter(g22) = 3
    c: Diameter(g23) = 3
    c: Diameter(g24) = 3
    c: Diameter(g21) = 3
    c: Horizontal(g14,g13)
    c: Horizontal(g12,g0)
    c: Horizontal(g12,g13)
    c: Horizontal(g9,g10)
    c: Horizontal(g11,g9)
    c: Horizontal(g0,g9)
    c: DistanceY(g0,g2) = 3.5
    c: DistanceY(g2,g3) = 3.5
    c: DistanceY(g3,g4) = 3.5
    c: Horizontal(g20,g3)
    c: Horizontal(g3,g19)
    c: Horizontal(g17,g2)
    c: Horizontal(g17,g18)
    c: Horizontal(g2,g15)
    c: Horizontal(g15,g16)
    c: Horizontal(g6,g22)
    c: Horizontal(g22,g23)
    c: Horizontal(g23,g25)
    c: Horizontal(g25,g26)
    c: DistanceY(g6,g0) = 3.5
    c: Horizontal(g7,g21)
    c: Horizontal(g21,g24)
    c: DistanceY(g7,g6) = 3.5
    c: DistanceY(g8,g7) = 3.5
FEATURE [PartDesign::Pocket] Pocket033  label="Grill"
  BaseFeature = -> Pad014
  Direction = (0,0,-1)
  Length = 8
  Length2 = 5
  Profile = -> Sketch071
  ReferenceAxis = -> Sketch071 [N_Axis]
  Refine = true
  Suppressed = false
  Type = 0
FEATURE [Sketcher::SketchObject] Sketch072
  ArcFitTolerance = 1e-06
  AttachmentOffset = pos=(0,0,-8) rot=(0,0,1;0rad)
  AttachmentSupport = -> [XY_Plane025]
  ExternalGeometry = -> [Pocket033]
  FullyConstrained = false
  MakeInternals = false
  MapMode = 5
  Placement = pos=(0,0,-8) rot=(0,0,1;0rad)
  sketch-geometry (17):
    g0: ArcOfCircle CenterX=-11.1 CenterY=94.9 CenterZ=0 NormalX=0 NormalY=0 NormalZ=1 AngleXU=0 Radius=3.98661 StartAngle=4.07061 EndAngle=6.28876
    g1: ArcOfCircle CenterX=0 CenterY=110.615 CenterZ=0 NormalX=0 NormalY=0 NormalZ=1 AngleXU=0 Radius=11.6 StartAngle=0.00267159 EndAngle=3.12513
    g2: LineSegment StartX=-11.5984 StartY=110.806 StartZ=0 EndX=-13.4865 EndY=104.388 EndZ=0
    g3: LineSegment StartX=-13.4865 StartY=104.388 StartZ=0 EndX=-13.4865 EndY=98.0934 EndZ=0
    g4: LineSegment StartX=-13.4865 StartY=91.7066 StartZ=0 EndX=-13.4865 EndY=86.1879 EndZ=0
    g5: LineSegment StartX=-13.4865 StartY=86.1879 StartZ=0 EndX=0 EndY=86.1879 EndZ=0
    g6: LineSegment StartX=13.5135 StartY=86.1879 StartZ=0 EndX=0 EndY=86.1879 EndZ=0
    g7: LineSegment StartX=13.5135 StartY=96.8782 StartZ=0 EndX=13.5135 EndY=86.1879 EndZ=0
    g8: LineSegment StartX=13.5135 StartY=104.261 StartZ=0 EndX=13.5135 EndY=96.8782 EndZ=0
    g9: LineSegment StartX=11.6 StartY=110.646 StartZ=0 EndX=13.5135 EndY=104.261 EndZ=0
    g10: ArcOfCircle CenterX=0 CenterY=110.615 CenterZ=0 NormalX=0 NormalY=0 NormalZ=1 AngleXU=0 Radius=11.45 StartAngle=3.99799 EndAngle=4.46064
    g11: LineSegment StartX=-7.50162 StartY=101.964 StartZ=0 EndX=-8.94209 EndY=100.501 EndZ=0
    g12: LineSegment StartX=-2.85221 StartY=99.5257 StartZ=0 EndX=-3.13722 EndY=97.4756 EndZ=0
    g13: LineSegment StartX=-8.94209 StartY=100.501 StartZ=0 EndX=-10.7101 EndY=98.8675 EndZ=0
    g14: ArcOfCircle CenterX=0 CenterY=110.615 CenterZ=0 NormalX=0 NormalY=0 NormalZ=1 AngleXU=0 Radius=13.5085 StartAngle=4.22558 EndAngle=4.47801
    g15: ArcOfCircle CenterX=-11.1 CenterY=94.9 CenterZ=0 NormalX=0 NormalY=0 NormalZ=1 AngleXU=0 Radius=3.98661 StartAngle=1.47284 EndAngle=2.21258
    g16: LineSegment StartX=-6.31942 StartY=98.6756 StartZ=0 EndX=-7.11345 EndY=94.9222 EndZ=0
  constraints (36):
    c: Coincident(g0,g-7)
    c: Diameter(g1) = 23.2
    c: Coincident(g3,g2)
    c: Vertical(g3)
    c: Vertical(g4)
    c: Coincident(g5,g4)
    c: PointOnObject(g5,g-2)
    c: Horizontal(g5)
    c: Vertical(g3,g4)
    c: Parallel(g-8,g2)
    c: Coincident(g0,g4)
    c: Coincident(g8,g9)
    c: Vertical(g8)
    c: Vertical(g7)
    c: Coincident(g6,g7)
    c: Horizontal(g6)
    c: Coincident(g1,g2)
    c: Coincident(g1,g9)
    c: Coincident(g10,g1)
    c: Radius(g10) = 11.45
    c: Coincident(g11,g10)
    c: Coincident(g12,g10)
    c: Coincident(g12,g14)
    c: PointOnObject(g13,g0)
    c: Coincident(g15,g0)
    c: Coincident(g15,g13)
    c: Coincident(g15,g3)
    c: Coincident(g8,g7)
    c: DistanceX(g6,g-5) = 1.5
    c: Coincident(g11,g13)
    c: Coincident(g16,g14)
    c: Coincident(g16,g0)
    c: Coincident(g1,g14)
    c: Coincident(g1,g-3)
    c: Parallel(g9,g-9)
    c: DistanceX(g-4,g4) = 1.5
FEATURE [PartDesign::Pocket] Pocket034  label="Shell"
  BaseFeature = -> Pocket033
  Direction = (0,0,-1)
  Length = 9
  Length2 = 5
  Profile = -> Sketch072
  ReferenceAxis = -> Sketch072 [N_Axis]
  Refine = true
  Reversed = true
  Suppressed = false
  Type = 0
FEATURE [Sketcher::SketchObject] Sketch073
  ArcFitTolerance = 1e-06
  AttachmentOffset = pos=(0,0,-8) rot=(0,0,1;0rad)
  AttachmentSupport = -> [XY_Plane025]
  ExternalGeometry = -> [Pocket034]
  FullyConstrained = false
  MakeInternals = false
  MapMode = 5
  Placement = pos=(0,0,-8) rot=(0,0,1;0rad)
  sketch-geometry (8):
    g0: Circle CenterX=5.9379 CenterY=89.5305 CenterZ=0 NormalX=0 NormalY=0 NormalZ=1 AngleXU=0 Radius=2
    g1: LineSegment StartX=-4.18284 StartY=90.1587 StartZ=0 EndX=9.80995 EndY=98.9024 EndZ=0
    g2: LineSegment StartX=9.80995 StartY=98.9024 StartZ=0 EndX=9.01507 EndY=100.174 EndZ=0
    g3: LineSegment StartX=9.01507 StartY=100.174 StartZ=0 EndX=-4.97772 EndY=91.4308 EndZ=0
    g4: LineSegment StartX=-4.97772 StartY=91.4308 StartZ=0 EndX=-4.18284 EndY=90.1587 EndZ=0
    g5: GeomPoint X=2.81355 Y=94.5305 Z=0
    g6: LineSegment [constr] StartX=-5.08092 StartY=107.164 StartZ=0 EndX=5.9379 EndY=89.5305 EndZ=0
    g7: Circle [constr] CenterX=0 CenterY=110.615 CenterZ=0 NormalX=0 NormalY=0 NormalZ=1 AngleXU=0 Radius=11.5
  constraints (18):
    c: Diameter(g0) = 4
    c: Coincident(g1,g2)
    c: Coincident(g2,g3)
    c: Coincident(g3,g4)
    c: Coincident(g4,g1)
    c: Symmetric(g1,g1,g5)
    c: DistanceY(g0,g5) = 5
    c: Angle(g2,g1) = 1.5708
    c: Angle(g4,g3) = 1.5708
    c: Distance(g2,g2) = 1.5
    c: Distance(g4,g4) = 1.5
    c: Distance(g3,g3) = 16.5
    c: Symmetric(g3,g2,g6)
    c: Coincident(g6,g0)
    c: Angle(g-2,g6) = 0.558505
    c: PointOnObject(g7,g-2)
    c: Diameter(g7) = 23
    c: DistanceY(g-3,g7) = 26
FEATURE [PartDesign::Pocket] Pocket035  label="Belt Thing"
  BaseFeature = -> Pocket034
  Direction = (0,0,-1)
  Length = 7
  Length2 = 5
  Profile = -> Sketch073
  ReferenceAxis = -> Sketch073 [N_Axis]
  Refine = true
  Suppressed = false
  Type = 0
FEATURE [Sketcher::SketchObject] Sketch074
  ArcFitTolerance = 1e-06
  AttachmentOffset = pos=(0,0,-4) rot=(0,0,1;0rad)
  AttachmentSupport = -> [XY_Plane025]
  ExternalGeometry = -> [Pocket035]
  FullyConstrained = false
  MakeInternals = false
  MapMode = 5
  Placement = pos=(0,0,-4) rot=(0,0,1;0rad)
  expr: Constraints[2] = 23.4 / 2
  sketch-geometry (20):
    g0: ArcOfCircle CenterX=5.9379 CenterY=89.5305 CenterZ=0 NormalX=0 NormalY=0 NormalZ=1 AngleXU=0 Radius=4.0468 StartAngle=3.11593 EndAngle=7.32904
    g1: ArcOfCircle CenterX=0 CenterY=110.615 CenterZ=0 NormalX=0 NormalY=0 NormalZ=1 AngleXU=0 Radius=11.7 StartAngle=4.9882 EndAngle=5.65831
    g2: LineSegment StartX=-6.21474 StartY=91.7837 StartZ=0 EndX=-4.32332 EndY=88.4366 EndZ=0
    g3: LineSegment StartX=-4.32332 StartY=88.4366 StartZ=0 EndX=0.140351 EndY=90.7342 EndZ=0
    g4: LineSegment StartX=7.6958 StartY=94.8139 StartZ=0 EndX=11.7649 EndY=99.2277 EndZ=0
    g5: LineSegment StartX=10.1003 StartY=102.55 StartZ=0 EndX=9.48914 EndY=103.77 EndZ=0
    g6: ArcOfCircle CenterX=3.77843 CenterY=97.2647 CenterZ=0 NormalX=0 NormalY=0 NormalZ=1 AngleXU=0 Radius=2.17447 StartAngle=1.84661 EndAngle=2.79373
    g7: LineSegment StartX=10.1003 StartY=102.55 StartZ=0 EndX=12.991 EndY=106.004 EndZ=0
    g8: LineSegment StartX=11.7649 StartY=99.2277 StartZ=0 EndX=13.5135 EndY=98.9006 EndZ=0
    g9: LineSegment StartX=13.5135 StartY=98.9006 StartZ=0 EndX=13.5135 EndY=104.261 EndZ=0
    g10: LineSegment StartX=13.5135 StartY=104.261 StartZ=0 EndX=12.991 EndY=106.004 EndZ=0
    g11: LineSegment StartX=1.73421 StartY=98.006 StartZ=0 EndX=1.16518 EndY=96.4367 EndZ=0
    g12: LineSegment StartX=1.16518 StartY=96.4367 StartZ=0 EndX=-6.21474 EndY=91.7837 EndZ=0
    g13: ArcOfCircle CenterX=0.690568 CenterY=89.6652 CenterZ=0 NormalX=0 NormalY=0 NormalZ=1 AngleXU=0 Radius=1.20226 StartAngle=6.25752 EndAngle=8.32934
    g14: ArcOfCircle CenterX=8.54458 CenterY=94.0314 CenterZ=0 NormalX=0 NormalY=0 NormalZ=1 AngleXU=0 Radius=1.15444 StartAngle=2.3968 EndAngle=4.18745
    g15: Circle CenterX=5.9379 CenterY=89.5305 CenterZ=0 NormalX=0 NormalY=0 NormalZ=1 AngleXU=0 Radius=2
    g16: LineSegment StartX=-4.97772 StartY=91.4308 StartZ=0 EndX=9.01507 EndY=100.174 EndZ=0
    g17: LineSegment StartX=9.01507 StartY=100.174 StartZ=0 EndX=9.80995 EndY=98.9024 EndZ=0
    g18: LineSegment StartX=9.80995 StartY=98.9024 StartZ=0 EndX=-4.18284 EndY=90.1587 EndZ=0
    g19: LineSegment StartX=-4.18284 StartY=90.1587 StartZ=0 EndX=-4.97772 EndY=91.4308 EndZ=0
  constraints (30):
    c: Coincident(g0,g-6)
    c: Coincident(g1,g-3)
    c: Radius(g1) = 11.7
    c: Coincident(g2,g3)
    c: Coincident(g5,g1)
    c: Tangent(g1,g6) = 1.5708
    c: PointOnObject(g7,g-8)
    c: Coincident(g8,g4)
    c: PointOnObject(g8,g-7)
    c: Coincident(g5,g7)
    c: Coincident(g8,g9)
    c: Coincident(g9,g-8)
    c: Coincident(g9,g10)
    c: Coincident(g10,g7)
    c: Tangent(g6,g11) = -1.5708
    c: Coincident(g11,g12)
    c: Coincident(g2,g12)
    c: Tangent(g3,g13) = 1.5708
    c: Tangent(g0,g13) = 1.5708
    c: Tangent(g4,g14) = 1.5708
    c: Tangent(g0,g14) = 1.5708
    c: Coincident(g15,g0)
    c: Coincident(g-4,g16)
    c: Coincident(g16,g-4)
    c: Coincident(g16,g17)
    c: Coincident(g17,g-5)
    c: Coincident(g17,g18)
    c: Coincident(g18,g-5)
    c: Coincident(g18,g19)
    c: Coincident(g19,g16)
FEATURE [PartDesign::Pad] Pad015  label="Belt Thing Support"
  BaseFeature = -> Pocket035
  Direction = (0,0,1)
  Length = 5
  Length2 = 10
  Profile = -> Sketch074
  ReferenceAxis = -> Sketch074 [N_Axis]
  Refine = true
  Reversed = true
  Suppressed = false
  Type = 0
FEATURE [Sketcher::SketchObject] Sketch076
  ArcFitTolerance = 1e-06
  AttachmentSupport = -> [XY_Plane025]
  FullyConstrained = false
  MakeInternals = false
  MapMode = 5
  sketch-geometry (2):
    g0: Circle CenterX=11.3 CenterY=94.9 CenterZ=0 NormalX=0 NormalY=0 NormalZ=1 AngleXU=0 Radius=1.6
    g1: Circle CenterX=11.3 CenterY=94.9 CenterZ=0 NormalX=0 NormalY=0 NormalZ=1 AngleXU=0 Radius=4.21017
  constraints (3):
    c: Coincident(g0,g-3)
    c: Diameter(g0) = 3.2
    c: Coincident(g1,g0)
FEATURE [PartDesign::Pad] Pad016
  BaseFeature = -> Pad015
  Direction = (0,0,1)
  Length = 9
  Length2 = 10
  Profile = -> Sketch076
  ReferenceAxis = -> Sketch076 [N_Axis]
  Refine = true
  Reversed = true
  Suppressed = false
  Type = 0
FEATURE [Sketcher::SketchObject] Sketch077
  ArcFitTolerance = 1e-06
  AttachmentOffset = pos=(0,0,-9) rot=(0,0,1;0rad)
  AttachmentSupport = -> [XY_Plane025]
  FullyConstrained = false
  MakeInternals = false
  MapMode = 5
  Placement = pos=(0,0,-9) rot=(0,0,1;0rad)
  sketch-geometry (2):
    g0: Circle CenterX=-11.1 CenterY=94.9 CenterZ=0 NormalX=0 NormalY=0 NormalZ=1 AngleXU=0 Radius=3
    g1: Circle CenterX=11.3 CenterY=94.9 CenterZ=0 NormalX=0 NormalY=0 NormalZ=1 AngleXU=0 Radius=3
  constraints (2):
    c: Diameter(g1) = 6
    c: Diameter(g0) = 6
FEATURE [PartDesign::Pocket] Pocket036
  BaseFeature = -> Pad016
  Direction = (0,0,-1)
  Length = 5
  Length2 = 5
  Profile = -> Sketch077
  ReferenceAxis = -> Sketch077 [N_Axis]
  Refine = true
  Reversed = true
  Suppressed = false
  Type = 0
FEATURE [PartDesign::SubShapeBinder] Binder008
  BindCopyOnChange = 0
  BindMode = 0
  ClaimChildren = false
  Context = -> Part001 [Body013.Binder008.]
  Fuse = false
  MakeFace = true
  OffsetFill = false
  OffsetIntersection = false
  OffsetJoinType = 0
  OffsetOpenResult = false
  PartialLoad = false
  Refine = true
  Relative = true
  Support = -> [Part[Body002.]]
  _Version = 2
FEATURE [PartDesign::SubShapeBinder] Binder009
  BindCopyOnChange = 0
  BindMode = 0
  ClaimChildren = false
  Context = -> Part001 [Body013.Binder009.]
  Fuse = false
  MakeFace = true
  OffsetFill = false
  OffsetIntersection = false
  OffsetJoinType = 0
  OffsetOpenResult = false
  PartialLoad = false
  Refine = true
  Relative = true
  Support = -> [Part[Body.Binder002.]]
  _Version = 2
FEATURE [Sketcher::SketchObject] Sketch078
  ArcFitTolerance = 1e-06
  AttachmentOffset = pos=(0,0,5) rot=(0,0,1;0rad)
  AttachmentSupport = -> [XY_Plane026]
  ExternalGeometry = -> [Binder008,Binder009]
  FullyConstrained = false
  MakeInternals = false
  MapMode = 5
  Placement = pos=(0,0,5) rot=(0,0,1;0rad)
  sketch-geometry (33):
    g0: LineSegment StartX=-6.75434 StartY=92.5893 StartZ=0 EndX=-6.75434 EndY=104.622 EndZ=0
    g1: LineSegment StartX=-6.75434 StartY=104.622 StartZ=0 EndX=-18.1847 EndY=104.622 EndZ=0
    g2: LineSegment StartX=-18.1847 StartY=104.622 StartZ=0 EndX=-20.277 EndY=118.371 EndZ=0
    g3: LineSegment StartX=-26.2802 StartY=127.867 StartZ=0 EndX=-27.275 EndY=128.54 EndZ=0
    g4: LineSegment StartX=-31.7466 StartY=136.96 StartZ=0 EndX=-31.7466 EndY=147.924 EndZ=0
    g5: LineSegment StartX=-28.8438 StartY=158.137 StartZ=0 EndX=-21.397 EndY=170.179 EndZ=0
    g6: LineSegment StartX=-19.0881 StartY=171.466 StartZ=0 EndX=0 EndY=171.466 EndZ=0
    g7: LineSegment StartX=-6.75434 StartY=92.5893 StartZ=0 EndX=0 EndY=92.5893 EndZ=0
    g8: ArcOfCircle CenterX=-34.1235 CenterY=116.264 CenterZ=0 NormalX=0 NormalY=0 NormalZ=1 AngleXU=0 Radius=14.0059 StartAngle=0.151022 EndAngle=0.976409
    g9: GeomPoint [constr] X=-21.1996 Y=124.433 Z=0
    g10: ArcOfCircle CenterX=-21.5837 CenterY=136.96 CenterZ=0 NormalX=0 NormalY=0 NormalZ=1 AngleXU=0 Radius=10.163 StartAngle=3.14159 EndAngle=4.118
    g11: GeomPoint [constr] X=-31.7467 Y=131.562 Z=0
    g12: ArcOfCircle CenterX=-12.3284 CenterY=147.924 CenterZ=0 NormalX=0 NormalY=0 NormalZ=1 AngleXU=0 Radius=19.4182 StartAngle=2.58775 EndAngle=3.14159
    g13: GeomPoint [constr] X=-31.7466 Y=153.443 Z=0
    g14: ArcOfCircle CenterX=-19.0881 CenterY=168.751 CenterZ=0 NormalX=0 NormalY=0 NormalZ=1 AngleXU=0 Radius=2.71472 StartAngle=1.5708 EndAngle=2.58775
    g15: GeomPoint [constr] X=-20.6012 Y=171.466 Z=0
    g16: LineSegment StartX=6.75434 StartY=92.5893 StartZ=0 EndX=6.75434 EndY=104.622 EndZ=0
    g17: LineSegment StartX=6.75434 StartY=104.622 StartZ=0 EndX=18.1847 EndY=104.622 EndZ=0
    g18: LineSegment StartX=18.1847 StartY=104.622 StartZ=0 EndX=20.277 EndY=118.371 EndZ=0
    g19: LineSegment StartX=26.2802 StartY=127.867 StartZ=0 EndX=27.275 EndY=128.54 EndZ=0
    g20: LineSegment StartX=31.7466 StartY=136.96 StartZ=0 EndX=31.7466 EndY=147.924 EndZ=0
    g21: LineSegment StartX=28.8438 StartY=158.137 StartZ=0 EndX=21.397 EndY=170.179 EndZ=0
    g22: LineSegment StartX=19.0881 StartY=171.466 StartZ=0 EndX=0 EndY=171.466 EndZ=0
    g23: LineSegment StartX=6.75434 StartY=92.5893 StartZ=0 EndX=0 EndY=92.5893 EndZ=0
    g24: ArcOfCircle CenterX=34.1235 CenterY=116.264 CenterZ=0 NormalX=0 NormalY=0 NormalZ=1 AngleXU=0 Radius=14.0059 StartAngle=2.16518 EndAngle=2.99057
    g25: GeomPoint [constr] X=21.1996 Y=124.433 Z=0
    g26: ArcOfCircle CenterX=21.5837 CenterY=136.96 CenterZ=0 NormalX=0 NormalY=0 NormalZ=1 AngleXU=0 Radius=10.163 StartAngle=5.30678 EndAngle=6.28319
    g27: GeomPoint [constr] X=31.7467 Y=131.562 Z=0
    g28: ArcOfCircle CenterX=12.3284 CenterY=147.924 CenterZ=0 NormalX=0 NormalY=0 NormalZ=1 AngleXU=0 Radius=19.4182 StartAngle=1.9e-06 EndAngle=0.553843
    g29: GeomPoint [constr] X=31.7466 Y=153.443 Z=0
    g30: ArcOfCircle CenterX=19.0881 CenterY=168.751 CenterZ=0 NormalX=0 NormalY=0 NormalZ=1 AngleXU=0 Radius=2.71472 StartAngle=0.553843 EndAngle=1.5708
    g31: GeomPoint [constr] X=20.6012 Y=171.466 Z=0
    g32: Circle CenterX=0 CenterY=164 CenterZ=0 NormalX=0 NormalY=0 NormalZ=1 AngleXU=0 Radius=2
  constraints (54):
    c: Vertical(g0)
    c: Coincident(g0,g1)
    c: Horizontal(g1)
    c: Coincident(g1,g2)
    c: PointOnObject(g6,g-2)
    c: Horizontal(g6)
    c: Coincident(g0,g7)
    c: PointOnObject(g7,g-2)
    c: Horizontal(g7)
    c: DistanceY(g-3,g0) = 0.4
    c: DistanceX(g-3,g0) = 0.4
    c: DistanceY(g-3,g0) = 1.4
    c: PointOnObject(g9,g2)
    c: PointOnObject(g9,g3)
    c: Tangent(g2,g8) = -1.5708
    c: Tangent(g3,g8) = -1.5708
    c: PointOnObject(g11,g3)
    c: PointOnObject(g11,g4)
    c: Tangent(g3,g10) = 1.5708
    c: Tangent(g4,g10) = 1.5708
    c: PointOnObject(g13,g4)
    c: PointOnObject(g13,g5)
    c: Tangent(g4,g12) = 1.5708
    c: Tangent(g5,g12) = 1.5708
    c: PointOnObject(g15,g5)
    c: PointOnObject(g15,g6)
    c: Tangent(g5,g14) = 1.5708
    c: Tangent(g6,g14) = 1.5708
    c: Parallel(g4,g-7)
    c: Vertical(g16)
    c: Coincident(g16,g17)
    c: Horizontal(g17)
    c: Coincident(g17,g18)
    c: Horizontal(g22)
    c: Coincident(g16,g23)
    c: Horizontal(g23)
    c: PointOnObject(g25,g18)
    c: PointOnObject(g25,g19)
    c: Tangent(g18,g24) = 1.5708
    c: Tangent(g19,g24) = 1.5708
    c: PointOnObject(g27,g19)
    c: PointOnObject(g27,g20)
    c: Tangent(g19,g26) = -1.5708
    c: Tangent(g20,g26) = -1.5708
    c: PointOnObject(g29,g20)
    c: PointOnObject(g29,g21)
    c: Tangent(g20,g28) = -1.5708
    c: Tangent(g21,g28) = -1.5708
    c: PointOnObject(g31,g21)
    c: PointOnObject(g31,g22)
    c: Tangent(g21,g30) = -1.5708
    c: Tangent(g22,g30) = -1.5708
    c: Coincident(g32,g-5)
    c: Diameter(g32) = 4
FEATURE [PartDesign::Body] Body013  label="Top Acrylic"
  AllowCompound = true
  Group = -> [Binder008,Binder009,Sketch078]
  Origin = -> Origin026
FEATURE [PartDesign::SubShapeBinder] Binder010
  BindCopyOnChange = 0
  BindMode = 0
  ClaimChildren = false
  Context = -> Part001 [Body014.Binder010.]
  Fuse = false
  MakeFace = true
  OffsetFill = false
  OffsetIntersection = false
  OffsetJoinType = 0
  OffsetOpenResult = false
  PartialLoad = false
  Refine = true
  Relative = true
  Support = -> [Part[Body.]]
  _Version = 2
FEATURE [Sketcher::SketchObject] Sketch079
  ArcFitTolerance = 1e-06
  AttachmentOffset = pos=(0,0,48) rot=(0,0,1;0rad)
  AttachmentSupport = -> [XZ_Plane027]
  FullyConstrained = false
  MakeInternals = false
  MapMode = 5
  Placement = pos=(0,-48,1.07e-14) rot=(1,0,0;1.5708rad)
  sketch-geometry (9):
    g0: Circle [constr] CenterX=0 CenterY=0 CenterZ=0 NormalX=0 NormalY=0 NormalZ=1 AngleXU=0 Radius=17.5
    g1: Circle [constr] CenterX=7.3 CenterY=0 CenterZ=0 NormalX=0 NormalY=0 NormalZ=1 AngleXU=0 Radius=7.25
    g2: Circle [constr] CenterX=-7.3 CenterY=0 CenterZ=0 NormalX=0 NormalY=0 NormalZ=1 AngleXU=0 Radius=7.25
    g3: LineSegment StartX=-10 StartY=8.64218 StartZ=0 EndX=10 EndY=8.64218 EndZ=0
    g4: ArcOfCircle CenterX=-7.3 CenterY=0 CenterZ=0 NormalX=0 NormalY=0 NormalZ=1 AngleXU=0 Radius=7.3 StartAngle=0.594038 EndAngle=1.74288
    g5: ArcOfCircle CenterX=7.3 CenterY=0 CenterZ=0 NormalX=0 NormalY=0 NormalZ=1 AngleXU=0 Radius=7.3 StartAngle=1.39872 EndAngle=2.54755
    g6: LineSegment StartX=10 StartY=8.64218 StartZ=0 EndX=8.55 EndY=7.19218 EndZ=0
    g7: LineSegment StartX=-10 StartY=8.64218 StartZ=0 EndX=-8.55 EndY=7.19218 EndZ=0
    g8: ArcOfCircle CenterX=1e-16 CenterY=4.93057 CenterZ=0 NormalX=0 NormalY=0 NormalZ=1 AngleXU=0 Radius=1.50911 StartAngle=3.73563 EndAngle=5.68915
  constraints (22):
    c: Coincident(g0,g-1)
    c: Diameter(g0) = 35
    c: PointOnObject(g1,g-1)
    c: Diameter(g1) = 14.5
    c: Diameter(g2) = 14.5
    c: DistanceX(g2,g0) = 7.3
    c: Symmetric(g2,g1,g-2)
    c: Coincident(g4,g2)
    c: Coincident(g5,g1)
    c: DistanceY(g5,g3) = 1.45
    c: Coincident(g6,g3)
    c: Coincident(g6,g5)
    c: Coincident(g7,g3)
    c: Coincident(g7,g4)
    c: Radius(g5) = 7.3
    c: Angle(g3,g6) = 0.785398
    c: Angle(g7,g3) = 0.785398
    c: Symmetric(g3,g3,g-2)
    c: DistanceX(g3,g-1) = 10
    c: Tangent(g4,g8) = 1.5708
    c: Tangent(g5,g8) = 1.5708
    c: Radius(g4) = 7.3
FEATURE [PartDesign::Pad] Pad017
  Direction = (0,-1,2e-16)
  Length = 103
  Length2 = 10
  Placement = pos=(0,0,0) rot=(1,0,0;1.5708rad)
  Profile = -> Sketch079
  ReferenceAxis = -> Sketch079 [N_Axis]
  Refine = true
  Reversed = true
  Suppressed = false
  Type = 0
FEATURE [Sketcher::SketchObject] Sketch080
  ArcFitTolerance = 1e-06
  AttachmentOffset = pos=(0,0,59) rot=(0,0,1;0rad)
  AttachmentSupport = -> [XZ_Plane027]
  FullyConstrained = false
  MakeInternals = false
  MapMode = 5
  Placement = pos=(0,-59,1.31e-14) rot=(1,0,0;1.5708rad)
  sketch-geometry (4):
    g0: LineSegment StartX=-2.44114 StartY=8.64 StartZ=0 EndX=-2.44114 EndY=6.74 EndZ=0
    g1: LineSegment StartX=-2.44114 StartY=6.74 StartZ=0 EndX=2.44114 EndY=6.74 EndZ=0
    g2: LineSegment StartX=2.44114 StartY=6.74 StartZ=0 EndX=2.44114 EndY=8.64 EndZ=0
    g3: LineSegment StartX=2.44114 StartY=8.64 StartZ=0 EndX=-2.44114 EndY=8.64 EndZ=0
  constraints (10):
    c: Coincident(g0,g1)
    c: Coincident(g1,g2)
    c: Coincident(g2,g3)
    c: Coincident(g3,g0)
    c: Vertical(g0)
    c: Vertical(g2)
    c: Horizontal(g1)
    c: Symmetric(g0,g2,g-2)
    c: DistanceY(g2,g2) = 1.9
    c: DistanceY(g-1,g1) = 6.74
FEATURE [PartDesign::Pad] Pad018
  BaseFeature = -> Pad017
  Direction = (0,-1,2e-16)
  Length = 119
  Length2 = 10
  Placement = pos=(0,0,0) rot=(1,0,0;1.5708rad)
  Profile = -> Sketch080
  ReferenceAxis = -> Sketch080 [N_Axis]
  Refine = true
  Reversed = true
  Suppressed = false
  Type = 0
FEATURE [PartDesign::Body] Body014  label="Top Battery Guide V2"
  AllowCompound = true
  Group = -> [Binder010,Sketch079,Pad017,Sketch080,Pad018]
  Origin = -> Origin027
  Tip = -> Pad018
FEATURE [Sketcher::SketchObject] Sketch082
  ArcFitTolerance = 1e-06
  AttachmentSupport = -> [YZ_Plane001]
  ExternalGeometry = -> [Pocket031]
  FullyConstrained = false
  MakeInternals = false
  MapMode = 5
  Placement = pos=(0,0,0) rot=(0.57735,0.57735,0.57735;2.0944rad)
  sketch-geometry (4):
    g0: LineSegment StartX=62.4106 StartY=9 StartZ=0 EndX=62.4106 EndY=6 EndZ=0
    g1: LineSegment StartX=62.4106 StartY=6 StartZ=0 EndX=68.0477 EndY=6 EndZ=0
    g2: LineSegment StartX=62.4106 StartY=9 StartZ=0 EndX=65.1631 EndY=9 EndZ=0
    g3: LineSegment StartX=65.1631 StartY=9 StartZ=0 EndX=68.0477 EndY=6 EndZ=0
  constraints (8):
    c: Coincident(g-4,g0)
    c: Coincident(g0,g-3)
    c: Coincident(g0,g1)
    c: PointOnObject(g1,g-5)
    c: Coincident(g0,g2)
    c: Horizontal(g2)
    c: Coincident(g2,g3)
    c: Coincident(g3,g1)
FEATURE [PartDesign::Pocket] Pocket037
  BaseFeature = -> Pocket031
  Direction = (-1,0,0)
  Length = 15
  Length2 = 5
  Midplane = true
  Profile = -> Sketch082
  ReferenceAxis = -> Sketch082 [N_Axis]
  Refine = true
  Suppressed = false
  Type = 0
FEATURE [Sketcher::SketchObject] Sketch083
  ArcFitTolerance = 1e-06
  AttachmentOffset = pos=(0,0,4) rot=(0,0,1;0rad)
  AttachmentSupport = -> [XY_Plane001]
  ExternalGeometry = -> [Pocket037]
  FullyConstrained = false
  MakeInternals = false
  MapMode = 5
  Placement = pos=(0,0,4) rot=(0,0,1;0rad)
  sketch-geometry (6):
    g0: LineSegment StartX=-9 StartY=57.64 StartZ=0 EndX=0 EndY=57.64 EndZ=0
    g1: LineSegment StartX=0 StartY=60.2464 StartZ=0 EndX=-9 EndY=60.2464 EndZ=0
    g2: LineSegment StartX=-9 StartY=60.2464 StartZ=0 EndX=-9 EndY=57.64 EndZ=0
    g3: LineSegment StartX=9 StartY=57.64 StartZ=0 EndX=0 EndY=57.64 EndZ=0
    g4: LineSegment StartX=0 StartY=60.2464 StartZ=0 EndX=9 EndY=60.2464 EndZ=0
    g5: LineSegment StartX=9 StartY=60.2464 StartZ=0 EndX=9 EndY=57.64 EndZ=0
  constraints (14):
    c: Coincident(g1,g2)
    c: Coincident(g2,g0)
    c: Horizontal(g0)
    c: Horizontal(g1)
    c: Vertical(g2)
    c: Coincident(g0,g-4)
    c: PointOnObject(g1,g-2)
    c: Coincident(g4,g5)
    c: Coincident(g5,g3)
    c: Horizontal(g3)
    c: Horizontal(g4)
    c: Vertical(g5)
    c: Coincident(g1,g4)
    c: Coincident(g0,g3)
FEATURE [PartDesign::Pad] Pad019
  BaseFeature = -> Pocket037
  Direction = (0,0,1)
  Length = 10
  Length2 = 10
  Profile = -> Sketch083
  ReferenceAxis = -> Sketch083 [N_Axis]
  Refine = true
  Reversed = true
  Suppressed = false
  Type = 0
FEATURE [Sketcher::SketchObject] Sketch084
  ArcFitTolerance = 1e-06
  AttachmentOffset = pos=(0,0,0.8) rot=(0,0,1;0rad)
  AttachmentSupport = -> [XY_Plane003]
  ExternalGeometry = -> [Pocket032]
  FullyConstrained = false
  MakeInternals = false
  MapMode = 5
  Placement = pos=(0,0,0.8) rot=(0,0,1;0rad)
  sketch-geometry (4):
    g0: LineSegment StartX=3.91918 StartY=85 StartZ=0 EndX=3.91918 EndY=92.1893 EndZ=0
    g1: LineSegment StartX=3.91918 StartY=92.1893 StartZ=0 EndX=-3.9668 EndY=92.1893 EndZ=0
    g2: LineSegment StartX=-3.9668 StartY=92.1893 StartZ=0 EndX=-3.9668 EndY=85 EndZ=0
    g3: LineSegment StartX=-3.9668 StartY=85 StartZ=0 EndX=3.91918 EndY=85 EndZ=0
  constraints (10):
    c: Coincident(g0,g1)
    c: Coincident(g1,g2)
    c: Coincident(g2,g3)
    c: Coincident(g3,g0)
    c: Vertical(g0)
    c: Vertical(g2)
    c: Horizontal(g1)
    c: Horizontal(g3)
    c: Coincident(g0,g-4)
    c: PointOnObject(g1,g-3)
FEATURE [PartDesign::Pad] Pad020
  BaseFeature = -> Pocket032
  Direction = (0,0,1)
  Length = 0.5
  Length2 = 10
  Placement = pos=(0,85,-1.89e-14) rot=(1,0,0;1.5708rad)
  Profile = -> Sketch084
  ReferenceAxis = -> Sketch084 [N_Axis]
  Refine = true
  Suppressed = false
  Type = 0
FEATURE [Sketcher::SketchObject] Sketch085
  ArcFitTolerance = 1e-06
  AttachmentSupport = -> [XY_Plane003]
  FullyConstrained = false
  MakeInternals = false
  MapMode = 5
  sketch-geometry (5):
    g0: ArcOfCircle CenterX=35 CenterY=83.32 CenterZ=0 NormalX=0 NormalY=0 NormalZ=1 AngleXU=0 Radius=26 StartAngle=3.28095 EndAngle=3.60316
    g1: LineSegment StartX=9.25206 StartY=79.7084 StartZ=0 EndX=0 EndY=79.7084 EndZ=0
    g2: LineSegment StartX=11.7208 StartY=71.7408 StartZ=0 EndX=11.7208 EndY=58.4589 EndZ=0
    g3: LineSegment StartX=11.7208 StartY=58.4589 StartZ=0 EndX=0 EndY=58.4589 EndZ=0
    g4: LineSegment StartX=0 StartY=58.4589 StartZ=0 EndX=0 EndY=79.7084 EndZ=0
  constraints (13):
    c: Coincident(g1,g0)
    c: Horizontal(g1)
    c: PointOnObject(g1,g-2)
    c: DistanceX(g-1,g0) = 35
    c: Radius(g0) = 26
    c: DistanceY(g-1,g0) = 83.32
    c: Coincident(g2,g0)
    c: Vertical(g2)
    c: Coincident(g3,g2)
    c: PointOnObject(g3,g-2)
    c: Horizontal(g3)
    c: Coincident(g4,g3)
    c: Coincident(g4,g1)
FEATURE [PartDesign::Groove] Groove
  Angle = 360
  Angle2 = 60
  Axis = (0,1,0)
  Base = (0,0,0)
  BaseFeature = -> Pad020
  Placement = pos=(0,85,-1.89e-14) rot=(1,0,0;1.5708rad)
  Profile = -> Sketch085
  ReferenceAxis = -> Sketch085 [V_Axis]
  Refine = true
  Suppressed = false
  Type = 0
FEATURE [PartDesign::SubShapeBinder] Binder011
  BindCopyOnChange = 0
  BindMode = 0
  ClaimChildren = false
  Context = -> Part001 [Body015.Binder011.]
  Fuse = false
  MakeFace = true
  OffsetFill = false
  OffsetIntersection = false
  OffsetJoinType = 0
  OffsetOpenResult = false
  PartialLoad = false
  Refine = true
  Relative = true
  Support = -> [Part]
  _Version = 2
FEATURE [Sketcher::SketchObject] Sketch086
  ArcFitTolerance = 1e-06
  AttachmentOffset = pos=(0,0,10) rot=(0,0,1;0rad)
  AttachmentSupport = -> [XY_Plane028]
  ExternalGeometry = -> [Binder011]
  FullyConstrained = true
  MakeInternals = false
  MapMode = 5
  Placement = pos=(0,0,10) rot=(0,0,1;0rad)
  sketch-geometry (4):
    g0: LineSegment StartX=-7.70075 StartY=83.0217 StartZ=0 EndX=0 EndY=68.4 EndZ=0
    g1: LineSegment StartX=0 StartY=68.4 StartZ=0 EndX=7.70075 EndY=83.0217 EndZ=0
    g2: LineSegment StartX=7.70075 StartY=83.0217 StartZ=0 EndX=0 EndY=97.6434 EndZ=0
    g3: LineSegment StartX=0 StartY=97.6434 StartZ=0 EndX=-7.70075 EndY=83.0217 EndZ=0
  constraints (12):
    c: PointOnObject(g0,g-2)
    c: Coincident(g0,g1)
    c: Coincident(g1,g2)
    c: PointOnObject(g2,g-2)
    c: Coincident(g2,g3)
    c: Coincident(g3,g0)
    c: Parallel(g3,g-4)
    c: Parallel(g2,g-3)
    c: Parallel(g1,g-5)
    c: Parallel(g0,g-6)
    c: DistanceY(g-6,g0) = 0.4
    c: DistanceY(g1,g-3) = 0.7
FEATURE [Sketcher::SketchObject] Sketch087
  ArcFitTolerance = 1e-06
  AttachmentSupport = -> [YZ_Plane028]
  ExternalGeometry = -> [Sketch086]
  FullyConstrained = true
  MakeInternals = false
  MapMode = 5
  Placement = pos=(0,0,0) rot=(0.57735,0.57735,0.57735;2.0944rad)
  sketch-geometry (1):
    g0: LineSegment StartX=83.0217 StartY=10 StartZ=0 EndX=83.0217 EndY=14 EndZ=0
  constraints (3):
    c: Coincident(g0,g-3)
    c: Vertical(g0)
    c: DistanceY(g0,g0) = 4
FEATURE [PartDesign::AdditiveLoft] AdditiveLoft001
  Closed = false
  Profile = -> Sketch086
  Refine = true
  Ruled = false
  Sections = -> [Sketch087]
  Suppressed = false
FEATURE [Sketcher::SketchObject] Sketch088
  ArcFitTolerance = 1e-06
  AttachmentOffset = pos=(0,0,10) rot=(0,0,1;0rad)
  AttachmentSupport = -> [XY_Plane028]
  ExternalGeometry = -> [AdditiveLoft001]
  FullyConstrained = true
  MakeInternals = false
  MapMode = 5
  Placement = pos=(0,0,10) rot=(0,0,1;0rad)
  sketch-geometry (4):
    g0: LineSegment StartX=0 StartY=97.6434 StartZ=0 EndX=7.70075 EndY=83.0217 EndZ=0
    g1: LineSegment StartX=7.70075 StartY=83.0217 StartZ=0 EndX=0 EndY=68.4 EndZ=0
    g2: LineSegment StartX=0 StartY=68.4 StartZ=0 EndX=-7.70075 EndY=83.0217 EndZ=0
    g3: LineSegment StartX=-7.70075 StartY=83.0217 StartZ=0 EndX=0 EndY=97.6434 EndZ=0
  constraints (8):
    c: Coincident(g-3,g0)
    c: Coincident(g0,g-4)
    c: Coincident(g0,g1)
    c: Coincident(g1,g-4)
    c: Coincident(g1,g2)
    c: Coincident(g2,g-3)
    c: Coincident(g2,g3)
    c: Coincident(g3,g0)
FEATURE [PartDesign::Pad] Pad021
  BaseFeature = -> AdditiveLoft001
  Direction = (0,0,1)
  Length = 1
  Length2 = 10
  Profile = -> Sketch088
  ReferenceAxis = -> Sketch088 [N_Axis]
  Refine = true
  Reversed = true
  Suppressed = false
  Type = 0
FEATURE [PartDesign::Body] Body015  label="Gold Diamond"
  AllowCompound = true
  Group = -> [Binder011,Sketch086,Sketch087,AdditiveLoft001,Sketch088,Pad021]
  Origin = -> Origin028
  Tip = -> Pad021
FEATURE [Sketcher::SketchObject] Sketch089
  ArcFitTolerance = 1e-06
  AttachmentSupport = -> [XZ_Plane003]
  ExternalGeometry = -> [Groove]
  FullyConstrained = true
  MakeInternals = false
  MapMode = 5
  Placement = pos=(0,0,0) rot=(1,0,0;1.5708rad)
  sketch-geometry (3):
    g0: LineSegment StartX=-2.5 StartY=0.8 StartZ=0 EndX=0 EndY=3.3 EndZ=0
    g1: LineSegment StartX=0 StartY=3.3 StartZ=0 EndX=2.5 EndY=0.8 EndZ=0
    g2: LineSegment StartX=2.5 StartY=0.8 StartZ=0 EndX=-2.5 EndY=0.8 EndZ=0
  constraints (8):
    c: PointOnObject(g0,g-3)
    c: PointOnObject(g0,g-2)
    c: Coincident(g0,g1)
    c: Coincident(g1,g2)
    c: Coincident(g2,g0)
    c: Symmetric(g0,g1,g-2)
    c: DistanceX(g0,g-1) = 2.5
    c: DistanceY(g1,g0) = 2.5
FEATURE [PartDesign::Pocket] Pocket038
  BaseFeature = -> Groove
  Direction = (0,1,-2e-16)
  Length = 100
  Length2 = 5
  Placement = pos=(0,85,-1.89e-14) rot=(1,0,0;1.5708rad)
  Profile = -> Sketch089
  ReferenceAxis = -> Sketch089 [N_Axis]
  Refine = true
  Suppressed = false
  Type = 0
FEATURE [PartDesign::Body] Body002  label="Middle"
  AllowCompound = true
  Group = -> [Sketch010,Pad,Sketch011,Pocket,Binder,Sketch019,Pocket002,Sketch020,Pocket003,Cylinder,Sketch067,Pocket032,Sketch084,Pad020,Sketch085,Groove,Sketch089,Pocket038]
  Origin = -> Origin003
  Tip = -> Pocket038
FEATURE [Sketcher::SketchObject] Sketch090
  ArcFitTolerance = 1e-06
  AttachmentOffset = pos=(0,0,-6) rot=(0,0,1;0rad)
  AttachmentSupport = -> [XY_Plane025]
  FullyConstrained = false
  MakeInternals = false
  MapMode = 5
  Placement = pos=(0,0,-6) rot=(0,0,1;0rad)
  sketch-geometry (15):
    g0: ArcOfCircle CenterX=0 CenterY=110.615 CenterZ=0 NormalX=0 NormalY=0 NormalZ=1 AngleXU=0 Radius=11.6 StartAngle=2.12704 EndAngle=2.55013
    g1: ArcOfCircle CenterX=0 CenterY=110.615 CenterZ=0 NormalX=0 NormalY=0 NormalZ=1 AngleXU=0 Radius=11.3869 StartAngle=2.14541 EndAngle=2.53563
    g2: LineSegment [constr] StartX=0 StartY=110.615 StartZ=0 EndX=-13.7069 EndY=124.322 EndZ=0
    g3: ArcOfCircle CenterX=-6.30474 CenterY=120.352 CenterZ=0 NormalX=0 NormalY=0 NormalZ=1 AngleXU=0 Radius=0.213113 StartAngle=5.287 EndAngle=6.84862
    g4: ArcOfCircle CenterX=-9.50142 CenterY=117.199 CenterZ=0 NormalX=0 NormalY=0 NormalZ=1 AngleXU=0 Radius=0.172686 StartAngle=3.87738 EndAngle=5.67722
    g5: ArcOfCircle CenterX=0 CenterY=110.615 CenterZ=0 NormalX=0 NormalY=0 NormalZ=1 AngleXU=0 Radius=11.5921 StartAngle=0.585799 EndAngle=1.01094
    g6: ArcOfCircle CenterX=0 CenterY=110.615 CenterZ=0 NormalX=0 NormalY=0 NormalZ=1 AngleXU=0 Radius=11.3791 StartAngle=0.600213 EndAngle=0.992554
    g7: ArcOfCircle CenterX=6.3358 CenterY=120.322 CenterZ=0 NormalX=0 NormalY=0 NormalZ=1 AngleXU=0 Radius=0.213192 StartAngle=2.57327 EndAngle=4.13415
    g8: ArcOfCircle CenterX=9.53197 CenterY=117.139 CenterZ=0 NormalX=0 NormalY=0 NormalZ=1 AngleXU=0 Radius=0.171808 StartAngle=3.74181 EndAngle=5.54773
    g9: ArcOfCircle CenterX=0 CenterY=110.615 CenterZ=0 NormalX=0 NormalY=0 NormalZ=1 AngleXU=0 Radius=11.45 StartAngle=4.13682 EndAngle=4.3738
    g10: ArcOfCircle CenterX=0 CenterY=110.615 CenterZ=0 NormalX=0 NormalY=0 NormalZ=1 AngleXU=0 Radius=11.0869 StartAngle=4.16543 EndAngle=4.34739
    g11: LineSegment StartX=-3.78062 StartY=99.881 StartZ=0 EndX=-3.80322 EndY=99.8149 EndZ=0
    g12: ArcOfCircle CenterX=-4.06449 CenterY=99.978 CenterZ=0 NormalX=0 NormalY=0 NormalZ=1 AngleXU=0 Radius=0.3 StartAngle=5.95382 EndAngle=7.48899
    g13: LineSegment StartX=-6.12713 StartY=101.108 StartZ=0 EndX=-6.23233 EndY=101.01 EndZ=0
    g14: ArcOfCircle CenterX=-5.92213 CenterY=100.889 CenterZ=0 NormalX=0 NormalY=0 NormalZ=1 AngleXU=0 Radius=0.299876 StartAngle=1.02384 EndAngle=2.32349
  constraints (27):
    c: Coincident(g0,g-4)
    c: PointOnObject(g0,g-4)
    c: Coincident(g1,g0)
    c: Coincident(g2,g0)
    c: Angle(g-2,g2) = 0.785398
    c: Distance(g0,g1) = 0.3
    c: PointOnObject(g3,g-4)
    c: Coincident(g3,g0)
    c: Coincident(g4,g0)
    c: Tangent(g4,g1) = 1.5708
    c: Tangent(g3,g1) = 1.5708
    c: Coincident(g6,g5)
    c: Distance(g5,g6) = 0.3
    c: Coincident(g7,g5)
    c: Coincident(g8,g5)
    c: Tangent(g8,g6) = 1.5708
    c: Tangent(g7,g6) = 1.5708
    c: Coincident(g9,g0)
    c: PointOnObject(g9,g-3)
    c: Coincident(g10,g0)
    c: Coincident(g9,g11)
    c: Tangent(g10,g12) = 1.5708
    c: Tangent(g11,g12) = 1.5708
    c: Coincident(g13,g9)
    c: Tangent(g13,g14) = -1.5708
    c: Tangent(g10,g14) = 1.5708
    c: Distance(g12,g10) = 0.3
FEATURE [PartDesign::Pad] Pad022
  BaseFeature = -> Pocket036
  Direction = (0,0,1)
  Length = 1
  Length2 = 10
  Profile = -> Sketch090
  ReferenceAxis = -> Sketch090 [N_Axis]
  Refine = true
  Suppressed = false
  Type = 0
FEATURE [Sketcher::SketchObject] Sketch091
  ArcFitTolerance = 1e-06
  AttachmentOffset = pos=(0,0,-77) rot=(0,0,1;0rad)
  AttachmentSupport = -> [XZ_Plane025]
  FullyConstrained = false
  MakeInternals = false
  MapMode = 5
  Placement = pos=(0,77,-1.71e-14) rot=(1,0,0;1.5708rad)
  sketch-geometry (3):
    g0: LineSegment StartX=-3.31258 StartY=0 StartZ=0 EndX=0 EndY=-3.5 EndZ=0
    g1: LineSegment StartX=0 StartY=-3.5 StartZ=0 EndX=3.31258 EndY=0 EndZ=0
    g2: LineSegment StartX=-3.31258 StartY=0 StartZ=0 EndX=3.31258 EndY=0 EndZ=0
  constraints (6):
    c: PointOnObject(g0,g-1)
    c: Coincident(g0,g1)
    c: Symmetric(g0,g1,g-2)
    c: DistanceY(g0,g-1) = 3.5
    c: Coincident(g2,g0)
    c: Coincident(g2,g1)
FEATURE [PartDesign::Pocket] Pocket039
  BaseFeature = -> Pad022
  Direction = (0,1,-2e-16)
  Length = 11
  Length2 = 5
  Profile = -> Sketch091
  ReferenceAxis = -> Sketch091 [N_Axis]
  Refine = true
  Suppressed = false
  Type = 0
FEATURE [PartDesign::Chamfer] Chamfer001
  Angle = 45
  Base = -> Pocket039 [Edge160,Edge159]
  BaseFeature = -> Pocket039
  ChamferType = 0
  FlipDirection = false
  Refine = true
  Size = 1.35
  Size2 = 1
  SupportTransform = false
  Suppressed = false
  UseAllEdges = false
FEATURE [PartDesign::Fillet] Fillet001
  Base = -> Chamfer001 [Edge42]
  BaseFeature = -> Chamfer001
  Radius = 0.5
  Refine = true
  SupportTransform = false
  Suppressed = false
  UseAllEdges = false
FEATURE [PartDesign::SubtractiveBox] Box
  AttacherType = Attacher::AttachEngine3D
  AttachmentOffset = pos=(15,90,-18) rot=(0,0,1;0rad)
  AttachmentSupport = -> [XY_Plane025]
  BaseFeature = -> Fillet001
  Height = 24
  Length = 10
  MapMode = 5
  Placement = pos=(15,90,-18) rot=(0,0,1;0rad)
  Refine = true
  Suppressed = false
  Width = 10
FEATURE [PartDesign::Body] Body012  label="Speaker Belt"
  AllowCompound = true
  Group = -> [Binder006,Sketch070,Binder007,Pad014,Sketch071,Pocket033,Sketch072,Pocket034,Sketch073,Pocket035,Sketch074,Pad015,Sketch076,Pad016,Sketch077,Pocket036,Sketch090,Pad022,Sketch091,Pocket039,Chamfer001,Fillet001,Box]
  Origin = -> Origin025
  Tip = -> Box
FEATURE [App::Part] Part001  label="Other Parts"
  Group = -> [Body005,Body010,Body011,Body012,Body013,Body014,Body015]
  Origin = -> Origin016
FEATURE [Sketcher::SketchObject] Sketch092
  ArcFitTolerance = 1e-06
  AttachmentSupport = -> [YZ_Plane001]
  FullyConstrained = true
  MakeInternals = false
  MapMode = 5
  Placement = pos=(0,0,0) rot=(0.57735,0.57735,0.57735;2.0944rad)
  sketch-geometry (4):
    g0: ArcOfCircle CenterX=-52 CenterY=17.5 CenterZ=0 NormalX=0 NormalY=0 NormalZ=1 AngleXU=0 Radius=0.6 StartAngle=1.5708 EndAngle=4.71239
    g1: ArcOfCircle CenterX=-50 CenterY=17.5 CenterZ=0 NormalX=0 NormalY=0 NormalZ=1 AngleXU=0 Radius=0.6 StartAngle=4.71239 EndAngle=7.85398
    g2: LineSegment StartX=-52 StartY=18.1 StartZ=0 EndX=-50 EndY=18.1 EndZ=0
    g3: LineSegment StartX=-52 StartY=16.9 StartZ=0 EndX=-50 EndY=16.9 EndZ=0
  constraints (10):
    c: Tangent(g0,g2) = 1.5708
    c: Tangent(g0,g3) = -1.5708
    c: Tangent(g1,g2) = 1.5708
    c: Tangent(g1,g3) = -1.5708
    c: Equal(g0,g1)
    c: Horizontal(g2)
    c: DistanceX(g0,g1) = 2
    c: DistanceY(g1,g1) = 1.2
    c: DistanceY(g-1,g0) = 17.5
    c: DistanceX(g1,g-1) = 50
FEATURE [PartDesign::Groove] Groove001
  Angle = 360
  Angle2 = 60
  Axis = (0,1,0)
  Base = (0,0,0)
  BaseFeature = -> Pad019
  Profile = -> Sketch092
  ReferenceAxis = -> Sketch092 [H_Axis]
  Refine = true
  Reversed = true
  Suppressed = false
  Type = 0
FEATURE [Sketcher::SketchObject] Sketch093
  ArcFitTolerance = 1e-06
  AttachmentSupport = -> [YZ_Plane001]
  FullyConstrained = true
  MakeInternals = false
  MapMode = 5
  Placement = pos=(0,0,0) rot=(0.57735,0.57735,0.57735;2.0944rad)
  sketch-geometry (4):
    g0: ArcOfCircle CenterX=48 CenterY=17.5 CenterZ=0 NormalX=0 NormalY=0 NormalZ=1 AngleXU=0 Radius=0.6 StartAngle=1.5708 EndAngle=4.71239
    g1: ArcOfCircle CenterX=50 CenterY=17.5 CenterZ=0 NormalX=0 NormalY=0 NormalZ=1 AngleXU=0 Radius=0.6 StartAngle=4.71239 EndAngle=7.85398
    g2: LineSegment StartX=48 StartY=18.1 StartZ=0 EndX=50 EndY=18.1 EndZ=0
    g3: LineSegment StartX=48 StartY=16.9 StartZ=0 EndX=50 EndY=16.9 EndZ=0
  constraints (10):
    c: Tangent(g0,g2) = 1.5708
    c: Tangent(g0,g3) = -1.5708
    c: Tangent(g1,g2) = 1.5708
    c: Tangent(g1,g3) = -1.5708
    c: Equal(g0,g1)
    c: Horizontal(g2)
    c: DistanceX(g0,g1) = 2
    c: DistanceY(g1,g1) = 1.2
    c: DistanceY(g-1,g0) = 17.5
    c: DistanceX(g-1,g0) = 48
FEATURE [PartDesign::Groove] Groove002
  Angle = 360
  Angle2 = 60
  Axis = (0,1,0)
  Base = (0,0,0)
  BaseFeature = -> Groove001
  Profile = -> Sketch093
  ReferenceAxis = -> Sketch093 [H_Axis]
  Refine = true
  Reversed = true
  Suppressed = false
  Type = 0
FEATURE [Sketcher::SketchObject] Sketch094
  ArcFitTolerance = 1e-06
  AttachmentSupport = -> [YZ_Plane001]
  FullyConstrained = true
  MakeInternals = false
  MapMode = 5
  Placement = pos=(0,0,0) rot=(0.57735,0.57735,0.57735;2.0944rad)
  sketch-geometry (4):
    g0: ArcOfCircle CenterX=-52 CenterY=17.5 CenterZ=0 NormalX=0 NormalY=0 NormalZ=1 AngleXU=0 Radius=0.6 StartAngle=1.5708 EndAngle=4.71239
    g1: ArcOfCircle CenterX=-50 CenterY=17.5 CenterZ=0 NormalX=0 NormalY=0 NormalZ=1 AngleXU=0 Radius=0.6 StartAngle=4.71239 EndAngle=7.85398
    g2: LineSegment StartX=-52 StartY=18.1 StartZ=0 EndX=-50 EndY=18.1 EndZ=0
    g3: LineSegment StartX=-52 StartY=16.9 StartZ=0 EndX=-50 EndY=16.9 EndZ=0
  constraints (10):
    c: Tangent(g0,g2) = 1.5708
    c: Tangent(g0,g3) = -1.5708
    c: Tangent(g1,g2) = 1.5708
    c: Tangent(g1,g3) = -1.5708
    c: Equal(g0,g1)
    c: Horizontal(g2)
    c: DistanceX(g0,g1) = 2
    c: DistanceY(g1,g1) = 1.2
    c: DistanceY(g-1,g0) = 17.5
    c: DistanceX(g1,g-1) = 50
FEATURE [PartDesign::SubtractiveHelix] SubtractiveHelix
  Angle = 0
  Axis = (0,1,0)
  Base = (0,0,0)
  BaseFeature = -> Groove002
  Growth = 0
  HasBeenEdited = true
  Height = 100
  LeftHanded = false
  Mode = 0
  Outside = false
  Pitch = 15
  Profile = -> Sketch094
  ReferenceAxis = -> Sketch094 [H_Axis]
  Refine = true
  Suppressed = false
  Tolerance = 0.1
  Turns = 6.66667
FEATURE [Sketcher::SketchObject] Sketch095
  ArcFitTolerance = 1e-06
  AttachmentSupport = -> [YZ_Plane001]
  FullyConstrained = true
  MakeInternals = false
  MapMode = 5
  Placement = pos=(0,0,0) rot=(0.57735,0.57735,0.57735;2.0944rad)
  sketch-geometry (4):
    g0: ArcOfCircle CenterX=-52 CenterY=17.5 CenterZ=0 NormalX=0 NormalY=0 NormalZ=1 AngleXU=0 Radius=0.6 StartAngle=1.5708 EndAngle=4.71239
    g1: ArcOfCircle CenterX=-50 CenterY=17.5 CenterZ=0 NormalX=0 NormalY=0 NormalZ=1 AngleXU=0 Radius=0.6 StartAngle=4.71239 EndAngle=7.85398
    g2: LineSegment StartX=-52 StartY=18.1 StartZ=0 EndX=-50 EndY=18.1 EndZ=0
    g3: LineSegment StartX=-52 StartY=16.9 StartZ=0 EndX=-50 EndY=16.9 EndZ=0
  constraints (10):
    c: Tangent(g0,g2) = 1.5708
    c: Tangent(g0,g3) = -1.5708
    c: Tangent(g1,g2) = 1.5708
    c: Tangent(g1,g3) = -1.5708
    c: Equal(g0,g1)
    c: Horizontal(g2)
    c: DistanceX(g0,g1) = 2
    c: DistanceY(g1,g1) = 1.2
    c: DistanceY(g-1,g0) = 17.5
    c: DistanceX(g1,g-1) = 50
FEATURE [PartDesign::SubtractiveHelix] SubtractiveHelix001
  Angle = 0
  Axis = (0,1,0)
  Base = (0,0,0)
  BaseFeature = -> SubtractiveHelix
  Growth = 0
  HasBeenEdited = true
  Height = 100
  LeftHanded = true
  Mode = 0
  Outside = false
  Pitch = 15
  Profile = -> Sketch095
  ReferenceAxis = -> Sketch095 [H_Axis]
  Refine = true
  Suppressed = false
  Tolerance = 0.1
  Turns = 6.66667
FEATURE [PartDesign::Body] Body  label="HandleBody"
  AllowCompound = true
  Group = -> [Sketch,Revolution,Sketch013,Pocket001,Binder002,Sketch022,Pocket005,Sketch023,Pocket006,Binder003,Sketch027,Pad003,Sketch028,Pocket008,Sketch029,Pocket009,Sketch048,Pocket019,Sketch060,Pad012,Sketch061,Pocket027,Sketch062,Pocket028,Sketch063,Pad013,Sketch064,Pocket029,Sketch065,Pocket030,Sketch066,Pocket031,Sketch082,Pocket037,Sketch083,Pad019,Sketch092,Groove001,Sketch093,Groove002,Sketch094,+3 more]
  Origin = -> Origin001
  Tip = -> SubtractiveHelix001
FEATURE [App::Part] Part  label="Hilt"
  Group = -> [Body,Body001,Body002,Body003,Body004]
  Origin = -> Origin
